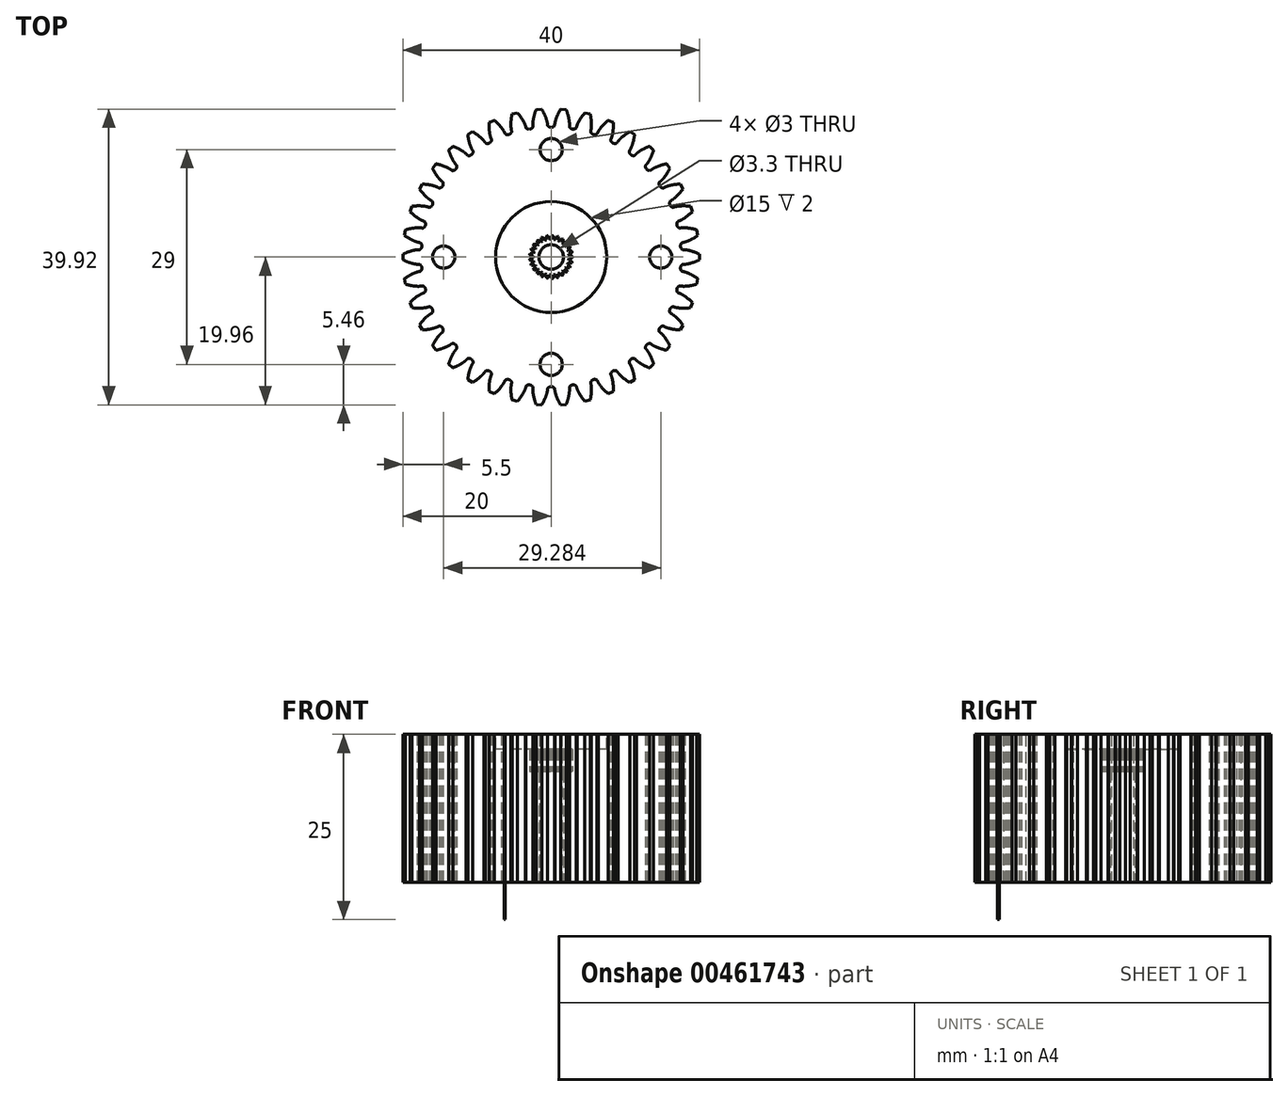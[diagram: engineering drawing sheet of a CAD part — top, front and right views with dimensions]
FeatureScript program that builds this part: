
annotation { "Feature Type Name" : "Feature", "Feature Type Description" : "" }
export const myFeature = defineFeature(function(context is Context, id is Id, definition is map)
    precondition{}
    {
        {
            var Q0;
            Q0=qCreatedBy(makeId("Top.planeOp"),FACE);
            var sketch = newSketch(context, id + "F0", { "sketchPlane" : qUnion([Q0])});
            skLineSegment(sketch, "E0", {"start": v(-6.71, 17.47) * mm, "end": v(-6.37, 16.97) * mm});
            skLineSegment(sketch, "E1", {"start": v(-6.37, 16.97) * mm, "end": v(-6.2, 16.63) * mm});
            skArc(sketch, "E2", {"start": v(-6.71, 17.47) * mm, "mid": v(-7.17, 18) * mm, "end": v(-7.69, 18.46) * mm});
            skLineSegment(sketch, "E3", {"start": v(-8.38, 18.16) * mm, "end": v(-7.69, 18.46) * mm});
            skArc(sketch, "E4", {"start": v(-6.2, 16.63) * mm, "mid": v(-6.27, 16.78) * mm, "end": v(-6.35, 16.93) * mm});
            skArc(sketch, "E5", {"start": v(-6.2, 16.63) * mm, "mid": v(-5.68, 16.55) * mm, "end": v(-5.32, 16.93) * mm});
            skArc(sketch, "E6", {"start": v(-6.35, 16.93) * mm, "mid": v(-6.52, 17.2) * mm, "end": v(-6.71, 17.47) * mm});
            skArc(sketch, "E7", {"start": v(-5.28, 19.3) * mm, "mid": v(-5.4, 18.6) * mm, "end": v(-5.43, 17.9) * mm});
            skArc(sketch, "E8", {"start": v(-5.43, 17.9) * mm, "mid": v(-5.42, 17.59) * mm, "end": v(-5.39, 17.26) * mm});
            skArc(sketch, "E9", {"start": v(-5.39, 17.26) * mm, "mid": v(-5.36, 17.1) * mm, "end": v(-5.32, 16.93) * mm});
            skLineSegment(sketch, "E10", {"start": v(-11.25, 16.53) * mm, "end": v(-10.62, 16.95) * mm});
            skArc(sketch, "E11", {"start": v(-9.5, 16.13) * mm, "mid": v(-10.04, 16.57) * mm, "end": v(-10.62, 16.95) * mm});
            skArc(sketch, "E12", {"start": v(-8.86, 15.38) * mm, "mid": v(-8.33, 15.4) * mm, "end": v(-8.03, 15.83) * mm});
            skArc(sketch, "E13", {"start": v(-9.05, 15.66) * mm, "mid": v(-9.26, 15.9) * mm, "end": v(-9.5, 16.13) * mm});
            skArc(sketch, "E14", {"start": v(-8.86, 15.38) * mm, "mid": v(-8.95, 15.52) * mm, "end": v(-9.05, 15.66) * mm});
            skArc(sketch, "E15", {"start": v(-8.16, 16.14) * mm, "mid": v(-8.1, 15.98) * mm, "end": v(-8.03, 15.83) * mm});
            skArc(sketch, "E16", {"start": v(-8.3, 16.77) * mm, "mid": v(-8.24, 16.45) * mm, "end": v(-8.16, 16.14) * mm});
            skArc(sketch, "E17", {"start": v(-8.38, 18.16) * mm, "mid": v(-8.38, 17.46) * mm, "end": v(-8.3, 16.77) * mm});
            skLineSegment(sketch, "E18", {"start": v(-13.82, 14.46) * mm, "end": v(-13.26, 14.97) * mm});
            skArc(sketch, "E19", {"start": v(-12.02, 14.34) * mm, "mid": v(-12.63, 14.69) * mm, "end": v(-13.26, 14.97) * mm});
            skArc(sketch, "E20", {"start": v(-11.27, 13.71) * mm, "mid": v(-10.75, 13.81) * mm, "end": v(-10.53, 14.3) * mm});
            skArc(sketch, "E21", {"start": v(-11.5, 13.95) * mm, "mid": v(-11.76, 14.16) * mm, "end": v(-12.02, 14.34) * mm});
            skArc(sketch, "E22", {"start": v(-11.27, 13.71) * mm, "mid": v(-11.38, 13.84) * mm, "end": v(-11.5, 13.95) * mm});
            skArc(sketch, "E23", {"start": v(-10.7, 14.58) * mm, "mid": v(-10.62, 14.43) * mm, "end": v(-10.53, 14.3) * mm});
            skArc(sketch, "E24", {"start": v(-10.95, 15.18) * mm, "mid": v(-10.84, 14.87) * mm, "end": v(-10.7, 14.58) * mm});
            skArc(sketch, "E25", {"start": v(-11.25, 16.53) * mm, "mid": v(-11.14, 15.85) * mm, "end": v(-10.95, 15.18) * mm});
            skLineSegment(sketch, "E26", {"start": v(-16.01, 11.98) * mm, "end": v(-15.55, 12.58) * mm});
            skArc(sketch, "E27", {"start": v(-14.22, 12.17) * mm, "mid": v(-14.87, 12.4) * mm, "end": v(-15.55, 12.58) * mm});
            skArc(sketch, "E28", {"start": v(-13.37, 11.67) * mm, "mid": v(-12.88, 11.85) * mm, "end": v(-12.74, 12.36) * mm});
            skArc(sketch, "E29", {"start": v(-13.65, 11.87) * mm, "mid": v(-13.93, 12.03) * mm, "end": v(-14.22, 12.17) * mm});
            skArc(sketch, "E30", {"start": v(-13.37, 11.67) * mm, "mid": v(-13.5, 11.78) * mm, "end": v(-13.65, 11.87) * mm});
            skArc(sketch, "E31", {"start": v(-12.96, 12.62) * mm, "mid": v(-12.85, 12.49) * mm, "end": v(-12.74, 12.36) * mm});
            skArc(sketch, "E32", {"start": v(-13.3, 13.17) * mm, "mid": v(-13.14, 12.88) * mm, "end": v(-12.96, 12.62) * mm});
            skArc(sketch, "E33", {"start": v(-13.82, 14.46) * mm, "mid": v(-13.6, 13.8) * mm, "end": v(-13.3, 13.17) * mm});
            skLineSegment(sketch, "E34", {"start": v(-17.77, 9.18) * mm, "end": v(-17.4, 9.85) * mm});
            skArc(sketch, "E35", {"start": v(-16.03, 9.66) * mm, "mid": v(-16.71, 9.8) * mm, "end": v(-17.4, 9.85) * mm});
            skArc(sketch, "E36", {"start": v(-15.11, 9.31) * mm, "mid": v(-14.65, 9.57) * mm, "end": v(-14.6, 10.1) * mm});
            skArc(sketch, "E37", {"start": v(-15.41, 9.46) * mm, "mid": v(-15.72, 9.58) * mm, "end": v(-16.03, 9.66) * mm});
            skArc(sketch, "E38", {"start": v(-15.11, 9.31) * mm, "mid": v(-15.26, 9.4) * mm, "end": v(-15.41, 9.46) * mm});
            skArc(sketch, "E39", {"start": v(-14.86, 10.31) * mm, "mid": v(-14.73, 10.2) * mm, "end": v(-14.6, 10.1) * mm});
            skArc(sketch, "E40", {"start": v(-15.29, 10.8) * mm, "mid": v(-15.08, 10.55) * mm, "end": v(-14.86, 10.31) * mm});
            skArc(sketch, "E41", {"start": v(-16.01, 11.98) * mm, "mid": v(-15.68, 11.37) * mm, "end": v(-15.29, 10.8) * mm});
            skLineSegment(sketch, "E42", {"start": v(-19.04, 6.13) * mm, "end": v(-18.8, 6.85) * mm});
            skArc(sketch, "E43", {"start": v(-17.4, 6.9) * mm, "mid": v(-18.1, 6.9) * mm, "end": v(-18.8, 6.85) * mm});
            skArc(sketch, "E44", {"start": v(-16.44, 6.7) * mm, "mid": v(-16.03, 7.03) * mm, "end": v(-16.06, 7.56) * mm});
            skArc(sketch, "E45", {"start": v(-16.76, 6.8) * mm, "mid": v(-17.08, 6.86) * mm, "end": v(-17.4, 6.9) * mm});
            skArc(sketch, "E46", {"start": v(-16.44, 6.7) * mm, "mid": v(-16.6, 6.75) * mm, "end": v(-16.76, 6.8) * mm});
            skArc(sketch, "E47", {"start": v(-16.35, 7.73) * mm, "mid": v(-16.2, 7.64) * mm, "end": v(-16.06, 7.56) * mm});
            skArc(sketch, "E48", {"start": v(-16.86, 8.13) * mm, "mid": v(-16.61, 7.92) * mm, "end": v(-16.35, 7.73) * mm});
            skArc(sketch, "E49", {"start": v(-17.77, 9.18) * mm, "mid": v(-17.34, 8.63) * mm, "end": v(-16.86, 8.13) * mm});
            skLineSegment(sketch, "E50", {"start": v(-19.79, 2.92) * mm, "end": v(-19.66, 3.66) * mm});
            skArc(sketch, "E51", {"start": v(-18.3, 3.93) * mm, "mid": v(-18.99, 3.84) * mm, "end": v(-19.66, 3.66) * mm});
            skArc(sketch, "E52", {"start": v(-17.32, 3.9) * mm, "mid": v(-16.97, 4.3) * mm, "end": v(-17.09, 4.81) * mm});
            skArc(sketch, "E53", {"start": v(-17.65, 3.95) * mm, "mid": v(-17.97, 3.95) * mm, "end": v(-18.3, 3.93) * mm});
            skArc(sketch, "E54", {"start": v(-17.32, 3.9) * mm, "mid": v(-17.48, 3.93) * mm, "end": v(-17.65, 3.95) * mm});
            skArc(sketch, "E55", {"start": v(-17.4, 4.93) * mm, "mid": v(-17.24, 4.87) * mm, "end": v(-17.09, 4.81) * mm});
            skArc(sketch, "E56", {"start": v(-17.96, 5.25) * mm, "mid": v(-17.69, 5.08) * mm, "end": v(-17.4, 4.93) * mm});
            skArc(sketch, "E57", {"start": v(-19.04, 6.13) * mm, "mid": v(-18.52, 5.66) * mm, "end": v(-17.96, 5.25) * mm});
            skLineSegment(sketch, "E58", {"start": v(-20, -0.38) * mm, "end": v(-20, 0.38) * mm});
            skArc(sketch, "E59", {"start": v(-18.7, 0.87) * mm, "mid": v(-19.36, 0.66) * mm, "end": v(-20, 0.38) * mm});
            skArc(sketch, "E60", {"start": v(-17.72, 1) * mm, "mid": v(-17.44, 1.45) * mm, "end": v(-17.64, 1.93) * mm});
            skArc(sketch, "E61", {"start": v(-18.06, 0.99) * mm, "mid": v(-18.38, 0.94) * mm, "end": v(-18.7, 0.87) * mm});
            skArc(sketch, "E62", {"start": v(-17.72, 1) * mm, "mid": v(-17.9, 1) * mm, "end": v(-18.06, 0.99) * mm});
            skArc(sketch, "E63", {"start": v(-17.98, 2) * mm, "mid": v(-17.81, 1.96) * mm, "end": v(-17.64, 1.93) * mm});
            skArc(sketch, "E64", {"start": v(-18.58, 2.22) * mm, "mid": v(-18.28, 2.1) * mm, "end": v(-17.98, 2) * mm});
            skArc(sketch, "E65", {"start": v(-19.79, 2.92) * mm, "mid": v(-19.2, 2.54) * mm, "end": v(-18.58, 2.22) * mm});
            skLineSegment(sketch, "E66", {"start": v(-19.66, -3.66) * mm, "end": v(-19.79, -2.92) * mm});
            skArc(sketch, "E67", {"start": v(-18.58, -2.22) * mm, "mid": v(-19.2, -2.54) * mm, "end": v(-19.79, -2.92) * mm});
            skArc(sketch, "E68", {"start": v(-17.64, -1.93) * mm, "mid": v(-17.44, -1.45) * mm, "end": v(-17.72, -1) * mm});
            skArc(sketch, "E69", {"start": v(-17.98, -2) * mm, "mid": v(-18.28, -2.1) * mm, "end": v(-18.58, -2.22) * mm});
            skArc(sketch, "E70", {"start": v(-17.64, -1.93) * mm, "mid": v(-17.81, -1.96) * mm, "end": v(-17.98, -2) * mm});
            skArc(sketch, "E71", {"start": v(-18.06, -0.99) * mm, "mid": v(-17.9, -1) * mm, "end": v(-17.72, -1) * mm});
            skArc(sketch, "E72", {"start": v(-18.7, -0.87) * mm, "mid": v(-18.38, -0.94) * mm, "end": v(-18.06, -0.99) * mm});
            skArc(sketch, "E73", {"start": v(-20, -0.38) * mm, "mid": v(-19.36, -0.66) * mm, "end": v(-18.7, -0.87) * mm});
            skLineSegment(sketch, "E74", {"start": v(-18.8, -6.85) * mm, "end": v(-19.04, -6.13) * mm});
            skArc(sketch, "E75", {"start": v(-17.96, -5.25) * mm, "mid": v(-18.52, -5.66) * mm, "end": v(-19.04, -6.13) * mm});
            skArc(sketch, "E76", {"start": v(-17.09, -4.81) * mm, "mid": v(-16.97, -4.3) * mm, "end": v(-17.32, -3.9) * mm});
            skArc(sketch, "E77", {"start": v(-17.4, -4.93) * mm, "mid": v(-17.69, -5.08) * mm, "end": v(-17.96, -5.25) * mm});
            skArc(sketch, "E78", {"start": v(-17.09, -4.81) * mm, "mid": v(-17.24, -4.87) * mm, "end": v(-17.4, -4.93) * mm});
            skArc(sketch, "E79", {"start": v(-17.65, -3.95) * mm, "mid": v(-17.48, -3.93) * mm, "end": v(-17.32, -3.9) * mm});
            skArc(sketch, "E80", {"start": v(-18.3, -3.93) * mm, "mid": v(-17.97, -3.95) * mm, "end": v(-17.65, -3.95) * mm});
            skArc(sketch, "E81", {"start": v(-19.66, -3.66) * mm, "mid": v(-18.99, -3.84) * mm, "end": v(-18.3, -3.93) * mm});
            skLineSegment(sketch, "E82", {"start": v(-17.4, -9.85) * mm, "end": v(-17.77, -9.18) * mm});
            skArc(sketch, "E83", {"start": v(-16.86, -8.13) * mm, "mid": v(-17.34, -8.63) * mm, "end": v(-17.77, -9.18) * mm});
            skArc(sketch, "E84", {"start": v(-16.06, -7.56) * mm, "mid": v(-16.03, -7.03) * mm, "end": v(-16.44, -6.7) * mm});
            skArc(sketch, "E85", {"start": v(-16.35, -7.73) * mm, "mid": v(-16.61, -7.92) * mm, "end": v(-16.86, -8.13) * mm});
            skArc(sketch, "E86", {"start": v(-16.06, -7.56) * mm, "mid": v(-16.2, -7.64) * mm, "end": v(-16.35, -7.73) * mm});
            skArc(sketch, "E87", {"start": v(-16.76, -6.8) * mm, "mid": v(-16.6, -6.75) * mm, "end": v(-16.44, -6.7) * mm});
            skArc(sketch, "E88", {"start": v(-17.4, -6.9) * mm, "mid": v(-17.08, -6.86) * mm, "end": v(-16.76, -6.8) * mm});
            skArc(sketch, "E89", {"start": v(-18.8, -6.85) * mm, "mid": v(-18.1, -6.9) * mm, "end": v(-17.4, -6.9) * mm});
            skLineSegment(sketch, "E90", {"start": v(-15.55, -12.58) * mm, "end": v(-16.01, -11.98) * mm});
            skArc(sketch, "E91", {"start": v(-15.29, -10.8) * mm, "mid": v(-15.68, -11.37) * mm, "end": v(-16.01, -11.98) * mm});
            skArc(sketch, "E92", {"start": v(-14.6, -10.1) * mm, "mid": v(-14.65, -9.57) * mm, "end": v(-15.11, -9.31) * mm});
            skArc(sketch, "E93", {"start": v(-14.86, -10.31) * mm, "mid": v(-15.08, -10.55) * mm, "end": v(-15.29, -10.8) * mm});
            skArc(sketch, "E94", {"start": v(-14.6, -10.1) * mm, "mid": v(-14.73, -10.2) * mm, "end": v(-14.86, -10.31) * mm});
            skArc(sketch, "E95", {"start": v(-15.41, -9.46) * mm, "mid": v(-15.26, -9.4) * mm, "end": v(-15.11, -9.31) * mm});
            skArc(sketch, "E96", {"start": v(-16.03, -9.66) * mm, "mid": v(-15.72, -9.58) * mm, "end": v(-15.41, -9.46) * mm});
            skArc(sketch, "E97", {"start": v(-17.4, -9.85) * mm, "mid": v(-16.71, -9.8) * mm, "end": v(-16.03, -9.66) * mm});
            skLineSegment(sketch, "E98", {"start": v(-13.26, -14.97) * mm, "end": v(-13.82, -14.46) * mm});
            skArc(sketch, "E99", {"start": v(-13.3, -13.17) * mm, "mid": v(-13.6, -13.8) * mm, "end": v(-13.82, -14.46) * mm});
            skArc(sketch, "E100", {"start": v(-12.74, -12.36) * mm, "mid": v(-12.88, -11.85) * mm, "end": v(-13.37, -11.67) * mm});
            skArc(sketch, "E101", {"start": v(-12.96, -12.62) * mm, "mid": v(-13.14, -12.88) * mm, "end": v(-13.3, -13.17) * mm});
            skArc(sketch, "E102", {"start": v(-12.74, -12.36) * mm, "mid": v(-12.85, -12.49) * mm, "end": v(-12.96, -12.62) * mm});
            skArc(sketch, "E103", {"start": v(-13.64, -11.87) * mm, "mid": v(-13.5, -11.78) * mm, "end": v(-13.37, -11.67) * mm});
            skArc(sketch, "E104", {"start": v(-14.22, -12.17) * mm, "mid": v(-13.93, -12.03) * mm, "end": v(-13.64, -11.87) * mm});
            skArc(sketch, "E105", {"start": v(-15.55, -12.58) * mm, "mid": v(-14.87, -12.4) * mm, "end": v(-14.22, -12.17) * mm});
            skLineSegment(sketch, "E106", {"start": v(-10.62, -16.95) * mm, "end": v(-11.25, -16.53) * mm});
            skArc(sketch, "E107", {"start": v(-10.95, -15.18) * mm, "mid": v(-11.14, -15.85) * mm, "end": v(-11.25, -16.53) * mm});
            skArc(sketch, "E108", {"start": v(-10.53, -14.3) * mm, "mid": v(-10.75, -13.81) * mm, "end": v(-11.27, -13.71) * mm});
            skArc(sketch, "E109", {"start": v(-10.7, -14.58) * mm, "mid": v(-10.84, -14.87) * mm, "end": v(-10.95, -15.18) * mm});
            skArc(sketch, "E110", {"start": v(-10.53, -14.3) * mm, "mid": v(-10.62, -14.43) * mm, "end": v(-10.7, -14.58) * mm});
            skArc(sketch, "E111", {"start": v(-11.5, -13.95) * mm, "mid": v(-11.38, -13.84) * mm, "end": v(-11.27, -13.71) * mm});
            skArc(sketch, "E112", {"start": v(-12.02, -14.34) * mm, "mid": v(-11.76, -14.16) * mm, "end": v(-11.5, -13.95) * mm});
            skArc(sketch, "E113", {"start": v(-13.26, -14.97) * mm, "mid": v(-12.63, -14.69) * mm, "end": v(-12.02, -14.34) * mm});
            skLineSegment(sketch, "E114", {"start": v(-7.69, -18.46) * mm, "end": v(-8.38, -18.16) * mm});
            skArc(sketch, "E115", {"start": v(-8.3, -16.77) * mm, "mid": v(-8.38, -17.46) * mm, "end": v(-8.38, -18.16) * mm});
            skArc(sketch, "E116", {"start": v(-8.03, -15.83) * mm, "mid": v(-8.33, -15.4) * mm, "end": v(-8.86, -15.38) * mm});
            skArc(sketch, "E117", {"start": v(-8.16, -16.14) * mm, "mid": v(-8.24, -16.45) * mm, "end": v(-8.3, -16.77) * mm});
            skArc(sketch, "E118", {"start": v(-8.03, -15.83) * mm, "mid": v(-8.1, -15.98) * mm, "end": v(-8.16, -16.14) * mm});
            skArc(sketch, "E119", {"start": v(-9.05, -15.66) * mm, "mid": v(-8.95, -15.52) * mm, "end": v(-8.86, -15.38) * mm});
            skArc(sketch, "E120", {"start": v(-9.5, -16.13) * mm, "mid": v(-9.26, -15.9) * mm, "end": v(-9.05, -15.66) * mm});
            skArc(sketch, "E121", {"start": v(-10.62, -16.95) * mm, "mid": v(-10.04, -16.57) * mm, "end": v(-9.5, -16.13) * mm});
            skLineSegment(sketch, "E122", {"start": v(-4.54, -19.48) * mm, "end": v(-5.28, -19.3) * mm});
            skArc(sketch, "E123", {"start": v(-5.43, -17.9) * mm, "mid": v(-5.4, -18.6) * mm, "end": v(-5.28, -19.3) * mm});
            skArc(sketch, "E124", {"start": v(-5.32, -16.93) * mm, "mid": v(-5.68, -16.55) * mm, "end": v(-6.2, -16.63) * mm});
            skArc(sketch, "E125", {"start": v(-5.39, -17.26) * mm, "mid": v(-5.42, -17.59) * mm, "end": v(-5.43, -17.9) * mm});
            skArc(sketch, "E126", {"start": v(-5.32, -16.93) * mm, "mid": v(-5.36, -17.1) * mm, "end": v(-5.39, -17.26) * mm});
            skArc(sketch, "E127", {"start": v(-6.35, -16.93) * mm, "mid": v(-6.27, -16.78) * mm, "end": v(-6.2, -16.63) * mm});
            skArc(sketch, "E128", {"start": v(-6.71, -17.47) * mm, "mid": v(-6.52, -17.2) * mm, "end": v(-6.35, -16.93) * mm});
            skArc(sketch, "E129", {"start": v(-7.69, -18.46) * mm, "mid": v(-7.17, -18) * mm, "end": v(-6.71, -17.47) * mm});
            skLineSegment(sketch, "E130", {"start": v(-1.27, -19.96) * mm, "end": v(-2.03, -19.9) * mm});
            skArc(sketch, "E131", {"start": v(-2.4, -18.56) * mm, "mid": v(-2.25, -19.24) * mm, "end": v(-2.03, -19.9) * mm});
            skArc(sketch, "E132", {"start": v(-2.46, -17.58) * mm, "mid": v(-2.88, -17.26) * mm, "end": v(-3.38, -17.42) * mm});
            skArc(sketch, "E133", {"start": v(-2.47, -17.92) * mm, "mid": v(-2.46, -18.24) * mm, "end": v(-2.4, -18.56) * mm});
            skArc(sketch, "E134", {"start": v(-2.46, -17.58) * mm, "mid": v(-2.47, -17.75) * mm, "end": v(-2.47, -17.92) * mm});
            skArc(sketch, "E135", {"start": v(-3.48, -17.75) * mm, "mid": v(-3.43, -17.59) * mm, "end": v(-3.38, -17.42) * mm});
            skArc(sketch, "E136", {"start": v(-3.75, -18.34) * mm, "mid": v(-3.6, -18.05) * mm, "end": v(-3.48, -17.75) * mm});
            skArc(sketch, "E137", {"start": v(-4.54, -19.48) * mm, "mid": v(-4.11, -18.93) * mm, "end": v(-3.75, -18.34) * mm});
            skLineSegment(sketch, "E138", {"start": v(2.03, -19.9) * mm, "end": v(1.27, -19.96) * mm});
            skArc(sketch, "E139", {"start": v(0.68, -18.7) * mm, "mid": v(0.94, -19.35) * mm, "end": v(1.27, -19.96) * mm});
            skArc(sketch, "E140", {"start": v(0.47, -17.74) * mm, "mid": v(0, -17.5) * mm, "end": v(-0.47, -17.74) * mm});
            skArc(sketch, "E141", {"start": v(0.5, -18.08) * mm, "mid": v(0.58, -18.4) * mm, "end": v(0.68, -18.7) * mm});
            skArc(sketch, "E142", {"start": v(0.47, -17.74) * mm, "mid": v(0.48, -17.91) * mm, "end": v(0.5, -18.08) * mm});
            skArc(sketch, "E143", {"start": v(-0.5, -18.08) * mm, "mid": v(-0.48, -17.91) * mm, "end": v(-0.47, -17.74) * mm});
            skArc(sketch, "E144", {"start": v(-0.68, -18.7) * mm, "mid": v(-0.58, -18.4) * mm, "end": v(-0.5, -18.08) * mm});
            skArc(sketch, "E145", {"start": v(-1.27, -19.96) * mm, "mid": v(-0.94, -19.35) * mm, "end": v(-0.68, -18.7) * mm});
            skLineSegment(sketch, "E146", {"start": v(5.28, -19.3) * mm, "end": v(4.54, -19.48) * mm});
            skArc(sketch, "E147", {"start": v(3.75, -18.34) * mm, "mid": v(4.11, -18.93) * mm, "end": v(4.54, -19.48) * mm});
            skArc(sketch, "E148", {"start": v(3.38, -17.42) * mm, "mid": v(2.88, -17.26) * mm, "end": v(2.46, -17.58) * mm});
            skArc(sketch, "E149", {"start": v(3.48, -17.75) * mm, "mid": v(3.6, -18.05) * mm, "end": v(3.75, -18.34) * mm});
            skArc(sketch, "E150", {"start": v(3.38, -17.42) * mm, "mid": v(3.43, -17.59) * mm, "end": v(3.48, -17.75) * mm});
            skArc(sketch, "E151", {"start": v(2.47, -17.92) * mm, "mid": v(2.47, -17.75) * mm, "end": v(2.46, -17.58) * mm});
            skArc(sketch, "E152", {"start": v(2.41, -18.56) * mm, "mid": v(2.46, -18.24) * mm, "end": v(2.47, -17.92) * mm});
            skArc(sketch, "E153", {"start": v(2.03, -19.9) * mm, "mid": v(2.25, -19.24) * mm, "end": v(2.41, -18.56) * mm});
            skLineSegment(sketch, "E154", {"start": v(8.38, -18.16) * mm, "end": v(7.69, -18.46) * mm});
            skArc(sketch, "E155", {"start": v(6.71, -17.47) * mm, "mid": v(7.17, -18) * mm, "end": v(7.69, -18.46) * mm});
            skArc(sketch, "E156", {"start": v(6.2, -16.63) * mm, "mid": v(5.68, -16.55) * mm, "end": v(5.32, -16.93) * mm});
            skArc(sketch, "E157", {"start": v(6.35, -16.93) * mm, "mid": v(6.52, -17.2) * mm, "end": v(6.71, -17.47) * mm});
            skArc(sketch, "E158", {"start": v(6.2, -16.63) * mm, "mid": v(6.27, -16.78) * mm, "end": v(6.35, -16.93) * mm});
            skArc(sketch, "E159", {"start": v(5.39, -17.26) * mm, "mid": v(5.36, -17.1) * mm, "end": v(5.32, -16.93) * mm});
            skArc(sketch, "E160", {"start": v(5.43, -17.9) * mm, "mid": v(5.42, -17.59) * mm, "end": v(5.39, -17.26) * mm});
            skArc(sketch, "E161", {"start": v(5.28, -19.3) * mm, "mid": v(5.4, -18.6) * mm, "end": v(5.43, -17.9) * mm});
            skLineSegment(sketch, "E162", {"start": v(11.25, -16.53) * mm, "end": v(10.62, -16.95) * mm});
            skArc(sketch, "E163", {"start": v(9.5, -16.13) * mm, "mid": v(10.04, -16.57) * mm, "end": v(10.62, -16.95) * mm});
            skArc(sketch, "E164", {"start": v(8.86, -15.38) * mm, "mid": v(8.33, -15.4) * mm, "end": v(8.03, -15.83) * mm});
            skArc(sketch, "E165", {"start": v(9.05, -15.66) * mm, "mid": v(9.26, -15.9) * mm, "end": v(9.5, -16.13) * mm});
            skArc(sketch, "E166", {"start": v(8.86, -15.38) * mm, "mid": v(8.95, -15.52) * mm, "end": v(9.05, -15.66) * mm});
            skArc(sketch, "E167", {"start": v(8.16, -16.14) * mm, "mid": v(8.1, -15.98) * mm, "end": v(8.03, -15.83) * mm});
            skArc(sketch, "E168", {"start": v(8.3, -16.77) * mm, "mid": v(8.24, -16.45) * mm, "end": v(8.16, -16.14) * mm});
            skArc(sketch, "E169", {"start": v(8.38, -18.16) * mm, "mid": v(8.38, -17.46) * mm, "end": v(8.3, -16.77) * mm});
            skLineSegment(sketch, "E170", {"start": v(13.82, -14.46) * mm, "end": v(13.26, -14.97) * mm});
            skArc(sketch, "E171", {"start": v(12.02, -14.34) * mm, "mid": v(12.63, -14.69) * mm, "end": v(13.26, -14.97) * mm});
            skArc(sketch, "E172", {"start": v(11.27, -13.71) * mm, "mid": v(10.75, -13.81) * mm, "end": v(10.53, -14.3) * mm});
            skArc(sketch, "E173", {"start": v(11.5, -13.95) * mm, "mid": v(11.76, -14.16) * mm, "end": v(12.02, -14.34) * mm});
            skArc(sketch, "E174", {"start": v(11.27, -13.71) * mm, "mid": v(11.38, -13.84) * mm, "end": v(11.5, -13.95) * mm});
            skArc(sketch, "E175", {"start": v(10.7, -14.58) * mm, "mid": v(10.62, -14.43) * mm, "end": v(10.53, -14.3) * mm});
            skArc(sketch, "E176", {"start": v(10.95, -15.18) * mm, "mid": v(10.84, -14.87) * mm, "end": v(10.7, -14.58) * mm});
            skArc(sketch, "E177", {"start": v(11.25, -16.53) * mm, "mid": v(11.14, -15.85) * mm, "end": v(10.95, -15.18) * mm});
            skLineSegment(sketch, "E178", {"start": v(16.01, -11.98) * mm, "end": v(15.55, -12.58) * mm});
            skArc(sketch, "E179", {"start": v(14.22, -12.17) * mm, "mid": v(14.87, -12.4) * mm, "end": v(15.55, -12.58) * mm});
            skArc(sketch, "E180", {"start": v(13.37, -11.67) * mm, "mid": v(12.88, -11.85) * mm, "end": v(12.74, -12.36) * mm});
            skArc(sketch, "E181", {"start": v(13.65, -11.87) * mm, "mid": v(13.93, -12.03) * mm, "end": v(14.22, -12.17) * mm});
            skArc(sketch, "E182", {"start": v(13.37, -11.67) * mm, "mid": v(13.5, -11.78) * mm, "end": v(13.65, -11.87) * mm});
            skArc(sketch, "E183", {"start": v(12.96, -12.62) * mm, "mid": v(12.85, -12.49) * mm, "end": v(12.74, -12.36) * mm});
            skArc(sketch, "E184", {"start": v(13.3, -13.17) * mm, "mid": v(13.14, -12.88) * mm, "end": v(12.96, -12.62) * mm});
            skArc(sketch, "E185", {"start": v(13.82, -14.46) * mm, "mid": v(13.6, -13.8) * mm, "end": v(13.3, -13.17) * mm});
            skLineSegment(sketch, "E186", {"start": v(17.77, -9.18) * mm, "end": v(17.4, -9.85) * mm});
            skArc(sketch, "E187", {"start": v(16.03, -9.66) * mm, "mid": v(16.71, -9.8) * mm, "end": v(17.4, -9.85) * mm});
            skArc(sketch, "E188", {"start": v(15.11, -9.31) * mm, "mid": v(14.65, -9.57) * mm, "end": v(14.6, -10.1) * mm});
            skArc(sketch, "E189", {"start": v(15.41, -9.46) * mm, "mid": v(15.72, -9.58) * mm, "end": v(16.03, -9.66) * mm});
            skArc(sketch, "E190", {"start": v(15.11, -9.31) * mm, "mid": v(15.26, -9.4) * mm, "end": v(15.41, -9.46) * mm});
            skArc(sketch, "E191", {"start": v(14.86, -10.31) * mm, "mid": v(14.73, -10.2) * mm, "end": v(14.6, -10.1) * mm});
            skArc(sketch, "E192", {"start": v(15.29, -10.8) * mm, "mid": v(15.08, -10.55) * mm, "end": v(14.86, -10.31) * mm});
            skArc(sketch, "E193", {"start": v(16.01, -11.98) * mm, "mid": v(15.68, -11.37) * mm, "end": v(15.29, -10.8) * mm});
            skLineSegment(sketch, "E194", {"start": v(19.04, -6.13) * mm, "end": v(18.8, -6.85) * mm});
            skArc(sketch, "E195", {"start": v(17.4, -6.9) * mm, "mid": v(18.1, -6.9) * mm, "end": v(18.8, -6.85) * mm});
            skArc(sketch, "E196", {"start": v(16.44, -6.7) * mm, "mid": v(16.03, -7.03) * mm, "end": v(16.06, -7.56) * mm});
            skArc(sketch, "E197", {"start": v(16.76, -6.8) * mm, "mid": v(17.08, -6.86) * mm, "end": v(17.4, -6.9) * mm});
            skArc(sketch, "E198", {"start": v(16.44, -6.7) * mm, "mid": v(16.6, -6.75) * mm, "end": v(16.76, -6.8) * mm});
            skArc(sketch, "E199", {"start": v(16.35, -7.73) * mm, "mid": v(16.2, -7.64) * mm, "end": v(16.06, -7.56) * mm});
            skArc(sketch, "E200", {"start": v(16.86, -8.13) * mm, "mid": v(16.61, -7.92) * mm, "end": v(16.35, -7.73) * mm});
            skArc(sketch, "E201", {"start": v(17.77, -9.18) * mm, "mid": v(17.34, -8.63) * mm, "end": v(16.86, -8.13) * mm});
            skLineSegment(sketch, "E202", {"start": v(19.79, -2.92) * mm, "end": v(19.66, -3.66) * mm});
            skArc(sketch, "E203", {"start": v(18.3, -3.93) * mm, "mid": v(18.99, -3.84) * mm, "end": v(19.66, -3.66) * mm});
            skArc(sketch, "E204", {"start": v(17.32, -3.9) * mm, "mid": v(16.97, -4.3) * mm, "end": v(17.09, -4.81) * mm});
            skArc(sketch, "E205", {"start": v(17.65, -3.95) * mm, "mid": v(17.97, -3.95) * mm, "end": v(18.3, -3.93) * mm});
            skArc(sketch, "E206", {"start": v(17.32, -3.9) * mm, "mid": v(17.48, -3.93) * mm, "end": v(17.65, -3.95) * mm});
            skArc(sketch, "E207", {"start": v(17.4, -4.93) * mm, "mid": v(17.24, -4.87) * mm, "end": v(17.09, -4.81) * mm});
            skArc(sketch, "E208", {"start": v(17.96, -5.25) * mm, "mid": v(17.69, -5.08) * mm, "end": v(17.4, -4.93) * mm});
            skArc(sketch, "E209", {"start": v(19.04, -6.13) * mm, "mid": v(18.52, -5.66) * mm, "end": v(17.96, -5.25) * mm});
            skLineSegment(sketch, "E210", {"start": v(20, 0.38) * mm, "end": v(20, -0.38) * mm});
            skArc(sketch, "E211", {"start": v(18.7, -0.87) * mm, "mid": v(19.36, -0.66) * mm, "end": v(20, -0.38) * mm});
            skArc(sketch, "E212", {"start": v(17.72, -1) * mm, "mid": v(17.44, -1.45) * mm, "end": v(17.64, -1.93) * mm});
            skArc(sketch, "E213", {"start": v(18.06, -0.99) * mm, "mid": v(18.38, -0.94) * mm, "end": v(18.7, -0.87) * mm});
            skArc(sketch, "E214", {"start": v(17.72, -1) * mm, "mid": v(17.9, -1) * mm, "end": v(18.06, -0.99) * mm});
            skArc(sketch, "E215", {"start": v(17.98, -2) * mm, "mid": v(17.81, -1.96) * mm, "end": v(17.64, -1.93) * mm});
            skArc(sketch, "E216", {"start": v(18.58, -2.22) * mm, "mid": v(18.28, -2.1) * mm, "end": v(17.98, -2) * mm});
            skArc(sketch, "E217", {"start": v(19.79, -2.92) * mm, "mid": v(19.2, -2.54) * mm, "end": v(18.58, -2.22) * mm});
            skLineSegment(sketch, "E218", {"start": v(19.66, 3.66) * mm, "end": v(19.79, 2.92) * mm});
            skArc(sketch, "E219", {"start": v(18.58, 2.22) * mm, "mid": v(19.2, 2.54) * mm, "end": v(19.79, 2.92) * mm});
            skArc(sketch, "E220", {"start": v(17.64, 1.93) * mm, "mid": v(17.44, 1.45) * mm, "end": v(17.72, 1) * mm});
            skArc(sketch, "E221", {"start": v(17.98, 2) * mm, "mid": v(18.28, 2.1) * mm, "end": v(18.58, 2.22) * mm});
            skArc(sketch, "E222", {"start": v(17.64, 1.93) * mm, "mid": v(17.81, 1.96) * mm, "end": v(17.98, 2) * mm});
            skArc(sketch, "E223", {"start": v(18.06, 0.99) * mm, "mid": v(17.9, 1) * mm, "end": v(17.72, 1) * mm});
            skArc(sketch, "E224", {"start": v(18.7, 0.87) * mm, "mid": v(18.38, 0.94) * mm, "end": v(18.06, 0.99) * mm});
            skArc(sketch, "E225", {"start": v(20, 0.38) * mm, "mid": v(19.36, 0.66) * mm, "end": v(18.7, 0.87) * mm});
            skLineSegment(sketch, "E226", {"start": v(18.8, 6.85) * mm, "end": v(19.04, 6.13) * mm});
            skArc(sketch, "E227", {"start": v(17.96, 5.25) * mm, "mid": v(18.52, 5.66) * mm, "end": v(19.04, 6.13) * mm});
            skArc(sketch, "E228", {"start": v(17.09, 4.81) * mm, "mid": v(16.97, 4.3) * mm, "end": v(17.32, 3.9) * mm});
            skArc(sketch, "E229", {"start": v(17.4, 4.93) * mm, "mid": v(17.69, 5.08) * mm, "end": v(17.96, 5.25) * mm});
            skArc(sketch, "E230", {"start": v(17.09, 4.81) * mm, "mid": v(17.24, 4.87) * mm, "end": v(17.4, 4.93) * mm});
            skArc(sketch, "E231", {"start": v(17.65, 3.95) * mm, "mid": v(17.48, 3.93) * mm, "end": v(17.32, 3.9) * mm});
            skArc(sketch, "E232", {"start": v(18.3, 3.93) * mm, "mid": v(17.97, 3.95) * mm, "end": v(17.65, 3.95) * mm});
            skArc(sketch, "E233", {"start": v(19.66, 3.66) * mm, "mid": v(18.99, 3.84) * mm, "end": v(18.3, 3.93) * mm});
            skLineSegment(sketch, "E234", {"start": v(17.4, 9.85) * mm, "end": v(17.77, 9.18) * mm});
            skArc(sketch, "E235", {"start": v(16.86, 8.13) * mm, "mid": v(17.34, 8.63) * mm, "end": v(17.77, 9.18) * mm});
            skArc(sketch, "E236", {"start": v(16.06, 7.56) * mm, "mid": v(16.03, 7.03) * mm, "end": v(16.44, 6.7) * mm});
            skArc(sketch, "E237", {"start": v(16.35, 7.73) * mm, "mid": v(16.61, 7.92) * mm, "end": v(16.86, 8.13) * mm});
            skArc(sketch, "E238", {"start": v(16.06, 7.56) * mm, "mid": v(16.2, 7.64) * mm, "end": v(16.35, 7.73) * mm});
            skArc(sketch, "E239", {"start": v(16.76, 6.8) * mm, "mid": v(16.6, 6.75) * mm, "end": v(16.44, 6.7) * mm});
            skArc(sketch, "E240", {"start": v(17.4, 6.9) * mm, "mid": v(17.08, 6.86) * mm, "end": v(16.76, 6.8) * mm});
            skArc(sketch, "E241", {"start": v(18.8, 6.85) * mm, "mid": v(18.1, 6.9) * mm, "end": v(17.4, 6.9) * mm});
            skLineSegment(sketch, "E242", {"start": v(15.55, 12.58) * mm, "end": v(16.01, 11.98) * mm});
            skArc(sketch, "E243", {"start": v(15.29, 10.8) * mm, "mid": v(15.68, 11.37) * mm, "end": v(16.01, 11.98) * mm});
            skArc(sketch, "E244", {"start": v(14.6, 10.1) * mm, "mid": v(14.65, 9.57) * mm, "end": v(15.11, 9.31) * mm});
            skArc(sketch, "E245", {"start": v(14.86, 10.31) * mm, "mid": v(15.08, 10.55) * mm, "end": v(15.29, 10.8) * mm});
            skArc(sketch, "E246", {"start": v(14.6, 10.1) * mm, "mid": v(14.73, 10.2) * mm, "end": v(14.86, 10.31) * mm});
            skArc(sketch, "E247", {"start": v(15.41, 9.46) * mm, "mid": v(15.26, 9.4) * mm, "end": v(15.11, 9.31) * mm});
            skArc(sketch, "E248", {"start": v(16.03, 9.66) * mm, "mid": v(15.72, 9.58) * mm, "end": v(15.41, 9.46) * mm});
            skArc(sketch, "E249", {"start": v(17.4, 9.85) * mm, "mid": v(16.71, 9.8) * mm, "end": v(16.03, 9.66) * mm});
            skLineSegment(sketch, "E250", {"start": v(13.26, 14.97) * mm, "end": v(13.82, 14.46) * mm});
            skArc(sketch, "E251", {"start": v(13.3, 13.17) * mm, "mid": v(13.6, 13.8) * mm, "end": v(13.82, 14.46) * mm});
            skArc(sketch, "E252", {"start": v(12.74, 12.36) * mm, "mid": v(12.88, 11.85) * mm, "end": v(13.37, 11.67) * mm});
            skArc(sketch, "E253", {"start": v(12.96, 12.62) * mm, "mid": v(13.14, 12.88) * mm, "end": v(13.3, 13.17) * mm});
            skArc(sketch, "E254", {"start": v(12.74, 12.36) * mm, "mid": v(12.85, 12.49) * mm, "end": v(12.96, 12.62) * mm});
            skArc(sketch, "E255", {"start": v(13.64, 11.87) * mm, "mid": v(13.5, 11.78) * mm, "end": v(13.37, 11.67) * mm});
            skArc(sketch, "E256", {"start": v(14.22, 12.17) * mm, "mid": v(13.93, 12.03) * mm, "end": v(13.64, 11.87) * mm});
            skArc(sketch, "E257", {"start": v(15.55, 12.58) * mm, "mid": v(14.87, 12.4) * mm, "end": v(14.22, 12.17) * mm});
            skLineSegment(sketch, "E258", {"start": v(10.62, 16.95) * mm, "end": v(11.25, 16.53) * mm});
            skArc(sketch, "E259", {"start": v(10.95, 15.18) * mm, "mid": v(11.14, 15.85) * mm, "end": v(11.25, 16.53) * mm});
            skArc(sketch, "E260", {"start": v(10.53, 14.3) * mm, "mid": v(10.75, 13.81) * mm, "end": v(11.27, 13.71) * mm});
            skArc(sketch, "E261", {"start": v(10.7, 14.58) * mm, "mid": v(10.84, 14.87) * mm, "end": v(10.95, 15.18) * mm});
            skArc(sketch, "E262", {"start": v(10.53, 14.3) * mm, "mid": v(10.62, 14.43) * mm, "end": v(10.7, 14.58) * mm});
            skArc(sketch, "E263", {"start": v(11.5, 13.95) * mm, "mid": v(11.38, 13.84) * mm, "end": v(11.27, 13.71) * mm});
            skArc(sketch, "E264", {"start": v(12.02, 14.34) * mm, "mid": v(11.76, 14.16) * mm, "end": v(11.5, 13.95) * mm});
            skArc(sketch, "E265", {"start": v(13.26, 14.97) * mm, "mid": v(12.63, 14.69) * mm, "end": v(12.02, 14.34) * mm});
            skLineSegment(sketch, "E266", {"start": v(7.69, 18.46) * mm, "end": v(8.38, 18.16) * mm});
            skArc(sketch, "E267", {"start": v(8.3, 16.77) * mm, "mid": v(8.38, 17.46) * mm, "end": v(8.38, 18.16) * mm});
            skArc(sketch, "E268", {"start": v(8.03, 15.83) * mm, "mid": v(8.33, 15.4) * mm, "end": v(8.86, 15.38) * mm});
            skArc(sketch, "E269", {"start": v(8.16, 16.14) * mm, "mid": v(8.24, 16.45) * mm, "end": v(8.3, 16.77) * mm});
            skArc(sketch, "E270", {"start": v(8.03, 15.83) * mm, "mid": v(8.1, 15.98) * mm, "end": v(8.16, 16.14) * mm});
            skArc(sketch, "E271", {"start": v(9.05, 15.66) * mm, "mid": v(8.95, 15.52) * mm, "end": v(8.86, 15.38) * mm});
            skArc(sketch, "E272", {"start": v(9.5, 16.13) * mm, "mid": v(9.26, 15.9) * mm, "end": v(9.05, 15.66) * mm});
            skArc(sketch, "E273", {"start": v(10.62, 16.95) * mm, "mid": v(10.04, 16.57) * mm, "end": v(9.5, 16.13) * mm});
            skLineSegment(sketch, "E274", {"start": v(4.54, 19.48) * mm, "end": v(5.28, 19.3) * mm});
            skArc(sketch, "E275", {"start": v(5.43, 17.9) * mm, "mid": v(5.4, 18.6) * mm, "end": v(5.28, 19.3) * mm});
            skArc(sketch, "E276", {"start": v(5.32, 16.93) * mm, "mid": v(5.68, 16.55) * mm, "end": v(6.2, 16.63) * mm});
            skArc(sketch, "E277", {"start": v(5.39, 17.26) * mm, "mid": v(5.42, 17.59) * mm, "end": v(5.43, 17.9) * mm});
            skArc(sketch, "E278", {"start": v(5.32, 16.93) * mm, "mid": v(5.36, 17.1) * mm, "end": v(5.39, 17.26) * mm});
            skArc(sketch, "E279", {"start": v(6.35, 16.93) * mm, "mid": v(6.27, 16.78) * mm, "end": v(6.2, 16.63) * mm});
            skArc(sketch, "E280", {"start": v(6.71, 17.47) * mm, "mid": v(6.52, 17.2) * mm, "end": v(6.35, 16.93) * mm});
            skArc(sketch, "E281", {"start": v(7.69, 18.46) * mm, "mid": v(7.17, 18) * mm, "end": v(6.71, 17.47) * mm});
            skLineSegment(sketch, "E282", {"start": v(1.27, 19.96) * mm, "end": v(2.03, 19.9) * mm});
            skArc(sketch, "E283", {"start": v(2.4, 18.56) * mm, "mid": v(2.25, 19.24) * mm, "end": v(2.03, 19.9) * mm});
            skArc(sketch, "E284", {"start": v(2.46, 17.58) * mm, "mid": v(2.88, 17.26) * mm, "end": v(3.38, 17.42) * mm});
            skArc(sketch, "E285", {"start": v(2.47, 17.92) * mm, "mid": v(2.46, 18.24) * mm, "end": v(2.4, 18.56) * mm});
            skArc(sketch, "E286", {"start": v(2.46, 17.58) * mm, "mid": v(2.47, 17.75) * mm, "end": v(2.47, 17.92) * mm});
            skArc(sketch, "E287", {"start": v(3.48, 17.75) * mm, "mid": v(3.43, 17.59) * mm, "end": v(3.38, 17.42) * mm});
            skArc(sketch, "E288", {"start": v(3.75, 18.34) * mm, "mid": v(3.6, 18.05) * mm, "end": v(3.48, 17.75) * mm});
            skArc(sketch, "E289", {"start": v(4.54, 19.48) * mm, "mid": v(4.11, 18.93) * mm, "end": v(3.75, 18.34) * mm});
            skLineSegment(sketch, "E290", {"start": v(-2.03, 19.9) * mm, "end": v(-1.27, 19.96) * mm});
            skArc(sketch, "E291", {"start": v(-0.68, 18.7) * mm, "mid": v(-0.94, 19.35) * mm, "end": v(-1.27, 19.96) * mm});
            skArc(sketch, "E292", {"start": v(-0.47, 17.74) * mm, "mid": v(0, 17.5) * mm, "end": v(0.47, 17.74) * mm});
            skArc(sketch, "E293", {"start": v(-0.5, 18.08) * mm, "mid": v(-0.58, 18.4) * mm, "end": v(-0.68, 18.7) * mm});
            skArc(sketch, "E294", {"start": v(-0.47, 17.74) * mm, "mid": v(-0.48, 17.91) * mm, "end": v(-0.5, 18.08) * mm});
            skArc(sketch, "E295", {"start": v(0.5, 18.08) * mm, "mid": v(0.48, 17.91) * mm, "end": v(0.47, 17.74) * mm});
            skArc(sketch, "E296", {"start": v(0.68, 18.7) * mm, "mid": v(0.58, 18.4) * mm, "end": v(0.5, 18.08) * mm});
            skArc(sketch, "E297", {"start": v(1.27, 19.96) * mm, "mid": v(0.94, 19.35) * mm, "end": v(0.68, 18.7) * mm});
            skLineSegment(sketch, "E298", {"start": v(-5.28, 19.3) * mm, "end": v(-4.54, 19.48) * mm});
            skArc(sketch, "E299", {"start": v(-3.75, 18.34) * mm, "mid": v(-4.11, 18.93) * mm, "end": v(-4.54, 19.48) * mm});
            skArc(sketch, "E300", {"start": v(-3.38, 17.42) * mm, "mid": v(-2.88, 17.26) * mm, "end": v(-2.46, 17.58) * mm});
            skArc(sketch, "E301", {"start": v(-3.48, 17.75) * mm, "mid": v(-3.6, 18.05) * mm, "end": v(-3.75, 18.34) * mm});
            skArc(sketch, "E302", {"start": v(-3.38, 17.42) * mm, "mid": v(-3.43, 17.59) * mm, "end": v(-3.48, 17.75) * mm});
            skArc(sketch, "E303", {"start": v(-2.47, 17.92) * mm, "mid": v(-2.47, 17.75) * mm, "end": v(-2.46, 17.58) * mm});
            skArc(sketch, "E304", {"start": v(-2.41, 18.56) * mm, "mid": v(-2.46, 18.24) * mm, "end": v(-2.47, 17.92) * mm});
            skArc(sketch, "E305", {"start": v(-2.03, 19.9) * mm, "mid": v(-2.25, 19.24) * mm, "end": v(-2.41, 18.56) * mm});
            skLineSegment(sketch, "E306", {"start": v(-0.04, 2.42) * mm, "end": v(-0.15, 2.4) * mm});
            skLineSegment(sketch, "E307", {"start": v(0.18, 2.9) * mm, "end": v(0.1, 2.9) * mm});
            skArc(sketch, "E308", {"start": v(0.1, 2.9) * mm, "mid": v(0.02, 2.73) * mm, "end": v(-0.04, 2.55) * mm});
            skLineSegment(sketch, "E309", {"start": v(-0.04, 2.42) * mm, "end": v(-0.04, 2.53) * mm});
            skArc(sketch, "E310", {"start": v(-0.04, 2.55) * mm, "mid": v(-0.04, 2.54) * mm, "end": v(-0.04, 2.53) * mm});
            skLineSegment(sketch, "E311", {"start": v(0.34, 2.4) * mm, "end": v(0.45, 2.37) * mm});
            skLineSegment(sketch, "E312", {"start": v(0.18, 2.9) * mm, "end": v(0.26, 2.89) * mm});
            skArc(sketch, "E313", {"start": v(0.35, 2.53) * mm, "mid": v(0.32, 2.71) * mm, "end": v(0.26, 2.89) * mm});
            skLineSegment(sketch, "E314", {"start": v(0.34, 2.4) * mm, "end": v(0.35, 2.5) * mm});
            skArc(sketch, "E315", {"start": v(0.35, 2.5) * mm, "mid": v(0.35, 2.51) * mm, "end": v(0.35, 2.53) * mm});
            skLineSegment(sketch, "E316", {"start": v(-0.64, 2.33) * mm, "end": v(-0.75, 2.3) * mm});
            skLineSegment(sketch, "E317", {"start": v(-0.54, 2.85) * mm, "end": v(-0.62, 2.83) * mm});
            skArc(sketch, "E318", {"start": v(-0.62, 2.83) * mm, "mid": v(-0.66, 2.65) * mm, "end": v(-0.67, 2.46) * mm});
            skArc(sketch, "E319", {"start": v(-0.28, 2.51) * mm, "mid": v(-0.28, 2.52) * mm, "end": v(-0.28, 2.54) * mm});
            skLineSegment(sketch, "E320", {"start": v(-0.64, 2.33) * mm, "end": v(-0.66, 2.44) * mm});
            skArc(sketch, "E321", {"start": v(-0.67, 2.46) * mm, "mid": v(-0.67, 2.45) * mm, "end": v(-0.66, 2.44) * mm});
            skLineSegment(sketch, "E322", {"start": v(-0.27, 2.4) * mm, "end": v(-0.28, 2.51) * mm});
            skArc(sketch, "E323", {"start": v(-0.28, 2.54) * mm, "mid": v(-0.36, 2.7) * mm, "end": v(-0.47, 2.86) * mm});
            skLineSegment(sketch, "E324", {"start": v(-0.54, 2.85) * mm, "end": v(-0.47, 2.86) * mm});
            skLineSegment(sketch, "E325", {"start": v(-0.27, 2.4) * mm, "end": v(-0.15, 2.4) * mm});
            skLineSegment(sketch, "E326", {"start": v(-1.2, 2.1) * mm, "end": v(-1.3, 2.04) * mm});
            skLineSegment(sketch, "E327", {"start": v(-1.23, 2.62) * mm, "end": v(-1.3, 2.6) * mm});
            skArc(sketch, "E328", {"start": v(-1.3, 2.6) * mm, "mid": v(-1.3, 2.4) * mm, "end": v(-1.26, 2.22) * mm});
            skArc(sketch, "E329", {"start": v(-0.9, 2.36) * mm, "mid": v(-0.9, 2.37) * mm, "end": v(-0.9, 2.39) * mm});
            skLineSegment(sketch, "E330", {"start": v(-1.2, 2.1) * mm, "end": v(-1.25, 2.2) * mm});
            skArc(sketch, "E331", {"start": v(-1.26, 2.22) * mm, "mid": v(-1.26, 2.2) * mm, "end": v(-1.25, 2.2) * mm});
            skLineSegment(sketch, "E332", {"start": v(-0.86, 2.26) * mm, "end": v(-0.9, 2.36) * mm});
            skArc(sketch, "E333", {"start": v(-0.9, 2.39) * mm, "mid": v(-1.02, 2.53) * mm, "end": v(-1.16, 2.66) * mm});
            skLineSegment(sketch, "E334", {"start": v(-1.23, 2.62) * mm, "end": v(-1.16, 2.66) * mm});
            skLineSegment(sketch, "E335", {"start": v(-0.86, 2.26) * mm, "end": v(-0.75, 2.3) * mm});
            skLineSegment(sketch, "E336", {"start": v(-1.68, 1.74) * mm, "end": v(-1.76, 1.65) * mm});
            skLineSegment(sketch, "E337", {"start": v(-1.85, 2.23) * mm, "end": v(-1.9, 2.19) * mm});
            skArc(sketch, "E338", {"start": v(-1.9, 2.19) * mm, "mid": v(-1.86, 2) * mm, "end": v(-1.77, 1.84) * mm});
            skArc(sketch, "E339", {"start": v(-1.45, 2.07) * mm, "mid": v(-1.46, 2.08) * mm, "end": v(-1.47, 2.09) * mm});
            skLineSegment(sketch, "E340", {"start": v(-1.68, 1.74) * mm, "end": v(-1.76, 1.82) * mm});
            skArc(sketch, "E341", {"start": v(-1.77, 1.84) * mm, "mid": v(-1.76, 1.83) * mm, "end": v(-1.76, 1.82) * mm});
            skLineSegment(sketch, "E342", {"start": v(-1.4, 1.98) * mm, "end": v(-1.45, 2.07) * mm});
            skArc(sketch, "E343", {"start": v(-1.47, 2.09) * mm, "mid": v(-1.62, 2.2) * mm, "end": v(-1.79, 2.28) * mm});
            skLineSegment(sketch, "E344", {"start": v(-1.85, 2.23) * mm, "end": v(-1.79, 2.28) * mm});
            skLineSegment(sketch, "E345", {"start": v(-1.4, 1.98) * mm, "end": v(-1.3, 2.04) * mm});
            skLineSegment(sketch, "E346", {"start": v(-2.06, 1.26) * mm, "end": v(-2.12, 1.16) * mm});
            skLineSegment(sketch, "E347", {"start": v(-2.35, 1.7) * mm, "end": v(-2.4, 1.64) * mm});
            skArc(sketch, "E348", {"start": v(-2.4, 1.64) * mm, "mid": v(-2.3, 1.48) * mm, "end": v(-2.17, 1.34) * mm});
            skArc(sketch, "E349", {"start": v(-1.92, 1.64) * mm, "mid": v(-1.93, 1.65) * mm, "end": v(-1.94, 1.65) * mm});
            skLineSegment(sketch, "E350", {"start": v(-2.06, 1.26) * mm, "end": v(-2.15, 1.32) * mm});
            skArc(sketch, "E351", {"start": v(-2.17, 1.34) * mm, "mid": v(-2.16, 1.33) * mm, "end": v(-2.15, 1.32) * mm});
            skLineSegment(sketch, "E352", {"start": v(-1.84, 1.57) * mm, "end": v(-1.92, 1.64) * mm});
            skArc(sketch, "E353", {"start": v(-1.94, 1.65) * mm, "mid": v(-2.12, 1.73) * mm, "end": v(-2.3, 1.77) * mm});
            skLineSegment(sketch, "E354", {"start": v(-2.35, 1.7) * mm, "end": v(-2.3, 1.77) * mm});
            skLineSegment(sketch, "E355", {"start": v(-1.84, 1.57) * mm, "end": v(-1.76, 1.65) * mm});
            skLineSegment(sketch, "E356", {"start": v(-2.31, 0.71) * mm, "end": v(-2.34, 0.6) * mm});
            skLineSegment(sketch, "E357", {"start": v(-2.7, 1.07) * mm, "end": v(-2.72, 1) * mm});
            skArc(sketch, "E358", {"start": v(-2.72, 1) * mm, "mid": v(-2.6, 0.86) * mm, "end": v(-2.44, 0.75) * mm});
            skArc(sketch, "E359", {"start": v(-2.27, 1.1) * mm, "mid": v(-2.28, 1.11) * mm, "end": v(-2.3, 1.12) * mm});
            skLineSegment(sketch, "E360", {"start": v(-2.31, 0.71) * mm, "end": v(-2.41, 0.74) * mm});
            skArc(sketch, "E361", {"start": v(-2.44, 0.75) * mm, "mid": v(-2.43, 0.75) * mm, "end": v(-2.41, 0.74) * mm});
            skLineSegment(sketch, "E362", {"start": v(-2.17, 1.06) * mm, "end": v(-2.27, 1.1) * mm});
            skArc(sketch, "E363", {"start": v(-2.3, 1.12) * mm, "mid": v(-2.48, 1.15) * mm, "end": v(-2.67, 1.14) * mm});
            skLineSegment(sketch, "E364", {"start": v(-2.7, 1.07) * mm, "end": v(-2.67, 1.14) * mm});
            skLineSegment(sketch, "E365", {"start": v(-2.17, 1.06) * mm, "end": v(-2.12, 1.16) * mm});
            skLineSegment(sketch, "E366", {"start": v(-2.41, 0.12) * mm, "end": v(-2.41, 0) * mm});
            skLineSegment(sketch, "E367", {"start": v(-2.88, 0.36) * mm, "end": v(-2.89, 0.29) * mm});
            skArc(sketch, "E368", {"start": v(-2.89, 0.29) * mm, "mid": v(-2.73, 0.2) * mm, "end": v(-2.55, 0.13) * mm});
            skArc(sketch, "E369", {"start": v(-2.47, 0.51) * mm, "mid": v(-2.49, 0.51) * mm, "end": v(-2.5, 0.51) * mm});
            skLineSegment(sketch, "E370", {"start": v(-2.41, 0.12) * mm, "end": v(-2.52, 0.12) * mm});
            skArc(sketch, "E371", {"start": v(-2.55, 0.13) * mm, "mid": v(-2.54, 0.12) * mm, "end": v(-2.52, 0.12) * mm});
            skLineSegment(sketch, "E372", {"start": v(-2.37, 0.49) * mm, "end": v(-2.47, 0.51) * mm});
            skArc(sketch, "E373", {"start": v(-2.5, 0.51) * mm, "mid": v(-2.69, 0.5) * mm, "end": v(-2.87, 0.44) * mm});
            skLineSegment(sketch, "E374", {"start": v(-2.88, 0.36) * mm, "end": v(-2.87, 0.44) * mm});
            skLineSegment(sketch, "E375", {"start": v(-2.37, 0.49) * mm, "end": v(-2.34, 0.6) * mm});
            skLineSegment(sketch, "E376", {"start": v(-2.37, -0.49) * mm, "end": v(-2.34, -0.6) * mm});
            skLineSegment(sketch, "E377", {"start": v(-2.88, -0.36) * mm, "end": v(-2.87, -0.44) * mm});
            skArc(sketch, "E378", {"start": v(-2.87, -0.44) * mm, "mid": v(-2.69, -0.5) * mm, "end": v(-2.5, -0.51) * mm});
            skArc(sketch, "E379", {"start": v(-2.52, -0.12) * mm, "mid": v(-2.54, -0.12) * mm, "end": v(-2.55, -0.13) * mm});
            skLineSegment(sketch, "E380", {"start": v(-2.37, -0.49) * mm, "end": v(-2.47, -0.51) * mm});
            skArc(sketch, "E381", {"start": v(-2.5, -0.51) * mm, "mid": v(-2.49, -0.51) * mm, "end": v(-2.47, -0.51) * mm});
            skLineSegment(sketch, "E382", {"start": v(-2.41, -0.12) * mm, "end": v(-2.52, -0.12) * mm});
            skArc(sketch, "E383", {"start": v(-2.55, -0.13) * mm, "mid": v(-2.73, -0.2) * mm, "end": v(-2.89, -0.29) * mm});
            skLineSegment(sketch, "E384", {"start": v(-2.88, -0.36) * mm, "end": v(-2.89, -0.29) * mm});
            skLineSegment(sketch, "E385", {"start": v(-2.41, -0.12) * mm, "end": v(-2.41, 0) * mm});
            skLineSegment(sketch, "E386", {"start": v(-2.17, -1.06) * mm, "end": v(-2.12, -1.16) * mm});
            skLineSegment(sketch, "E387", {"start": v(-2.7, -1.07) * mm, "end": v(-2.67, -1.14) * mm});
            skArc(sketch, "E388", {"start": v(-2.67, -1.14) * mm, "mid": v(-2.48, -1.15) * mm, "end": v(-2.3, -1.12) * mm});
            skArc(sketch, "E389", {"start": v(-2.41, -0.74) * mm, "mid": v(-2.43, -0.75) * mm, "end": v(-2.44, -0.75) * mm});
            skLineSegment(sketch, "E390", {"start": v(-2.17, -1.06) * mm, "end": v(-2.27, -1.1) * mm});
            skArc(sketch, "E391", {"start": v(-2.3, -1.12) * mm, "mid": v(-2.28, -1.11) * mm, "end": v(-2.27, -1.1) * mm});
            skLineSegment(sketch, "E392", {"start": v(-2.31, -0.71) * mm, "end": v(-2.41, -0.74) * mm});
            skArc(sketch, "E393", {"start": v(-2.44, -0.75) * mm, "mid": v(-2.6, -0.86) * mm, "end": v(-2.72, -1) * mm});
            skLineSegment(sketch, "E394", {"start": v(-2.7, -1.07) * mm, "end": v(-2.72, -1) * mm});
            skLineSegment(sketch, "E395", {"start": v(-2.31, -0.71) * mm, "end": v(-2.34, -0.6) * mm});
            skLineSegment(sketch, "E396", {"start": v(-1.84, -1.57) * mm, "end": v(-1.76, -1.65) * mm});
            skLineSegment(sketch, "E397", {"start": v(-2.35, -1.7) * mm, "end": v(-2.3, -1.77) * mm});
            skArc(sketch, "E398", {"start": v(-2.3, -1.77) * mm, "mid": v(-2.12, -1.73) * mm, "end": v(-1.94, -1.65) * mm});
            skArc(sketch, "E399", {"start": v(-2.15, -1.32) * mm, "mid": v(-2.16, -1.33) * mm, "end": v(-2.17, -1.34) * mm});
            skLineSegment(sketch, "E400", {"start": v(-1.84, -1.57) * mm, "end": v(-1.92, -1.64) * mm});
            skArc(sketch, "E401", {"start": v(-1.94, -1.65) * mm, "mid": v(-1.93, -1.65) * mm, "end": v(-1.92, -1.64) * mm});
            skLineSegment(sketch, "E402", {"start": v(-2.06, -1.26) * mm, "end": v(-2.15, -1.32) * mm});
            skArc(sketch, "E403", {"start": v(-2.17, -1.34) * mm, "mid": v(-2.3, -1.48) * mm, "end": v(-2.4, -1.64) * mm});
            skLineSegment(sketch, "E404", {"start": v(-2.35, -1.7) * mm, "end": v(-2.4, -1.64) * mm});
            skLineSegment(sketch, "E405", {"start": v(-2.06, -1.26) * mm, "end": v(-2.12, -1.16) * mm});
            skLineSegment(sketch, "E406", {"start": v(-1.4, -1.98) * mm, "end": v(-1.3, -2.04) * mm});
            skLineSegment(sketch, "E407", {"start": v(-1.85, -2.23) * mm, "end": v(-1.79, -2.28) * mm});
            skArc(sketch, "E408", {"start": v(-1.79, -2.28) * mm, "mid": v(-1.62, -2.2) * mm, "end": v(-1.47, -2.09) * mm});
            skArc(sketch, "E409", {"start": v(-1.76, -1.82) * mm, "mid": v(-1.76, -1.83) * mm, "end": v(-1.77, -1.84) * mm});
            skLineSegment(sketch, "E410", {"start": v(-1.4, -1.98) * mm, "end": v(-1.45, -2.07) * mm});
            skArc(sketch, "E411", {"start": v(-1.47, -2.09) * mm, "mid": v(-1.46, -2.08) * mm, "end": v(-1.45, -2.07) * mm});
            skLineSegment(sketch, "E412", {"start": v(-1.68, -1.74) * mm, "end": v(-1.76, -1.82) * mm});
            skArc(sketch, "E413", {"start": v(-1.77, -1.84) * mm, "mid": v(-1.86, -2) * mm, "end": v(-1.9, -2.19) * mm});
            skLineSegment(sketch, "E414", {"start": v(-1.85, -2.23) * mm, "end": v(-1.9, -2.19) * mm});
            skLineSegment(sketch, "E415", {"start": v(-1.68, -1.74) * mm, "end": v(-1.76, -1.65) * mm});
            skLineSegment(sketch, "E416", {"start": v(-0.86, -2.26) * mm, "end": v(-0.75, -2.3) * mm});
            skLineSegment(sketch, "E417", {"start": v(-1.23, -2.62) * mm, "end": v(-1.16, -2.66) * mm});
            skArc(sketch, "E418", {"start": v(-1.16, -2.66) * mm, "mid": v(-1.02, -2.53) * mm, "end": v(-0.9, -2.39) * mm});
            skArc(sketch, "E419", {"start": v(-1.25, -2.2) * mm, "mid": v(-1.26, -2.2) * mm, "end": v(-1.26, -2.22) * mm});
            skLineSegment(sketch, "E420", {"start": v(-0.86, -2.26) * mm, "end": v(-0.9, -2.36) * mm});
            skArc(sketch, "E421", {"start": v(-0.9, -2.39) * mm, "mid": v(-0.9, -2.37) * mm, "end": v(-0.9, -2.36) * mm});
            skLineSegment(sketch, "E422", {"start": v(-1.2, -2.1) * mm, "end": v(-1.25, -2.2) * mm});
            skArc(sketch, "E423", {"start": v(-1.26, -2.22) * mm, "mid": v(-1.3, -2.4) * mm, "end": v(-1.3, -2.6) * mm});
            skLineSegment(sketch, "E424", {"start": v(-1.23, -2.62) * mm, "end": v(-1.3, -2.6) * mm});
            skLineSegment(sketch, "E425", {"start": v(-1.2, -2.1) * mm, "end": v(-1.3, -2.04) * mm});
            skLineSegment(sketch, "E426", {"start": v(-0.27, -2.4) * mm, "end": v(-0.15, -2.4) * mm});
            skLineSegment(sketch, "E427", {"start": v(-0.54, -2.85) * mm, "end": v(-0.47, -2.86) * mm});
            skArc(sketch, "E428", {"start": v(-0.47, -2.86) * mm, "mid": v(-0.36, -2.7) * mm, "end": v(-0.28, -2.54) * mm});
            skArc(sketch, "E429", {"start": v(-0.66, -2.44) * mm, "mid": v(-0.67, -2.45) * mm, "end": v(-0.67, -2.46) * mm});
            skLineSegment(sketch, "E430", {"start": v(-0.27, -2.4) * mm, "end": v(-0.28, -2.51) * mm});
            skArc(sketch, "E431", {"start": v(-0.28, -2.54) * mm, "mid": v(-0.28, -2.52) * mm, "end": v(-0.28, -2.51) * mm});
            skLineSegment(sketch, "E432", {"start": v(-0.64, -2.33) * mm, "end": v(-0.66, -2.44) * mm});
            skArc(sketch, "E433", {"start": v(-0.67, -2.46) * mm, "mid": v(-0.66, -2.65) * mm, "end": v(-0.62, -2.83) * mm});
            skLineSegment(sketch, "E434", {"start": v(-0.54, -2.85) * mm, "end": v(-0.62, -2.83) * mm});
            skLineSegment(sketch, "E435", {"start": v(-0.64, -2.33) * mm, "end": v(-0.75, -2.3) * mm});
            skLineSegment(sketch, "E436", {"start": v(0.34, -2.4) * mm, "end": v(0.45, -2.37) * mm});
            skLineSegment(sketch, "E437", {"start": v(0.18, -2.9) * mm, "end": v(0.26, -2.89) * mm});
            skArc(sketch, "E438", {"start": v(0.26, -2.89) * mm, "mid": v(0.32, -2.71) * mm, "end": v(0.35, -2.53) * mm});
            skArc(sketch, "E439", {"start": v(-0.04, -2.53) * mm, "mid": v(-0.04, -2.54) * mm, "end": v(-0.04, -2.55) * mm});
            skLineSegment(sketch, "E440", {"start": v(0.34, -2.4) * mm, "end": v(0.35, -2.5) * mm});
            skArc(sketch, "E441", {"start": v(0.35, -2.53) * mm, "mid": v(0.35, -2.51) * mm, "end": v(0.35, -2.5) * mm});
            skLineSegment(sketch, "E442", {"start": v(-0.04, -2.42) * mm, "end": v(-0.04, -2.53) * mm});
            skArc(sketch, "E443", {"start": v(-0.04, -2.55) * mm, "mid": v(0.02, -2.73) * mm, "end": v(0.1, -2.9) * mm});
            skLineSegment(sketch, "E444", {"start": v(0.18, -2.9) * mm, "end": v(0.1, -2.9) * mm});
            skLineSegment(sketch, "E445", {"start": v(-0.04, -2.42) * mm, "end": v(-0.15, -2.4) * mm});
            skLineSegment(sketch, "E446", {"start": v(0.92, -2.23) * mm, "end": v(1.03, -2.18) * mm});
            skLineSegment(sketch, "E447", {"start": v(0.9, -2.76) * mm, "end": v(0.97, -2.73) * mm});
            skArc(sketch, "E448", {"start": v(0.97, -2.73) * mm, "mid": v(0.99, -2.55) * mm, "end": v(0.97, -2.36) * mm});
            skArc(sketch, "E449", {"start": v(0.6, -2.46) * mm, "mid": v(0.6, -2.47) * mm, "end": v(0.6, -2.48) * mm});
            skLineSegment(sketch, "E450", {"start": v(0.92, -2.23) * mm, "end": v(0.96, -2.33) * mm});
            skArc(sketch, "E451", {"start": v(0.97, -2.36) * mm, "mid": v(0.97, -2.35) * mm, "end": v(0.96, -2.33) * mm});
            skLineSegment(sketch, "E452", {"start": v(0.57, -2.35) * mm, "end": v(0.6, -2.46) * mm});
            skArc(sketch, "E453", {"start": v(0.6, -2.48) * mm, "mid": v(0.7, -2.64) * mm, "end": v(0.82, -2.78) * mm});
            skLineSegment(sketch, "E454", {"start": v(0.9, -2.76) * mm, "end": v(0.82, -2.78) * mm});
            skLineSegment(sketch, "E455", {"start": v(0.57, -2.35) * mm, "end": v(0.45, -2.37) * mm});
            skLineSegment(sketch, "E456", {"start": v(1.45, -1.93) * mm, "end": v(1.54, -1.86) * mm});
            skLineSegment(sketch, "E457", {"start": v(1.55, -2.45) * mm, "end": v(1.62, -2.4) * mm});
            skArc(sketch, "E458", {"start": v(1.62, -2.4) * mm, "mid": v(1.6, -2.22) * mm, "end": v(1.53, -2.04) * mm});
            skArc(sketch, "E459", {"start": v(1.18, -2.23) * mm, "mid": v(1.2, -2.24) * mm, "end": v(1.2, -2.25) * mm});
            skLineSegment(sketch, "E460", {"start": v(1.45, -1.93) * mm, "end": v(1.51, -2.02) * mm});
            skArc(sketch, "E461", {"start": v(1.53, -2.04) * mm, "mid": v(1.52, -2.03) * mm, "end": v(1.51, -2.02) * mm});
            skLineSegment(sketch, "E462", {"start": v(1.13, -2.14) * mm, "end": v(1.18, -2.23) * mm});
            skArc(sketch, "E463", {"start": v(1.2, -2.25) * mm, "mid": v(1.33, -2.38) * mm, "end": v(1.49, -2.49) * mm});
            skLineSegment(sketch, "E464", {"start": v(1.55, -2.45) * mm, "end": v(1.49, -2.49) * mm});
            skLineSegment(sketch, "E465", {"start": v(1.13, -2.14) * mm, "end": v(1.03, -2.18) * mm});
            skLineSegment(sketch, "E466", {"start": v(1.89, -1.51) * mm, "end": v(1.95, -1.42) * mm});
            skLineSegment(sketch, "E467", {"start": v(2.11, -1.99) * mm, "end": v(2.17, -1.93) * mm});
            skArc(sketch, "E468", {"start": v(2.17, -1.93) * mm, "mid": v(2.1, -1.76) * mm, "end": v(1.99, -1.6) * mm});
            skArc(sketch, "E469", {"start": v(1.7, -1.87) * mm, "mid": v(1.71, -1.88) * mm, "end": v(1.72, -1.88) * mm});
            skLineSegment(sketch, "E470", {"start": v(1.89, -1.51) * mm, "end": v(1.97, -1.58) * mm});
            skArc(sketch, "E471", {"start": v(1.99, -1.6) * mm, "mid": v(1.98, -1.59) * mm, "end": v(1.97, -1.58) * mm});
            skLineSegment(sketch, "E472", {"start": v(1.63, -1.79) * mm, "end": v(1.7, -1.87) * mm});
            skArc(sketch, "E473", {"start": v(1.72, -1.88) * mm, "mid": v(1.88, -1.98) * mm, "end": v(2.06, -2.04) * mm});
            skLineSegment(sketch, "E474", {"start": v(2.11, -1.99) * mm, "end": v(2.06, -2.04) * mm});
            skLineSegment(sketch, "E475", {"start": v(1.63, -1.79) * mm, "end": v(1.54, -1.86) * mm});
            skLineSegment(sketch, "E476", {"start": v(2.2, -1) * mm, "end": v(2.25, -0.89) * mm});
            skLineSegment(sketch, "E477", {"start": v(2.54, -1.4) * mm, "end": v(2.58, -1.33) * mm});
            skArc(sketch, "E478", {"start": v(2.58, -1.33) * mm, "mid": v(2.46, -1.18) * mm, "end": v(2.32, -1.05) * mm});
            skArc(sketch, "E479", {"start": v(2.11, -1.38) * mm, "mid": v(2.12, -1.4) * mm, "end": v(2.14, -1.4) * mm});
            skLineSegment(sketch, "E480", {"start": v(2.2, -1) * mm, "end": v(2.3, -1.04) * mm});
            skArc(sketch, "E481", {"start": v(2.32, -1.05) * mm, "mid": v(2.31, -1.05) * mm, "end": v(2.3, -1.04) * mm});
            skLineSegment(sketch, "E482", {"start": v(2.02, -1.33) * mm, "end": v(2.11, -1.38) * mm});
            skArc(sketch, "E483", {"start": v(2.14, -1.4) * mm, "mid": v(2.32, -1.45) * mm, "end": v(2.5, -1.46) * mm});
            skLineSegment(sketch, "E484", {"start": v(2.54, -1.4) * mm, "end": v(2.5, -1.46) * mm});
            skLineSegment(sketch, "E485", {"start": v(2.02, -1.33) * mm, "end": v(1.95, -1.42) * mm});
            skLineSegment(sketch, "E486", {"start": v(2.38, -0.42) * mm, "end": v(2.4, -0.3) * mm});
            skLineSegment(sketch, "E487", {"start": v(2.8, -0.72) * mm, "end": v(2.83, -0.65) * mm});
            skArc(sketch, "E488", {"start": v(2.83, -0.65) * mm, "mid": v(2.68, -0.53) * mm, "end": v(2.51, -0.44) * mm});
            skArc(sketch, "E489", {"start": v(2.4, -0.82) * mm, "mid": v(2.4, -0.82) * mm, "end": v(2.42, -0.82) * mm});
            skLineSegment(sketch, "E490", {"start": v(2.38, -0.42) * mm, "end": v(2.49, -0.44) * mm});
            skArc(sketch, "E491", {"start": v(2.51, -0.44) * mm, "mid": v(2.5, -0.44) * mm, "end": v(2.49, -0.44) * mm});
            skLineSegment(sketch, "E492", {"start": v(2.29, -0.78) * mm, "end": v(2.4, -0.82) * mm});
            skArc(sketch, "E493", {"start": v(2.42, -0.82) * mm, "mid": v(2.6, -0.83) * mm, "end": v(2.79, -0.8) * mm});
            skLineSegment(sketch, "E494", {"start": v(2.8, -0.72) * mm, "end": v(2.79, -0.8) * mm});
            skLineSegment(sketch, "E495", {"start": v(2.29, -0.78) * mm, "end": v(2.25, -0.89) * mm});
            skLineSegment(sketch, "E496", {"start": v(2.41, 0.19) * mm, "end": v(2.4, 0.3) * mm});
            skLineSegment(sketch, "E497", {"start": v(2.9, 0) * mm, "end": v(2.9, 0.08) * mm});
            skArc(sketch, "E498", {"start": v(2.9, 0.08) * mm, "mid": v(2.73, 0.15) * mm, "end": v(2.54, 0.2) * mm});
            skArc(sketch, "E499", {"start": v(2.52, -0.2) * mm, "mid": v(2.53, -0.2) * mm, "end": v(2.54, -0.2) * mm});
            skLineSegment(sketch, "E500", {"start": v(2.41, 0.19) * mm, "end": v(2.52, 0.2) * mm});
            skArc(sketch, "E501", {"start": v(2.54, 0.2) * mm, "mid": v(2.53, 0.2) * mm, "end": v(2.52, 0.2) * mm});
            skLineSegment(sketch, "E502", {"start": v(2.41, -0.19) * mm, "end": v(2.52, -0.2) * mm});
            skArc(sketch, "E503", {"start": v(2.54, -0.2) * mm, "mid": v(2.73, -0.15) * mm, "end": v(2.9, -0.08) * mm});
            skLineSegment(sketch, "E504", {"start": v(2.9, 0) * mm, "end": v(2.9, -0.08) * mm});
            skLineSegment(sketch, "E505", {"start": v(2.41, -0.19) * mm, "end": v(2.4, -0.3) * mm});
            skLineSegment(sketch, "E506", {"start": v(2.29, 0.78) * mm, "end": v(2.25, 0.89) * mm});
            skLineSegment(sketch, "E507", {"start": v(2.8, 0.72) * mm, "end": v(2.79, 0.8) * mm});
            skArc(sketch, "E508", {"start": v(2.79, 0.8) * mm, "mid": v(2.6, 0.83) * mm, "end": v(2.42, 0.82) * mm});
            skArc(sketch, "E509", {"start": v(2.49, 0.44) * mm, "mid": v(2.5, 0.44) * mm, "end": v(2.51, 0.44) * mm});
            skLineSegment(sketch, "E510", {"start": v(2.29, 0.78) * mm, "end": v(2.4, 0.82) * mm});
            skArc(sketch, "E511", {"start": v(2.42, 0.82) * mm, "mid": v(2.4, 0.82) * mm, "end": v(2.4, 0.82) * mm});
            skLineSegment(sketch, "E512", {"start": v(2.38, 0.42) * mm, "end": v(2.49, 0.44) * mm});
            skArc(sketch, "E513", {"start": v(2.51, 0.44) * mm, "mid": v(2.68, 0.53) * mm, "end": v(2.83, 0.65) * mm});
            skLineSegment(sketch, "E514", {"start": v(2.8, 0.72) * mm, "end": v(2.83, 0.65) * mm});
            skLineSegment(sketch, "E515", {"start": v(2.38, 0.42) * mm, "end": v(2.4, 0.3) * mm});
            skLineSegment(sketch, "E516", {"start": v(2.02, 1.33) * mm, "end": v(1.95, 1.42) * mm});
            skLineSegment(sketch, "E517", {"start": v(2.54, 1.4) * mm, "end": v(2.5, 1.46) * mm});
            skArc(sketch, "E518", {"start": v(2.5, 1.46) * mm, "mid": v(2.32, 1.45) * mm, "end": v(2.14, 1.4) * mm});
            skArc(sketch, "E519", {"start": v(2.3, 1.04) * mm, "mid": v(2.31, 1.05) * mm, "end": v(2.32, 1.05) * mm});
            skLineSegment(sketch, "E520", {"start": v(2.02, 1.33) * mm, "end": v(2.11, 1.38) * mm});
            skArc(sketch, "E521", {"start": v(2.14, 1.4) * mm, "mid": v(2.12, 1.4) * mm, "end": v(2.11, 1.38) * mm});
            skLineSegment(sketch, "E522", {"start": v(2.2, 1) * mm, "end": v(2.3, 1.04) * mm});
            skArc(sketch, "E523", {"start": v(2.32, 1.05) * mm, "mid": v(2.46, 1.18) * mm, "end": v(2.58, 1.33) * mm});
            skLineSegment(sketch, "E524", {"start": v(2.54, 1.4) * mm, "end": v(2.58, 1.33) * mm});
            skLineSegment(sketch, "E525", {"start": v(2.2, 1) * mm, "end": v(2.25, 0.89) * mm});
            skLineSegment(sketch, "E526", {"start": v(1.63, 1.79) * mm, "end": v(1.54, 1.86) * mm});
            skLineSegment(sketch, "E527", {"start": v(2.11, 1.99) * mm, "end": v(2.06, 2.04) * mm});
            skArc(sketch, "E528", {"start": v(2.06, 2.04) * mm, "mid": v(1.88, 1.98) * mm, "end": v(1.72, 1.88) * mm});
            skArc(sketch, "E529", {"start": v(1.97, 1.58) * mm, "mid": v(1.98, 1.59) * mm, "end": v(1.99, 1.6) * mm});
            skLineSegment(sketch, "E530", {"start": v(1.63, 1.79) * mm, "end": v(1.7, 1.87) * mm});
            skArc(sketch, "E531", {"start": v(1.72, 1.88) * mm, "mid": v(1.71, 1.88) * mm, "end": v(1.7, 1.87) * mm});
            skLineSegment(sketch, "E532", {"start": v(1.89, 1.51) * mm, "end": v(1.97, 1.58) * mm});
            skArc(sketch, "E533", {"start": v(1.99, 1.6) * mm, "mid": v(2.1, 1.76) * mm, "end": v(2.17, 1.93) * mm});
            skLineSegment(sketch, "E534", {"start": v(2.11, 1.99) * mm, "end": v(2.17, 1.93) * mm});
            skLineSegment(sketch, "E535", {"start": v(1.89, 1.51) * mm, "end": v(1.95, 1.42) * mm});
            skLineSegment(sketch, "E536", {"start": v(1.13, 2.14) * mm, "end": v(1.03, 2.18) * mm});
            skLineSegment(sketch, "E537", {"start": v(1.55, 2.45) * mm, "end": v(1.49, 2.49) * mm});
            skArc(sketch, "E538", {"start": v(1.49, 2.49) * mm, "mid": v(1.33, 2.38) * mm, "end": v(1.2, 2.25) * mm});
            skArc(sketch, "E539", {"start": v(1.51, 2.02) * mm, "mid": v(1.52, 2.03) * mm, "end": v(1.53, 2.04) * mm});
            skLineSegment(sketch, "E540", {"start": v(1.13, 2.14) * mm, "end": v(1.18, 2.23) * mm});
            skArc(sketch, "E541", {"start": v(1.2, 2.25) * mm, "mid": v(1.2, 2.24) * mm, "end": v(1.18, 2.23) * mm});
            skLineSegment(sketch, "E542", {"start": v(1.45, 1.93) * mm, "end": v(1.51, 2.02) * mm});
            skArc(sketch, "E543", {"start": v(1.53, 2.04) * mm, "mid": v(1.6, 2.22) * mm, "end": v(1.62, 2.4) * mm});
            skLineSegment(sketch, "E544", {"start": v(1.55, 2.45) * mm, "end": v(1.62, 2.4) * mm});
            skLineSegment(sketch, "E545", {"start": v(1.45, 1.93) * mm, "end": v(1.54, 1.86) * mm});
            skLineSegment(sketch, "E546", {"start": v(0.57, 2.35) * mm, "end": v(0.45, 2.37) * mm});
            skLineSegment(sketch, "E547", {"start": v(0.9, 2.76) * mm, "end": v(0.82, 2.78) * mm});
            skArc(sketch, "E548", {"start": v(0.82, 2.78) * mm, "mid": v(0.7, 2.64) * mm, "end": v(0.6, 2.48) * mm});
            skArc(sketch, "E549", {"start": v(0.96, 2.33) * mm, "mid": v(0.97, 2.35) * mm, "end": v(0.97, 2.36) * mm});
            skLineSegment(sketch, "E550", {"start": v(0.57, 2.35) * mm, "end": v(0.6, 2.46) * mm});
            skArc(sketch, "E551", {"start": v(0.6, 2.48) * mm, "mid": v(0.6, 2.47) * mm, "end": v(0.6, 2.46) * mm});
            skLineSegment(sketch, "E552", {"start": v(0.92, 2.23) * mm, "end": v(0.96, 2.33) * mm});
            skArc(sketch, "E553", {"start": v(0.97, 2.36) * mm, "mid": v(0.99, 2.55) * mm, "end": v(0.97, 2.73) * mm});
            skLineSegment(sketch, "E554", {"start": v(0.9, 2.76) * mm, "end": v(0.97, 2.73) * mm});
            skLineSegment(sketch, "E555", {"start": v(0.92, 2.23) * mm, "end": v(1.03, 2.18) * mm});
            skCircle(sketch, "E556", {"center": v(0, 0) * mm, "radius": 1 * mm});
            skSolve(sketch);
        }
        {
            var Q0;
            {var subQ0=sQuery(id+"F0.wireOp",EDGE,"E2");Q0=makeQuery(id+"F0.imprint","IMPRINT",FACE,{"disambiguationData":[TD([[makeQuery(id+"F0.imprint","IMPRINT",EDGE,{"derivedFrom":subQ0}),1.0]])]});}
            extrude(context, id + "F1", {"entities" : qUnion([Q0]), "depth" : 25 * mm});
        }
        {
            var Q0;
            Q0=makeQuery(id+"F1.opExtrude","CAP_FACE",FACE,{"disambiguationData":[OSD([sQuery(id+"F0.wireOp",EDGE,"E0"),sQuery(id+"F0.wireOp",EDGE,"E1"),sQuery(id+"F0.wireOp",EDGE,"E2"),sQuery(id+"F0.wireOp",EDGE,"E3"),sQuery(id+"F0.wireOp",EDGE,"E4"),sQuery(id+"F0.wireOp",EDGE,"E5"),sQuery(id+"F0.wireOp",EDGE,"E6"),sQuery(id+"F0.wireOp",EDGE,"E7"),sQuery(id+"F0.wireOp",EDGE,"E8"),sQuery(id+"F0.wireOp",EDGE,"E9"),sQuery(id+"F0.wireOp",EDGE,"E10"),sQuery(id+"F0.wireOp",EDGE,"E11"),sQuery(id+"F0.wireOp",EDGE,"E12"),sQuery(id+"F0.wireOp",EDGE,"E13"),sQuery(id+"F0.wireOp",EDGE,"E14"),sQuery(id+"F0.wireOp",EDGE,"E15"),sQuery(id+"F0.wireOp",EDGE,"E16"),sQuery(id+"F0.wireOp",EDGE,"E17"),sQuery(id+"F0.wireOp",EDGE,"E18"),sQuery(id+"F0.wireOp",EDGE,"E19"),sQuery(id+"F0.wireOp",EDGE,"E20"),sQuery(id+"F0.wireOp",EDGE,"E21"),sQuery(id+"F0.wireOp",EDGE,"E22"),sQuery(id+"F0.wireOp",EDGE,"E23"),sQuery(id+"F0.wireOp",EDGE,"E24"),sQuery(id+"F0.wireOp",EDGE,"E25"),sQuery(id+"F0.wireOp",EDGE,"E26"),sQuery(id+"F0.wireOp",EDGE,"E27"),sQuery(id+"F0.wireOp",EDGE,"E28"),sQuery(id+"F0.wireOp",EDGE,"E29"),sQuery(id+"F0.wireOp",EDGE,"E30"),sQuery(id+"F0.wireOp",EDGE,"E31"),sQuery(id+"F0.wireOp",EDGE,"E32"),sQuery(id+"F0.wireOp",EDGE,"E33"),sQuery(id+"F0.wireOp",EDGE,"E34"),sQuery(id+"F0.wireOp",EDGE,"E35"),sQuery(id+"F0.wireOp",EDGE,"E36"),sQuery(id+"F0.wireOp",EDGE,"E37"),sQuery(id+"F0.wireOp",EDGE,"E38"),sQuery(id+"F0.wireOp",EDGE,"E39"),sQuery(id+"F0.wireOp",EDGE,"E40"),sQuery(id+"F0.wireOp",EDGE,"E41"),sQuery(id+"F0.wireOp",EDGE,"E42"),sQuery(id+"F0.wireOp",EDGE,"E43"),sQuery(id+"F0.wireOp",EDGE,"E44"),sQuery(id+"F0.wireOp",EDGE,"E45"),sQuery(id+"F0.wireOp",EDGE,"E46"),sQuery(id+"F0.wireOp",EDGE,"E47"),sQuery(id+"F0.wireOp",EDGE,"E48"),sQuery(id+"F0.wireOp",EDGE,"E49"),sQuery(id+"F0.wireOp",EDGE,"E50"),sQuery(id+"F0.wireOp",EDGE,"E51"),sQuery(id+"F0.wireOp",EDGE,"E52"),sQuery(id+"F0.wireOp",EDGE,"E53"),sQuery(id+"F0.wireOp",EDGE,"E54"),sQuery(id+"F0.wireOp",EDGE,"E55"),sQuery(id+"F0.wireOp",EDGE,"E56"),sQuery(id+"F0.wireOp",EDGE,"E57"),sQuery(id+"F0.wireOp",EDGE,"E58"),sQuery(id+"F0.wireOp",EDGE,"E59"),sQuery(id+"F0.wireOp",EDGE,"E60"),sQuery(id+"F0.wireOp",EDGE,"E61"),sQuery(id+"F0.wireOp",EDGE,"E62"),sQuery(id+"F0.wireOp",EDGE,"E63"),sQuery(id+"F0.wireOp",EDGE,"E64"),sQuery(id+"F0.wireOp",EDGE,"E65"),sQuery(id+"F0.wireOp",EDGE,"E66"),sQuery(id+"F0.wireOp",EDGE,"E67"),sQuery(id+"F0.wireOp",EDGE,"E68"),sQuery(id+"F0.wireOp",EDGE,"E69"),sQuery(id+"F0.wireOp",EDGE,"E70"),sQuery(id+"F0.wireOp",EDGE,"E71"),sQuery(id+"F0.wireOp",EDGE,"E72"),sQuery(id+"F0.wireOp",EDGE,"E73"),sQuery(id+"F0.wireOp",EDGE,"E74"),sQuery(id+"F0.wireOp",EDGE,"E75"),sQuery(id+"F0.wireOp",EDGE,"E76"),sQuery(id+"F0.wireOp",EDGE,"E77"),sQuery(id+"F0.wireOp",EDGE,"E78"),sQuery(id+"F0.wireOp",EDGE,"E79"),sQuery(id+"F0.wireOp",EDGE,"E80"),sQuery(id+"F0.wireOp",EDGE,"E81"),sQuery(id+"F0.wireOp",EDGE,"E82"),sQuery(id+"F0.wireOp",EDGE,"E83"),sQuery(id+"F0.wireOp",EDGE,"E84"),sQuery(id+"F0.wireOp",EDGE,"E85"),sQuery(id+"F0.wireOp",EDGE,"E86"),sQuery(id+"F0.wireOp",EDGE,"E87"),sQuery(id+"F0.wireOp",EDGE,"E88"),sQuery(id+"F0.wireOp",EDGE,"E89"),sQuery(id+"F0.wireOp",EDGE,"E90"),sQuery(id+"F0.wireOp",EDGE,"E91"),sQuery(id+"F0.wireOp",EDGE,"E92"),sQuery(id+"F0.wireOp",EDGE,"E93"),sQuery(id+"F0.wireOp",EDGE,"E94"),sQuery(id+"F0.wireOp",EDGE,"E95"),sQuery(id+"F0.wireOp",EDGE,"E96"),sQuery(id+"F0.wireOp",EDGE,"E97"),sQuery(id+"F0.wireOp",EDGE,"E98"),sQuery(id+"F0.wireOp",EDGE,"E99"),sQuery(id+"F0.wireOp",EDGE,"E100"),sQuery(id+"F0.wireOp",EDGE,"E101"),sQuery(id+"F0.wireOp",EDGE,"E102"),sQuery(id+"F0.wireOp",EDGE,"E103"),sQuery(id+"F0.wireOp",EDGE,"E104"),sQuery(id+"F0.wireOp",EDGE,"E105"),sQuery(id+"F0.wireOp",EDGE,"E106"),sQuery(id+"F0.wireOp",EDGE,"E107"),sQuery(id+"F0.wireOp",EDGE,"E108"),sQuery(id+"F0.wireOp",EDGE,"E109"),sQuery(id+"F0.wireOp",EDGE,"E110"),sQuery(id+"F0.wireOp",EDGE,"E111"),sQuery(id+"F0.wireOp",EDGE,"E112"),sQuery(id+"F0.wireOp",EDGE,"E113"),sQuery(id+"F0.wireOp",EDGE,"E114"),sQuery(id+"F0.wireOp",EDGE,"E115"),sQuery(id+"F0.wireOp",EDGE,"E116"),sQuery(id+"F0.wireOp",EDGE,"E117"),sQuery(id+"F0.wireOp",EDGE,"E118"),sQuery(id+"F0.wireOp",EDGE,"E119"),sQuery(id+"F0.wireOp",EDGE,"E120"),sQuery(id+"F0.wireOp",EDGE,"E121"),sQuery(id+"F0.wireOp",EDGE,"E122"),sQuery(id+"F0.wireOp",EDGE,"E123"),sQuery(id+"F0.wireOp",EDGE,"E124"),sQuery(id+"F0.wireOp",EDGE,"E125"),sQuery(id+"F0.wireOp",EDGE,"E126"),sQuery(id+"F0.wireOp",EDGE,"E127"),sQuery(id+"F0.wireOp",EDGE,"E128"),sQuery(id+"F0.wireOp",EDGE,"E129"),sQuery(id+"F0.wireOp",EDGE,"E130"),sQuery(id+"F0.wireOp",EDGE,"E131"),sQuery(id+"F0.wireOp",EDGE,"E132"),sQuery(id+"F0.wireOp",EDGE,"E133"),sQuery(id+"F0.wireOp",EDGE,"E134"),sQuery(id+"F0.wireOp",EDGE,"E135"),sQuery(id+"F0.wireOp",EDGE,"E136"),sQuery(id+"F0.wireOp",EDGE,"E137"),sQuery(id+"F0.wireOp",EDGE,"E138"),sQuery(id+"F0.wireOp",EDGE,"E139"),sQuery(id+"F0.wireOp",EDGE,"E140"),sQuery(id+"F0.wireOp",EDGE,"E141"),sQuery(id+"F0.wireOp",EDGE,"E142"),sQuery(id+"F0.wireOp",EDGE,"E143"),sQuery(id+"F0.wireOp",EDGE,"E144"),sQuery(id+"F0.wireOp",EDGE,"E145"),sQuery(id+"F0.wireOp",EDGE,"E146"),sQuery(id+"F0.wireOp",EDGE,"E147"),sQuery(id+"F0.wireOp",EDGE,"E148"),sQuery(id+"F0.wireOp",EDGE,"E149"),sQuery(id+"F0.wireOp",EDGE,"E150"),sQuery(id+"F0.wireOp",EDGE,"E151"),sQuery(id+"F0.wireOp",EDGE,"E152"),sQuery(id+"F0.wireOp",EDGE,"E153"),sQuery(id+"F0.wireOp",EDGE,"E154"),sQuery(id+"F0.wireOp",EDGE,"E155"),sQuery(id+"F0.wireOp",EDGE,"E156"),sQuery(id+"F0.wireOp",EDGE,"E157"),sQuery(id+"F0.wireOp",EDGE,"E158"),sQuery(id+"F0.wireOp",EDGE,"E159"),sQuery(id+"F0.wireOp",EDGE,"E160"),sQuery(id+"F0.wireOp",EDGE,"E161"),sQuery(id+"F0.wireOp",EDGE,"E162"),sQuery(id+"F0.wireOp",EDGE,"E163"),sQuery(id+"F0.wireOp",EDGE,"E164"),sQuery(id+"F0.wireOp",EDGE,"E165"),sQuery(id+"F0.wireOp",EDGE,"E166"),sQuery(id+"F0.wireOp",EDGE,"E167"),sQuery(id+"F0.wireOp",EDGE,"E168"),sQuery(id+"F0.wireOp",EDGE,"E169"),sQuery(id+"F0.wireOp",EDGE,"E170"),sQuery(id+"F0.wireOp",EDGE,"E171"),sQuery(id+"F0.wireOp",EDGE,"E172"),sQuery(id+"F0.wireOp",EDGE,"E173"),sQuery(id+"F0.wireOp",EDGE,"E174"),sQuery(id+"F0.wireOp",EDGE,"E175"),sQuery(id+"F0.wireOp",EDGE,"E176"),sQuery(id+"F0.wireOp",EDGE,"E177"),sQuery(id+"F0.wireOp",EDGE,"E178"),sQuery(id+"F0.wireOp",EDGE,"E179"),sQuery(id+"F0.wireOp",EDGE,"E180"),sQuery(id+"F0.wireOp",EDGE,"E181"),sQuery(id+"F0.wireOp",EDGE,"E182"),sQuery(id+"F0.wireOp",EDGE,"E183"),sQuery(id+"F0.wireOp",EDGE,"E184"),sQuery(id+"F0.wireOp",EDGE,"E185"),sQuery(id+"F0.wireOp",EDGE,"E186"),sQuery(id+"F0.wireOp",EDGE,"E187"),sQuery(id+"F0.wireOp",EDGE,"E188"),sQuery(id+"F0.wireOp",EDGE,"E189"),sQuery(id+"F0.wireOp",EDGE,"E190"),sQuery(id+"F0.wireOp",EDGE,"E191"),sQuery(id+"F0.wireOp",EDGE,"E192"),sQuery(id+"F0.wireOp",EDGE,"E193"),sQuery(id+"F0.wireOp",EDGE,"E194"),sQuery(id+"F0.wireOp",EDGE,"E195"),sQuery(id+"F0.wireOp",EDGE,"E196"),sQuery(id+"F0.wireOp",EDGE,"E197"),sQuery(id+"F0.wireOp",EDGE,"E198"),sQuery(id+"F0.wireOp",EDGE,"E199"),sQuery(id+"F0.wireOp",EDGE,"E200"),sQuery(id+"F0.wireOp",EDGE,"E201"),sQuery(id+"F0.wireOp",EDGE,"E202"),sQuery(id+"F0.wireOp",EDGE,"E203"),sQuery(id+"F0.wireOp",EDGE,"E204"),sQuery(id+"F0.wireOp",EDGE,"E205"),sQuery(id+"F0.wireOp",EDGE,"E206"),sQuery(id+"F0.wireOp",EDGE,"E207"),sQuery(id+"F0.wireOp",EDGE,"E208"),sQuery(id+"F0.wireOp",EDGE,"E209"),sQuery(id+"F0.wireOp",EDGE,"E210"),sQuery(id+"F0.wireOp",EDGE,"E211"),sQuery(id+"F0.wireOp",EDGE,"E212"),sQuery(id+"F0.wireOp",EDGE,"E213"),sQuery(id+"F0.wireOp",EDGE,"E214"),sQuery(id+"F0.wireOp",EDGE,"E215"),sQuery(id+"F0.wireOp",EDGE,"E216"),sQuery(id+"F0.wireOp",EDGE,"E217"),sQuery(id+"F0.wireOp",EDGE,"E218"),sQuery(id+"F0.wireOp",EDGE,"E219"),sQuery(id+"F0.wireOp",EDGE,"E220"),sQuery(id+"F0.wireOp",EDGE,"E221"),sQuery(id+"F0.wireOp",EDGE,"E222"),sQuery(id+"F0.wireOp",EDGE,"E223"),sQuery(id+"F0.wireOp",EDGE,"E224"),sQuery(id+"F0.wireOp",EDGE,"E225"),sQuery(id+"F0.wireOp",EDGE,"E226"),sQuery(id+"F0.wireOp",EDGE,"E227"),sQuery(id+"F0.wireOp",EDGE,"E228"),sQuery(id+"F0.wireOp",EDGE,"E229"),sQuery(id+"F0.wireOp",EDGE,"E230"),sQuery(id+"F0.wireOp",EDGE,"E231"),sQuery(id+"F0.wireOp",EDGE,"E232"),sQuery(id+"F0.wireOp",EDGE,"E233"),sQuery(id+"F0.wireOp",EDGE,"E234"),sQuery(id+"F0.wireOp",EDGE,"E235"),sQuery(id+"F0.wireOp",EDGE,"E236"),sQuery(id+"F0.wireOp",EDGE,"E237"),sQuery(id+"F0.wireOp",EDGE,"E238"),sQuery(id+"F0.wireOp",EDGE,"E239"),sQuery(id+"F0.wireOp",EDGE,"E240"),sQuery(id+"F0.wireOp",EDGE,"E241"),sQuery(id+"F0.wireOp",EDGE,"E242"),sQuery(id+"F0.wireOp",EDGE,"E243"),sQuery(id+"F0.wireOp",EDGE,"E244"),sQuery(id+"F0.wireOp",EDGE,"E245"),sQuery(id+"F0.wireOp",EDGE,"E246"),sQuery(id+"F0.wireOp",EDGE,"E247"),sQuery(id+"F0.wireOp",EDGE,"E248"),sQuery(id+"F0.wireOp",EDGE,"E249"),sQuery(id+"F0.wireOp",EDGE,"E250"),sQuery(id+"F0.wireOp",EDGE,"E251"),sQuery(id+"F0.wireOp",EDGE,"E252"),sQuery(id+"F0.wireOp",EDGE,"E253"),sQuery(id+"F0.wireOp",EDGE,"E254"),sQuery(id+"F0.wireOp",EDGE,"E255"),sQuery(id+"F0.wireOp",EDGE,"E256"),sQuery(id+"F0.wireOp",EDGE,"E257"),sQuery(id+"F0.wireOp",EDGE,"E258"),sQuery(id+"F0.wireOp",EDGE,"E259"),sQuery(id+"F0.wireOp",EDGE,"E260"),sQuery(id+"F0.wireOp",EDGE,"E261"),sQuery(id+"F0.wireOp",EDGE,"E262"),sQuery(id+"F0.wireOp",EDGE,"E263"),sQuery(id+"F0.wireOp",EDGE,"E264"),sQuery(id+"F0.wireOp",EDGE,"E265"),sQuery(id+"F0.wireOp",EDGE,"E266"),sQuery(id+"F0.wireOp",EDGE,"E267"),sQuery(id+"F0.wireOp",EDGE,"E268"),sQuery(id+"F0.wireOp",EDGE,"E269"),sQuery(id+"F0.wireOp",EDGE,"E270"),sQuery(id+"F0.wireOp",EDGE,"E271"),sQuery(id+"F0.wireOp",EDGE,"E272"),sQuery(id+"F0.wireOp",EDGE,"E273"),sQuery(id+"F0.wireOp",EDGE,"E274"),sQuery(id+"F0.wireOp",EDGE,"E275"),sQuery(id+"F0.wireOp",EDGE,"E276"),sQuery(id+"F0.wireOp",EDGE,"E277"),sQuery(id+"F0.wireOp",EDGE,"E278"),sQuery(id+"F0.wireOp",EDGE,"E279"),sQuery(id+"F0.wireOp",EDGE,"E280"),sQuery(id+"F0.wireOp",EDGE,"E281"),sQuery(id+"F0.wireOp",EDGE,"E282"),sQuery(id+"F0.wireOp",EDGE,"E283"),sQuery(id+"F0.wireOp",EDGE,"E284"),sQuery(id+"F0.wireOp",EDGE,"E285"),sQuery(id+"F0.wireOp",EDGE,"E286"),sQuery(id+"F0.wireOp",EDGE,"E287"),sQuery(id+"F0.wireOp",EDGE,"E288"),sQuery(id+"F0.wireOp",EDGE,"E289"),sQuery(id+"F0.wireOp",EDGE,"E290"),sQuery(id+"F0.wireOp",EDGE,"E291"),sQuery(id+"F0.wireOp",EDGE,"E292"),sQuery(id+"F0.wireOp",EDGE,"E293"),sQuery(id+"F0.wireOp",EDGE,"E294"),sQuery(id+"F0.wireOp",EDGE,"E295"),sQuery(id+"F0.wireOp",EDGE,"E296"),sQuery(id+"F0.wireOp",EDGE,"E297"),sQuery(id+"F0.wireOp",EDGE,"E298"),sQuery(id+"F0.wireOp",EDGE,"E299"),sQuery(id+"F0.wireOp",EDGE,"E300"),sQuery(id+"F0.wireOp",EDGE,"E301"),sQuery(id+"F0.wireOp",EDGE,"E302"),sQuery(id+"F0.wireOp",EDGE,"E303"),sQuery(id+"F0.wireOp",EDGE,"E304"),sQuery(id+"F0.wireOp",EDGE,"E305"),sQuery(id+"F0.wireOp",EDGE,"E306"),sQuery(id+"F0.wireOp",EDGE,"E307"),sQuery(id+"F0.wireOp",EDGE,"E308"),sQuery(id+"F0.wireOp",EDGE,"E309"),sQuery(id+"F0.wireOp",EDGE,"E310"),sQuery(id+"F0.wireOp",EDGE,"E311"),sQuery(id+"F0.wireOp",EDGE,"E312"),sQuery(id+"F0.wireOp",EDGE,"E313"),sQuery(id+"F0.wireOp",EDGE,"E314"),sQuery(id+"F0.wireOp",EDGE,"E315"),sQuery(id+"F0.wireOp",EDGE,"E316"),sQuery(id+"F0.wireOp",EDGE,"E317"),sQuery(id+"F0.wireOp",EDGE,"E318"),sQuery(id+"F0.wireOp",EDGE,"E319"),sQuery(id+"F0.wireOp",EDGE,"E320"),sQuery(id+"F0.wireOp",EDGE,"E321"),sQuery(id+"F0.wireOp",EDGE,"E322"),sQuery(id+"F0.wireOp",EDGE,"E323"),sQuery(id+"F0.wireOp",EDGE,"E324"),sQuery(id+"F0.wireOp",EDGE,"E325"),sQuery(id+"F0.wireOp",EDGE,"E326"),sQuery(id+"F0.wireOp",EDGE,"E327"),sQuery(id+"F0.wireOp",EDGE,"E328"),sQuery(id+"F0.wireOp",EDGE,"E329"),sQuery(id+"F0.wireOp",EDGE,"E330"),sQuery(id+"F0.wireOp",EDGE,"E331"),sQuery(id+"F0.wireOp",EDGE,"E332"),sQuery(id+"F0.wireOp",EDGE,"E333"),sQuery(id+"F0.wireOp",EDGE,"E334"),sQuery(id+"F0.wireOp",EDGE,"E335"),sQuery(id+"F0.wireOp",EDGE,"E336"),sQuery(id+"F0.wireOp",EDGE,"E337"),sQuery(id+"F0.wireOp",EDGE,"E338"),sQuery(id+"F0.wireOp",EDGE,"E339"),sQuery(id+"F0.wireOp",EDGE,"E340"),sQuery(id+"F0.wireOp",EDGE,"E341"),sQuery(id+"F0.wireOp",EDGE,"E342"),sQuery(id+"F0.wireOp",EDGE,"E343"),sQuery(id+"F0.wireOp",EDGE,"E344"),sQuery(id+"F0.wireOp",EDGE,"E345"),sQuery(id+"F0.wireOp",EDGE,"E346"),sQuery(id+"F0.wireOp",EDGE,"E347"),sQuery(id+"F0.wireOp",EDGE,"E348"),sQuery(id+"F0.wireOp",EDGE,"E349"),sQuery(id+"F0.wireOp",EDGE,"E350"),sQuery(id+"F0.wireOp",EDGE,"E351"),sQuery(id+"F0.wireOp",EDGE,"E352"),sQuery(id+"F0.wireOp",EDGE,"E353"),sQuery(id+"F0.wireOp",EDGE,"E354"),sQuery(id+"F0.wireOp",EDGE,"E355"),sQuery(id+"F0.wireOp",EDGE,"E356"),sQuery(id+"F0.wireOp",EDGE,"E357"),sQuery(id+"F0.wireOp",EDGE,"E358"),sQuery(id+"F0.wireOp",EDGE,"E359"),sQuery(id+"F0.wireOp",EDGE,"E360"),sQuery(id+"F0.wireOp",EDGE,"E361"),sQuery(id+"F0.wireOp",EDGE,"E362"),sQuery(id+"F0.wireOp",EDGE,"E363"),sQuery(id+"F0.wireOp",EDGE,"E364"),sQuery(id+"F0.wireOp",EDGE,"E365"),sQuery(id+"F0.wireOp",EDGE,"E366"),sQuery(id+"F0.wireOp",EDGE,"E367"),sQuery(id+"F0.wireOp",EDGE,"E368"),sQuery(id+"F0.wireOp",EDGE,"E369"),sQuery(id+"F0.wireOp",EDGE,"E370"),sQuery(id+"F0.wireOp",EDGE,"E371"),sQuery(id+"F0.wireOp",EDGE,"E372"),sQuery(id+"F0.wireOp",EDGE,"E373"),sQuery(id+"F0.wireOp",EDGE,"E374"),sQuery(id+"F0.wireOp",EDGE,"E375"),sQuery(id+"F0.wireOp",EDGE,"E376"),sQuery(id+"F0.wireOp",EDGE,"E377"),sQuery(id+"F0.wireOp",EDGE,"E378"),sQuery(id+"F0.wireOp",EDGE,"E379"),sQuery(id+"F0.wireOp",EDGE,"E380"),sQuery(id+"F0.wireOp",EDGE,"E381"),sQuery(id+"F0.wireOp",EDGE,"E382"),sQuery(id+"F0.wireOp",EDGE,"E383"),sQuery(id+"F0.wireOp",EDGE,"E384"),sQuery(id+"F0.wireOp",EDGE,"E385"),sQuery(id+"F0.wireOp",EDGE,"E386"),sQuery(id+"F0.wireOp",EDGE,"E387"),sQuery(id+"F0.wireOp",EDGE,"E388"),sQuery(id+"F0.wireOp",EDGE,"E389"),sQuery(id+"F0.wireOp",EDGE,"E390"),sQuery(id+"F0.wireOp",EDGE,"E391"),sQuery(id+"F0.wireOp",EDGE,"E392"),sQuery(id+"F0.wireOp",EDGE,"E393"),sQuery(id+"F0.wireOp",EDGE,"E394"),sQuery(id+"F0.wireOp",EDGE,"E395"),sQuery(id+"F0.wireOp",EDGE,"E396"),sQuery(id+"F0.wireOp",EDGE,"E397"),sQuery(id+"F0.wireOp",EDGE,"E398"),sQuery(id+"F0.wireOp",EDGE,"E399"),sQuery(id+"F0.wireOp",EDGE,"E400"),sQuery(id+"F0.wireOp",EDGE,"E401"),sQuery(id+"F0.wireOp",EDGE,"E402"),sQuery(id+"F0.wireOp",EDGE,"E403"),sQuery(id+"F0.wireOp",EDGE,"E404"),sQuery(id+"F0.wireOp",EDGE,"E405"),sQuery(id+"F0.wireOp",EDGE,"E406"),sQuery(id+"F0.wireOp",EDGE,"E407"),sQuery(id+"F0.wireOp",EDGE,"E408"),sQuery(id+"F0.wireOp",EDGE,"E409"),sQuery(id+"F0.wireOp",EDGE,"E410"),sQuery(id+"F0.wireOp",EDGE,"E411"),sQuery(id+"F0.wireOp",EDGE,"E412"),sQuery(id+"F0.wireOp",EDGE,"E413"),sQuery(id+"F0.wireOp",EDGE,"E414"),sQuery(id+"F0.wireOp",EDGE,"E415"),sQuery(id+"F0.wireOp",EDGE,"E416"),sQuery(id+"F0.wireOp",EDGE,"E417"),sQuery(id+"F0.wireOp",EDGE,"E418"),sQuery(id+"F0.wireOp",EDGE,"E419"),sQuery(id+"F0.wireOp",EDGE,"E420"),sQuery(id+"F0.wireOp",EDGE,"E421"),sQuery(id+"F0.wireOp",EDGE,"E422"),sQuery(id+"F0.wireOp",EDGE,"E423"),sQuery(id+"F0.wireOp",EDGE,"E424"),sQuery(id+"F0.wireOp",EDGE,"E425"),sQuery(id+"F0.wireOp",EDGE,"E426"),sQuery(id+"F0.wireOp",EDGE,"E427"),sQuery(id+"F0.wireOp",EDGE,"E428"),sQuery(id+"F0.wireOp",EDGE,"E429"),sQuery(id+"F0.wireOp",EDGE,"E430"),sQuery(id+"F0.wireOp",EDGE,"E431"),sQuery(id+"F0.wireOp",EDGE,"E432"),sQuery(id+"F0.wireOp",EDGE,"E433"),sQuery(id+"F0.wireOp",EDGE,"E434"),sQuery(id+"F0.wireOp",EDGE,"E435"),sQuery(id+"F0.wireOp",EDGE,"E436"),sQuery(id+"F0.wireOp",EDGE,"E437"),sQuery(id+"F0.wireOp",EDGE,"E438"),sQuery(id+"F0.wireOp",EDGE,"E439"),sQuery(id+"F0.wireOp",EDGE,"E440"),sQuery(id+"F0.wireOp",EDGE,"E441"),sQuery(id+"F0.wireOp",EDGE,"E442"),sQuery(id+"F0.wireOp",EDGE,"E443"),sQuery(id+"F0.wireOp",EDGE,"E444"),sQuery(id+"F0.wireOp",EDGE,"E445"),sQuery(id+"F0.wireOp",EDGE,"E446"),sQuery(id+"F0.wireOp",EDGE,"E447"),sQuery(id+"F0.wireOp",EDGE,"E448"),sQuery(id+"F0.wireOp",EDGE,"E449"),sQuery(id+"F0.wireOp",EDGE,"E450"),sQuery(id+"F0.wireOp",EDGE,"E451"),sQuery(id+"F0.wireOp",EDGE,"E452"),sQuery(id+"F0.wireOp",EDGE,"E453"),sQuery(id+"F0.wireOp",EDGE,"E454"),sQuery(id+"F0.wireOp",EDGE,"E455"),sQuery(id+"F0.wireOp",EDGE,"E456"),sQuery(id+"F0.wireOp",EDGE,"E457"),sQuery(id+"F0.wireOp",EDGE,"E458"),sQuery(id+"F0.wireOp",EDGE,"E459"),sQuery(id+"F0.wireOp",EDGE,"E460"),sQuery(id+"F0.wireOp",EDGE,"E461"),sQuery(id+"F0.wireOp",EDGE,"E462"),sQuery(id+"F0.wireOp",EDGE,"E463"),sQuery(id+"F0.wireOp",EDGE,"E464"),sQuery(id+"F0.wireOp",EDGE,"E465"),sQuery(id+"F0.wireOp",EDGE,"E466"),sQuery(id+"F0.wireOp",EDGE,"E467"),sQuery(id+"F0.wireOp",EDGE,"E468"),sQuery(id+"F0.wireOp",EDGE,"E469"),sQuery(id+"F0.wireOp",EDGE,"E470"),sQuery(id+"F0.wireOp",EDGE,"E471"),sQuery(id+"F0.wireOp",EDGE,"E472"),sQuery(id+"F0.wireOp",EDGE,"E473"),sQuery(id+"F0.wireOp",EDGE,"E474"),sQuery(id+"F0.wireOp",EDGE,"E475"),sQuery(id+"F0.wireOp",EDGE,"E476"),sQuery(id+"F0.wireOp",EDGE,"E477"),sQuery(id+"F0.wireOp",EDGE,"E478"),sQuery(id+"F0.wireOp",EDGE,"E479"),sQuery(id+"F0.wireOp",EDGE,"E480"),sQuery(id+"F0.wireOp",EDGE,"E481"),sQuery(id+"F0.wireOp",EDGE,"E482"),sQuery(id+"F0.wireOp",EDGE,"E483"),sQuery(id+"F0.wireOp",EDGE,"E484"),sQuery(id+"F0.wireOp",EDGE,"E485"),sQuery(id+"F0.wireOp",EDGE,"E486"),sQuery(id+"F0.wireOp",EDGE,"E487"),sQuery(id+"F0.wireOp",EDGE,"E488"),sQuery(id+"F0.wireOp",EDGE,"E489"),sQuery(id+"F0.wireOp",EDGE,"E490"),sQuery(id+"F0.wireOp",EDGE,"E491"),sQuery(id+"F0.wireOp",EDGE,"E492"),sQuery(id+"F0.wireOp",EDGE,"E493"),sQuery(id+"F0.wireOp",EDGE,"E494"),sQuery(id+"F0.wireOp",EDGE,"E495"),sQuery(id+"F0.wireOp",EDGE,"E496"),sQuery(id+"F0.wireOp",EDGE,"E497"),sQuery(id+"F0.wireOp",EDGE,"E498"),sQuery(id+"F0.wireOp",EDGE,"E499"),sQuery(id+"F0.wireOp",EDGE,"E500"),sQuery(id+"F0.wireOp",EDGE,"E501"),sQuery(id+"F0.wireOp",EDGE,"E502"),sQuery(id+"F0.wireOp",EDGE,"E503"),sQuery(id+"F0.wireOp",EDGE,"E504"),sQuery(id+"F0.wireOp",EDGE,"E505"),sQuery(id+"F0.wireOp",EDGE,"E506"),sQuery(id+"F0.wireOp",EDGE,"E507"),sQuery(id+"F0.wireOp",EDGE,"E508"),sQuery(id+"F0.wireOp",EDGE,"E509"),sQuery(id+"F0.wireOp",EDGE,"E510"),sQuery(id+"F0.wireOp",EDGE,"E511"),sQuery(id+"F0.wireOp",EDGE,"E512"),sQuery(id+"F0.wireOp",EDGE,"E513"),sQuery(id+"F0.wireOp",EDGE,"E514"),sQuery(id+"F0.wireOp",EDGE,"E515"),sQuery(id+"F0.wireOp",EDGE,"E516"),sQuery(id+"F0.wireOp",EDGE,"E517"),sQuery(id+"F0.wireOp",EDGE,"E518"),sQuery(id+"F0.wireOp",EDGE,"E519"),sQuery(id+"F0.wireOp",EDGE,"E520"),sQuery(id+"F0.wireOp",EDGE,"E521"),sQuery(id+"F0.wireOp",EDGE,"E522"),sQuery(id+"F0.wireOp",EDGE,"E523"),sQuery(id+"F0.wireOp",EDGE,"E524"),sQuery(id+"F0.wireOp",EDGE,"E525"),sQuery(id+"F0.wireOp",EDGE,"E526"),sQuery(id+"F0.wireOp",EDGE,"E527"),sQuery(id+"F0.wireOp",EDGE,"E528"),sQuery(id+"F0.wireOp",EDGE,"E529"),sQuery(id+"F0.wireOp",EDGE,"E530"),sQuery(id+"F0.wireOp",EDGE,"E531"),sQuery(id+"F0.wireOp",EDGE,"E532"),sQuery(id+"F0.wireOp",EDGE,"E533"),sQuery(id+"F0.wireOp",EDGE,"E534"),sQuery(id+"F0.wireOp",EDGE,"E535"),sQuery(id+"F0.wireOp",EDGE,"E536"),sQuery(id+"F0.wireOp",EDGE,"E537"),sQuery(id+"F0.wireOp",EDGE,"E538"),sQuery(id+"F0.wireOp",EDGE,"E539"),sQuery(id+"F0.wireOp",EDGE,"E540"),sQuery(id+"F0.wireOp",EDGE,"E541"),sQuery(id+"F0.wireOp",EDGE,"E542"),sQuery(id+"F0.wireOp",EDGE,"E543"),sQuery(id+"F0.wireOp",EDGE,"E544"),sQuery(id+"F0.wireOp",EDGE,"E545"),sQuery(id+"F0.wireOp",EDGE,"E546"),sQuery(id+"F0.wireOp",EDGE,"E547"),sQuery(id+"F0.wireOp",EDGE,"E548"),sQuery(id+"F0.wireOp",EDGE,"E549"),sQuery(id+"F0.wireOp",EDGE,"E550"),sQuery(id+"F0.wireOp",EDGE,"E551"),sQuery(id+"F0.wireOp",EDGE,"E552"),sQuery(id+"F0.wireOp",EDGE,"E553"),sQuery(id+"F0.wireOp",EDGE,"E554"),sQuery(id+"F0.wireOp",EDGE,"E555")])],"isStart":true});
            var sketch = newSketch(context, id + "F2", { "sketchPlane" : qUnion([Q0])});
            skLineSegment(sketch, "E557", {"start": v(-6.71, 17.47) * mm, "end": v(-6.37, 16.97) * mm});
            skLineSegment(sketch, "E558", {"start": v(-6.37, 16.97) * mm, "end": v(-6.2, 16.63) * mm});
            skArc(sketch, "E559", {"start": v(-6.71, 17.47) * mm, "mid": v(-7.17, 18) * mm, "end": v(-7.69, 18.46) * mm});
            skLineSegment(sketch, "E560", {"start": v(-8.38, 18.16) * mm, "end": v(-7.69, 18.46) * mm});
            skArc(sketch, "E561", {"start": v(-6.2, 16.63) * mm, "mid": v(-6.27, 16.78) * mm, "end": v(-6.35, 16.93) * mm});
            skArc(sketch, "E562", {"start": v(-6.2, 16.63) * mm, "mid": v(-5.68, 16.55) * mm, "end": v(-5.32, 16.93) * mm});
            skArc(sketch, "E563", {"start": v(-6.35, 16.93) * mm, "mid": v(-6.52, 17.2) * mm, "end": v(-6.71, 17.47) * mm});
            skArc(sketch, "E564", {"start": v(-5.28, 19.3) * mm, "mid": v(-5.4, 18.6) * mm, "end": v(-5.43, 17.9) * mm});
            skArc(sketch, "E565", {"start": v(-5.43, 17.9) * mm, "mid": v(-5.42, 17.59) * mm, "end": v(-5.39, 17.26) * mm});
            skArc(sketch, "E566", {"start": v(-5.39, 17.26) * mm, "mid": v(-5.36, 17.1) * mm, "end": v(-5.32, 16.93) * mm});
            skLineSegment(sketch, "E567", {"start": v(-11.25, 16.53) * mm, "end": v(-10.62, 16.95) * mm});
            skArc(sketch, "E568", {"start": v(-9.5, 16.13) * mm, "mid": v(-10.04, 16.57) * mm, "end": v(-10.62, 16.95) * mm});
            skArc(sketch, "E569", {"start": v(-8.86, 15.38) * mm, "mid": v(-8.33, 15.4) * mm, "end": v(-8.03, 15.83) * mm});
            skArc(sketch, "E570", {"start": v(-9.05, 15.66) * mm, "mid": v(-9.26, 15.9) * mm, "end": v(-9.5, 16.13) * mm});
            skArc(sketch, "E571", {"start": v(-8.86, 15.38) * mm, "mid": v(-8.95, 15.52) * mm, "end": v(-9.05, 15.66) * mm});
            skArc(sketch, "E572", {"start": v(-8.16, 16.14) * mm, "mid": v(-8.1, 15.98) * mm, "end": v(-8.03, 15.83) * mm});
            skArc(sketch, "E573", {"start": v(-8.3, 16.77) * mm, "mid": v(-8.24, 16.45) * mm, "end": v(-8.16, 16.14) * mm});
            skArc(sketch, "E574", {"start": v(-8.38, 18.16) * mm, "mid": v(-8.38, 17.46) * mm, "end": v(-8.3, 16.77) * mm});
            skLineSegment(sketch, "E575", {"start": v(-13.82, 14.46) * mm, "end": v(-13.26, 14.97) * mm});
            skArc(sketch, "E576", {"start": v(-12.02, 14.34) * mm, "mid": v(-12.63, 14.69) * mm, "end": v(-13.26, 14.97) * mm});
            skArc(sketch, "E577", {"start": v(-11.27, 13.71) * mm, "mid": v(-10.75, 13.81) * mm, "end": v(-10.53, 14.3) * mm});
            skArc(sketch, "E578", {"start": v(-11.5, 13.95) * mm, "mid": v(-11.76, 14.16) * mm, "end": v(-12.02, 14.34) * mm});
            skArc(sketch, "E579", {"start": v(-11.27, 13.71) * mm, "mid": v(-11.38, 13.84) * mm, "end": v(-11.5, 13.95) * mm});
            skArc(sketch, "E580", {"start": v(-10.7, 14.58) * mm, "mid": v(-10.62, 14.43) * mm, "end": v(-10.53, 14.3) * mm});
            skArc(sketch, "E581", {"start": v(-10.95, 15.18) * mm, "mid": v(-10.84, 14.87) * mm, "end": v(-10.7, 14.58) * mm});
            skArc(sketch, "E582", {"start": v(-11.25, 16.53) * mm, "mid": v(-11.14, 15.85) * mm, "end": v(-10.95, 15.18) * mm});
            skLineSegment(sketch, "E583", {"start": v(-16.01, 11.98) * mm, "end": v(-15.55, 12.58) * mm});
            skArc(sketch, "E584", {"start": v(-14.22, 12.17) * mm, "mid": v(-14.87, 12.4) * mm, "end": v(-15.55, 12.58) * mm});
            skArc(sketch, "E585", {"start": v(-13.37, 11.67) * mm, "mid": v(-12.88, 11.85) * mm, "end": v(-12.74, 12.36) * mm});
            skArc(sketch, "E586", {"start": v(-13.65, 11.87) * mm, "mid": v(-13.93, 12.03) * mm, "end": v(-14.22, 12.17) * mm});
            skArc(sketch, "E587", {"start": v(-13.37, 11.67) * mm, "mid": v(-13.5, 11.78) * mm, "end": v(-13.65, 11.87) * mm});
            skArc(sketch, "E588", {"start": v(-12.96, 12.62) * mm, "mid": v(-12.85, 12.49) * mm, "end": v(-12.74, 12.36) * mm});
            skArc(sketch, "E589", {"start": v(-13.3, 13.17) * mm, "mid": v(-13.14, 12.88) * mm, "end": v(-12.96, 12.62) * mm});
            skArc(sketch, "E590", {"start": v(-13.82, 14.46) * mm, "mid": v(-13.6, 13.8) * mm, "end": v(-13.3, 13.17) * mm});
            skLineSegment(sketch, "E591", {"start": v(-17.77, 9.18) * mm, "end": v(-17.4, 9.85) * mm});
            skArc(sketch, "E592", {"start": v(-16.03, 9.66) * mm, "mid": v(-16.71, 9.8) * mm, "end": v(-17.4, 9.85) * mm});
            skArc(sketch, "E593", {"start": v(-15.11, 9.31) * mm, "mid": v(-14.65, 9.57) * mm, "end": v(-14.6, 10.1) * mm});
            skArc(sketch, "E594", {"start": v(-15.41, 9.46) * mm, "mid": v(-15.72, 9.58) * mm, "end": v(-16.03, 9.66) * mm});
            skArc(sketch, "E595", {"start": v(-15.11, 9.31) * mm, "mid": v(-15.26, 9.4) * mm, "end": v(-15.41, 9.46) * mm});
            skArc(sketch, "E596", {"start": v(-14.86, 10.31) * mm, "mid": v(-14.73, 10.2) * mm, "end": v(-14.6, 10.1) * mm});
            skArc(sketch, "E597", {"start": v(-15.29, 10.8) * mm, "mid": v(-15.08, 10.55) * mm, "end": v(-14.86, 10.31) * mm});
            skArc(sketch, "E598", {"start": v(-16.01, 11.98) * mm, "mid": v(-15.68, 11.37) * mm, "end": v(-15.29, 10.8) * mm});
            skLineSegment(sketch, "E599", {"start": v(-19.04, 6.13) * mm, "end": v(-18.8, 6.85) * mm});
            skArc(sketch, "E600", {"start": v(-17.4, 6.9) * mm, "mid": v(-18.1, 6.9) * mm, "end": v(-18.8, 6.85) * mm});
            skArc(sketch, "E601", {"start": v(-16.44, 6.7) * mm, "mid": v(-16.03, 7.03) * mm, "end": v(-16.06, 7.56) * mm});
            skArc(sketch, "E602", {"start": v(-16.76, 6.8) * mm, "mid": v(-17.08, 6.86) * mm, "end": v(-17.4, 6.9) * mm});
            skArc(sketch, "E603", {"start": v(-16.44, 6.7) * mm, "mid": v(-16.6, 6.75) * mm, "end": v(-16.76, 6.8) * mm});
            skArc(sketch, "E604", {"start": v(-16.35, 7.73) * mm, "mid": v(-16.2, 7.64) * mm, "end": v(-16.06, 7.56) * mm});
            skArc(sketch, "E605", {"start": v(-16.86, 8.13) * mm, "mid": v(-16.61, 7.92) * mm, "end": v(-16.35, 7.73) * mm});
            skArc(sketch, "E606", {"start": v(-17.77, 9.18) * mm, "mid": v(-17.34, 8.63) * mm, "end": v(-16.86, 8.13) * mm});
            skLineSegment(sketch, "E607", {"start": v(-19.79, 2.92) * mm, "end": v(-19.66, 3.66) * mm});
            skArc(sketch, "E608", {"start": v(-18.3, 3.93) * mm, "mid": v(-18.99, 3.84) * mm, "end": v(-19.66, 3.66) * mm});
            skArc(sketch, "E609", {"start": v(-17.32, 3.9) * mm, "mid": v(-16.97, 4.3) * mm, "end": v(-17.09, 4.81) * mm});
            skArc(sketch, "E610", {"start": v(-17.65, 3.95) * mm, "mid": v(-17.97, 3.95) * mm, "end": v(-18.3, 3.93) * mm});
            skArc(sketch, "E611", {"start": v(-17.32, 3.9) * mm, "mid": v(-17.48, 3.93) * mm, "end": v(-17.65, 3.95) * mm});
            skArc(sketch, "E612", {"start": v(-17.4, 4.93) * mm, "mid": v(-17.24, 4.87) * mm, "end": v(-17.09, 4.81) * mm});
            skArc(sketch, "E613", {"start": v(-17.96, 5.25) * mm, "mid": v(-17.69, 5.08) * mm, "end": v(-17.4, 4.93) * mm});
            skArc(sketch, "E614", {"start": v(-19.04, 6.13) * mm, "mid": v(-18.52, 5.66) * mm, "end": v(-17.96, 5.25) * mm});
            skLineSegment(sketch, "E615", {"start": v(-20, -0.38) * mm, "end": v(-20, 0.38) * mm});
            skArc(sketch, "E616", {"start": v(-18.7, 0.87) * mm, "mid": v(-19.36, 0.66) * mm, "end": v(-20, 0.38) * mm});
            skArc(sketch, "E617", {"start": v(-17.72, 1) * mm, "mid": v(-17.44, 1.45) * mm, "end": v(-17.64, 1.93) * mm});
            skArc(sketch, "E618", {"start": v(-18.06, 0.99) * mm, "mid": v(-18.38, 0.94) * mm, "end": v(-18.7, 0.87) * mm});
            skArc(sketch, "E619", {"start": v(-17.72, 1) * mm, "mid": v(-17.9, 1) * mm, "end": v(-18.06, 0.99) * mm});
            skArc(sketch, "E620", {"start": v(-17.98, 2) * mm, "mid": v(-17.81, 1.96) * mm, "end": v(-17.64, 1.93) * mm});
            skArc(sketch, "E621", {"start": v(-18.58, 2.22) * mm, "mid": v(-18.28, 2.1) * mm, "end": v(-17.98, 2) * mm});
            skArc(sketch, "E622", {"start": v(-19.79, 2.92) * mm, "mid": v(-19.2, 2.54) * mm, "end": v(-18.58, 2.22) * mm});
            skLineSegment(sketch, "E623", {"start": v(-19.66, -3.66) * mm, "end": v(-19.79, -2.92) * mm});
            skArc(sketch, "E624", {"start": v(-18.58, -2.22) * mm, "mid": v(-19.2, -2.54) * mm, "end": v(-19.79, -2.92) * mm});
            skArc(sketch, "E625", {"start": v(-17.64, -1.93) * mm, "mid": v(-17.44, -1.45) * mm, "end": v(-17.72, -1) * mm});
            skArc(sketch, "E626", {"start": v(-17.98, -2) * mm, "mid": v(-18.28, -2.1) * mm, "end": v(-18.58, -2.22) * mm});
            skArc(sketch, "E627", {"start": v(-17.64, -1.93) * mm, "mid": v(-17.81, -1.96) * mm, "end": v(-17.98, -2) * mm});
            skArc(sketch, "E628", {"start": v(-18.06, -0.99) * mm, "mid": v(-17.9, -1) * mm, "end": v(-17.72, -1) * mm});
            skArc(sketch, "E629", {"start": v(-18.7, -0.87) * mm, "mid": v(-18.38, -0.94) * mm, "end": v(-18.06, -0.99) * mm});
            skArc(sketch, "E630", {"start": v(-20, -0.38) * mm, "mid": v(-19.36, -0.66) * mm, "end": v(-18.7, -0.87) * mm});
            skLineSegment(sketch, "E631", {"start": v(-18.8, -6.85) * mm, "end": v(-19.04, -6.13) * mm});
            skArc(sketch, "E632", {"start": v(-17.96, -5.25) * mm, "mid": v(-18.52, -5.66) * mm, "end": v(-19.04, -6.13) * mm});
            skArc(sketch, "E633", {"start": v(-17.09, -4.81) * mm, "mid": v(-16.97, -4.3) * mm, "end": v(-17.32, -3.9) * mm});
            skArc(sketch, "E634", {"start": v(-17.4, -4.93) * mm, "mid": v(-17.69, -5.08) * mm, "end": v(-17.96, -5.25) * mm});
            skArc(sketch, "E635", {"start": v(-17.09, -4.81) * mm, "mid": v(-17.24, -4.87) * mm, "end": v(-17.4, -4.93) * mm});
            skArc(sketch, "E636", {"start": v(-17.65, -3.95) * mm, "mid": v(-17.48, -3.93) * mm, "end": v(-17.32, -3.9) * mm});
            skArc(sketch, "E637", {"start": v(-18.3, -3.93) * mm, "mid": v(-17.97, -3.95) * mm, "end": v(-17.65, -3.95) * mm});
            skArc(sketch, "E638", {"start": v(-19.66, -3.66) * mm, "mid": v(-18.99, -3.84) * mm, "end": v(-18.3, -3.93) * mm});
            skLineSegment(sketch, "E639", {"start": v(-17.4, -9.85) * mm, "end": v(-17.77, -9.18) * mm});
            skArc(sketch, "E640", {"start": v(-16.86, -8.13) * mm, "mid": v(-17.34, -8.63) * mm, "end": v(-17.77, -9.18) * mm});
            skArc(sketch, "E641", {"start": v(-16.06, -7.56) * mm, "mid": v(-16.03, -7.03) * mm, "end": v(-16.44, -6.7) * mm});
            skArc(sketch, "E642", {"start": v(-16.35, -7.73) * mm, "mid": v(-16.61, -7.92) * mm, "end": v(-16.86, -8.13) * mm});
            skArc(sketch, "E643", {"start": v(-16.06, -7.56) * mm, "mid": v(-16.2, -7.64) * mm, "end": v(-16.35, -7.73) * mm});
            skArc(sketch, "E644", {"start": v(-16.76, -6.8) * mm, "mid": v(-16.6, -6.75) * mm, "end": v(-16.44, -6.7) * mm});
            skArc(sketch, "E645", {"start": v(-17.4, -6.9) * mm, "mid": v(-17.08, -6.86) * mm, "end": v(-16.76, -6.8) * mm});
            skArc(sketch, "E646", {"start": v(-18.8, -6.85) * mm, "mid": v(-18.1, -6.9) * mm, "end": v(-17.4, -6.9) * mm});
            skLineSegment(sketch, "E647", {"start": v(-15.55, -12.58) * mm, "end": v(-16.01, -11.98) * mm});
            skArc(sketch, "E648", {"start": v(-15.29, -10.8) * mm, "mid": v(-15.68, -11.37) * mm, "end": v(-16.01, -11.98) * mm});
            skArc(sketch, "E649", {"start": v(-14.6, -10.1) * mm, "mid": v(-14.65, -9.57) * mm, "end": v(-15.11, -9.31) * mm});
            skArc(sketch, "E650", {"start": v(-14.86, -10.31) * mm, "mid": v(-15.08, -10.55) * mm, "end": v(-15.29, -10.8) * mm});
            skArc(sketch, "E651", {"start": v(-14.6, -10.1) * mm, "mid": v(-14.73, -10.2) * mm, "end": v(-14.86, -10.31) * mm});
            skArc(sketch, "E652", {"start": v(-15.41, -9.46) * mm, "mid": v(-15.26, -9.4) * mm, "end": v(-15.11, -9.31) * mm});
            skArc(sketch, "E653", {"start": v(-16.03, -9.66) * mm, "mid": v(-15.72, -9.58) * mm, "end": v(-15.41, -9.46) * mm});
            skArc(sketch, "E654", {"start": v(-17.4, -9.85) * mm, "mid": v(-16.71, -9.8) * mm, "end": v(-16.03, -9.66) * mm});
            skLineSegment(sketch, "E655", {"start": v(-13.26, -14.97) * mm, "end": v(-13.82, -14.46) * mm});
            skArc(sketch, "E656", {"start": v(-13.3, -13.17) * mm, "mid": v(-13.6, -13.8) * mm, "end": v(-13.82, -14.46) * mm});
            skArc(sketch, "E657", {"start": v(-12.74, -12.36) * mm, "mid": v(-12.88, -11.85) * mm, "end": v(-13.37, -11.67) * mm});
            skArc(sketch, "E658", {"start": v(-12.96, -12.62) * mm, "mid": v(-13.14, -12.88) * mm, "end": v(-13.3, -13.17) * mm});
            skArc(sketch, "E659", {"start": v(-12.74, -12.36) * mm, "mid": v(-12.85, -12.49) * mm, "end": v(-12.96, -12.62) * mm});
            skArc(sketch, "E660", {"start": v(-13.64, -11.87) * mm, "mid": v(-13.5, -11.78) * mm, "end": v(-13.37, -11.67) * mm});
            skArc(sketch, "E661", {"start": v(-14.22, -12.17) * mm, "mid": v(-13.93, -12.03) * mm, "end": v(-13.64, -11.87) * mm});
            skArc(sketch, "E662", {"start": v(-15.55, -12.58) * mm, "mid": v(-14.87, -12.4) * mm, "end": v(-14.22, -12.17) * mm});
            skLineSegment(sketch, "E663", {"start": v(-10.62, -16.95) * mm, "end": v(-11.25, -16.53) * mm});
            skArc(sketch, "E664", {"start": v(-10.95, -15.18) * mm, "mid": v(-11.14, -15.85) * mm, "end": v(-11.25, -16.53) * mm});
            skArc(sketch, "E665", {"start": v(-10.53, -14.3) * mm, "mid": v(-10.75, -13.81) * mm, "end": v(-11.27, -13.71) * mm});
            skArc(sketch, "E666", {"start": v(-10.7, -14.58) * mm, "mid": v(-10.84, -14.87) * mm, "end": v(-10.95, -15.18) * mm});
            skArc(sketch, "E667", {"start": v(-10.53, -14.3) * mm, "mid": v(-10.62, -14.43) * mm, "end": v(-10.7, -14.58) * mm});
            skArc(sketch, "E668", {"start": v(-11.5, -13.95) * mm, "mid": v(-11.38, -13.84) * mm, "end": v(-11.27, -13.71) * mm});
            skArc(sketch, "E669", {"start": v(-12.02, -14.34) * mm, "mid": v(-11.76, -14.16) * mm, "end": v(-11.5, -13.95) * mm});
            skArc(sketch, "E670", {"start": v(-13.26, -14.97) * mm, "mid": v(-12.63, -14.69) * mm, "end": v(-12.02, -14.34) * mm});
            skLineSegment(sketch, "E671", {"start": v(-7.69, -18.46) * mm, "end": v(-8.38, -18.16) * mm});
            skArc(sketch, "E672", {"start": v(-8.3, -16.77) * mm, "mid": v(-8.38, -17.46) * mm, "end": v(-8.38, -18.16) * mm});
            skArc(sketch, "E673", {"start": v(-8.03, -15.83) * mm, "mid": v(-8.33, -15.4) * mm, "end": v(-8.86, -15.38) * mm});
            skArc(sketch, "E674", {"start": v(-8.16, -16.14) * mm, "mid": v(-8.24, -16.45) * mm, "end": v(-8.3, -16.77) * mm});
            skArc(sketch, "E675", {"start": v(-8.03, -15.83) * mm, "mid": v(-8.1, -15.98) * mm, "end": v(-8.16, -16.14) * mm});
            skArc(sketch, "E676", {"start": v(-9.05, -15.66) * mm, "mid": v(-8.95, -15.52) * mm, "end": v(-8.86, -15.38) * mm});
            skArc(sketch, "E677", {"start": v(-9.5, -16.13) * mm, "mid": v(-9.26, -15.9) * mm, "end": v(-9.05, -15.66) * mm});
            skArc(sketch, "E678", {"start": v(-10.62, -16.95) * mm, "mid": v(-10.04, -16.57) * mm, "end": v(-9.5, -16.13) * mm});
            skLineSegment(sketch, "E679", {"start": v(-4.54, -19.48) * mm, "end": v(-5.28, -19.3) * mm});
            skArc(sketch, "E680", {"start": v(-5.43, -17.9) * mm, "mid": v(-5.4, -18.6) * mm, "end": v(-5.28, -19.3) * mm});
            skArc(sketch, "E681", {"start": v(-5.32, -16.93) * mm, "mid": v(-5.68, -16.55) * mm, "end": v(-6.2, -16.63) * mm});
            skArc(sketch, "E682", {"start": v(-5.39, -17.26) * mm, "mid": v(-5.42, -17.59) * mm, "end": v(-5.43, -17.9) * mm});
            skArc(sketch, "E683", {"start": v(-5.32, -16.93) * mm, "mid": v(-5.36, -17.1) * mm, "end": v(-5.39, -17.26) * mm});
            skArc(sketch, "E684", {"start": v(-6.35, -16.93) * mm, "mid": v(-6.27, -16.78) * mm, "end": v(-6.2, -16.63) * mm});
            skArc(sketch, "E685", {"start": v(-6.71, -17.47) * mm, "mid": v(-6.52, -17.2) * mm, "end": v(-6.35, -16.93) * mm});
            skArc(sketch, "E686", {"start": v(-7.69, -18.46) * mm, "mid": v(-7.17, -18) * mm, "end": v(-6.71, -17.47) * mm});
            skLineSegment(sketch, "E687", {"start": v(-1.27, -19.96) * mm, "end": v(-2.03, -19.9) * mm});
            skArc(sketch, "E688", {"start": v(-2.4, -18.56) * mm, "mid": v(-2.25, -19.24) * mm, "end": v(-2.03, -19.9) * mm});
            skArc(sketch, "E689", {"start": v(-2.46, -17.58) * mm, "mid": v(-2.88, -17.26) * mm, "end": v(-3.38, -17.42) * mm});
            skArc(sketch, "E690", {"start": v(-2.47, -17.92) * mm, "mid": v(-2.46, -18.24) * mm, "end": v(-2.4, -18.56) * mm});
            skArc(sketch, "E691", {"start": v(-2.46, -17.58) * mm, "mid": v(-2.47, -17.75) * mm, "end": v(-2.47, -17.92) * mm});
            skArc(sketch, "E692", {"start": v(-3.48, -17.75) * mm, "mid": v(-3.43, -17.59) * mm, "end": v(-3.38, -17.42) * mm});
            skArc(sketch, "E693", {"start": v(-3.75, -18.34) * mm, "mid": v(-3.6, -18.05) * mm, "end": v(-3.48, -17.75) * mm});
            skArc(sketch, "E694", {"start": v(-4.54, -19.48) * mm, "mid": v(-4.11, -18.93) * mm, "end": v(-3.75, -18.34) * mm});
            skLineSegment(sketch, "E695", {"start": v(2.03, -19.9) * mm, "end": v(1.27, -19.96) * mm});
            skArc(sketch, "E696", {"start": v(0.68, -18.7) * mm, "mid": v(0.94, -19.35) * mm, "end": v(1.27, -19.96) * mm});
            skArc(sketch, "E697", {"start": v(0.47, -17.74) * mm, "mid": v(0, -17.5) * mm, "end": v(-0.47, -17.74) * mm});
            skArc(sketch, "E698", {"start": v(0.5, -18.08) * mm, "mid": v(0.58, -18.4) * mm, "end": v(0.68, -18.7) * mm});
            skArc(sketch, "E699", {"start": v(0.47, -17.74) * mm, "mid": v(0.48, -17.91) * mm, "end": v(0.5, -18.08) * mm});
            skArc(sketch, "E700", {"start": v(-0.5, -18.08) * mm, "mid": v(-0.48, -17.91) * mm, "end": v(-0.47, -17.74) * mm});
            skArc(sketch, "E701", {"start": v(-0.68, -18.7) * mm, "mid": v(-0.58, -18.4) * mm, "end": v(-0.5, -18.08) * mm});
            skArc(sketch, "E702", {"start": v(-1.27, -19.96) * mm, "mid": v(-0.94, -19.35) * mm, "end": v(-0.68, -18.7) * mm});
            skLineSegment(sketch, "E703", {"start": v(5.28, -19.3) * mm, "end": v(4.54, -19.48) * mm});
            skArc(sketch, "E704", {"start": v(3.75, -18.34) * mm, "mid": v(4.11, -18.93) * mm, "end": v(4.54, -19.48) * mm});
            skArc(sketch, "E705", {"start": v(3.38, -17.42) * mm, "mid": v(2.88, -17.26) * mm, "end": v(2.46, -17.58) * mm});
            skArc(sketch, "E706", {"start": v(3.48, -17.75) * mm, "mid": v(3.6, -18.05) * mm, "end": v(3.75, -18.34) * mm});
            skArc(sketch, "E707", {"start": v(3.38, -17.42) * mm, "mid": v(3.43, -17.59) * mm, "end": v(3.48, -17.75) * mm});
            skArc(sketch, "E708", {"start": v(2.47, -17.92) * mm, "mid": v(2.47, -17.75) * mm, "end": v(2.46, -17.58) * mm});
            skArc(sketch, "E709", {"start": v(2.41, -18.56) * mm, "mid": v(2.46, -18.24) * mm, "end": v(2.47, -17.92) * mm});
            skArc(sketch, "E710", {"start": v(2.03, -19.9) * mm, "mid": v(2.25, -19.24) * mm, "end": v(2.41, -18.56) * mm});
            skLineSegment(sketch, "E711", {"start": v(8.38, -18.16) * mm, "end": v(7.69, -18.46) * mm});
            skArc(sketch, "E712", {"start": v(6.71, -17.47) * mm, "mid": v(7.17, -18) * mm, "end": v(7.69, -18.46) * mm});
            skArc(sketch, "E713", {"start": v(6.2, -16.63) * mm, "mid": v(5.68, -16.55) * mm, "end": v(5.32, -16.93) * mm});
            skArc(sketch, "E714", {"start": v(6.35, -16.93) * mm, "mid": v(6.52, -17.2) * mm, "end": v(6.71, -17.47) * mm});
            skArc(sketch, "E715", {"start": v(6.2, -16.63) * mm, "mid": v(6.27, -16.78) * mm, "end": v(6.35, -16.93) * mm});
            skArc(sketch, "E716", {"start": v(5.39, -17.26) * mm, "mid": v(5.36, -17.1) * mm, "end": v(5.32, -16.93) * mm});
            skArc(sketch, "E717", {"start": v(5.43, -17.9) * mm, "mid": v(5.42, -17.59) * mm, "end": v(5.39, -17.26) * mm});
            skArc(sketch, "E718", {"start": v(5.28, -19.3) * mm, "mid": v(5.4, -18.6) * mm, "end": v(5.43, -17.9) * mm});
            skLineSegment(sketch, "E719", {"start": v(11.25, -16.53) * mm, "end": v(10.62, -16.95) * mm});
            skArc(sketch, "E720", {"start": v(9.5, -16.13) * mm, "mid": v(10.04, -16.57) * mm, "end": v(10.62, -16.95) * mm});
            skArc(sketch, "E721", {"start": v(8.86, -15.38) * mm, "mid": v(8.33, -15.4) * mm, "end": v(8.03, -15.83) * mm});
            skArc(sketch, "E722", {"start": v(9.05, -15.66) * mm, "mid": v(9.26, -15.9) * mm, "end": v(9.5, -16.13) * mm});
            skArc(sketch, "E723", {"start": v(8.86, -15.38) * mm, "mid": v(8.95, -15.52) * mm, "end": v(9.05, -15.66) * mm});
            skArc(sketch, "E724", {"start": v(8.16, -16.14) * mm, "mid": v(8.1, -15.98) * mm, "end": v(8.03, -15.83) * mm});
            skArc(sketch, "E725", {"start": v(8.3, -16.77) * mm, "mid": v(8.24, -16.45) * mm, "end": v(8.16, -16.14) * mm});
            skArc(sketch, "E726", {"start": v(8.38, -18.16) * mm, "mid": v(8.38, -17.46) * mm, "end": v(8.3, -16.77) * mm});
            skLineSegment(sketch, "E727", {"start": v(13.82, -14.46) * mm, "end": v(13.26, -14.97) * mm});
            skArc(sketch, "E728", {"start": v(12.02, -14.34) * mm, "mid": v(12.63, -14.69) * mm, "end": v(13.26, -14.97) * mm});
            skArc(sketch, "E729", {"start": v(11.27, -13.71) * mm, "mid": v(10.75, -13.81) * mm, "end": v(10.53, -14.3) * mm});
            skArc(sketch, "E730", {"start": v(11.5, -13.95) * mm, "mid": v(11.76, -14.16) * mm, "end": v(12.02, -14.34) * mm});
            skArc(sketch, "E731", {"start": v(11.27, -13.71) * mm, "mid": v(11.38, -13.84) * mm, "end": v(11.5, -13.95) * mm});
            skArc(sketch, "E732", {"start": v(10.7, -14.58) * mm, "mid": v(10.62, -14.43) * mm, "end": v(10.53, -14.3) * mm});
            skArc(sketch, "E733", {"start": v(10.95, -15.18) * mm, "mid": v(10.84, -14.87) * mm, "end": v(10.7, -14.58) * mm});
            skArc(sketch, "E734", {"start": v(11.25, -16.53) * mm, "mid": v(11.14, -15.85) * mm, "end": v(10.95, -15.18) * mm});
            skLineSegment(sketch, "E735", {"start": v(16.01, -11.98) * mm, "end": v(15.55, -12.58) * mm});
            skArc(sketch, "E736", {"start": v(14.22, -12.17) * mm, "mid": v(14.87, -12.4) * mm, "end": v(15.55, -12.58) * mm});
            skArc(sketch, "E737", {"start": v(13.37, -11.67) * mm, "mid": v(12.88, -11.85) * mm, "end": v(12.74, -12.36) * mm});
            skArc(sketch, "E738", {"start": v(13.65, -11.87) * mm, "mid": v(13.93, -12.03) * mm, "end": v(14.22, -12.17) * mm});
            skArc(sketch, "E739", {"start": v(13.37, -11.67) * mm, "mid": v(13.5, -11.78) * mm, "end": v(13.65, -11.87) * mm});
            skArc(sketch, "E740", {"start": v(12.96, -12.62) * mm, "mid": v(12.85, -12.49) * mm, "end": v(12.74, -12.36) * mm});
            skArc(sketch, "E741", {"start": v(13.3, -13.17) * mm, "mid": v(13.14, -12.88) * mm, "end": v(12.96, -12.62) * mm});
            skArc(sketch, "E742", {"start": v(13.82, -14.46) * mm, "mid": v(13.6, -13.8) * mm, "end": v(13.3, -13.17) * mm});
            skLineSegment(sketch, "E743", {"start": v(17.77, -9.18) * mm, "end": v(17.4, -9.85) * mm});
            skArc(sketch, "E744", {"start": v(16.03, -9.66) * mm, "mid": v(16.71, -9.8) * mm, "end": v(17.4, -9.85) * mm});
            skArc(sketch, "E745", {"start": v(15.11, -9.31) * mm, "mid": v(14.65, -9.57) * mm, "end": v(14.6, -10.1) * mm});
            skArc(sketch, "E746", {"start": v(15.41, -9.46) * mm, "mid": v(15.72, -9.58) * mm, "end": v(16.03, -9.66) * mm});
            skArc(sketch, "E747", {"start": v(15.11, -9.31) * mm, "mid": v(15.26, -9.4) * mm, "end": v(15.41, -9.46) * mm});
            skArc(sketch, "E748", {"start": v(14.86, -10.31) * mm, "mid": v(14.73, -10.2) * mm, "end": v(14.6, -10.1) * mm});
            skArc(sketch, "E749", {"start": v(15.29, -10.8) * mm, "mid": v(15.08, -10.55) * mm, "end": v(14.86, -10.31) * mm});
            skArc(sketch, "E750", {"start": v(16.01, -11.98) * mm, "mid": v(15.68, -11.37) * mm, "end": v(15.29, -10.8) * mm});
            skLineSegment(sketch, "E751", {"start": v(19.04, -6.13) * mm, "end": v(18.8, -6.85) * mm});
            skArc(sketch, "E752", {"start": v(17.4, -6.9) * mm, "mid": v(18.1, -6.9) * mm, "end": v(18.8, -6.85) * mm});
            skArc(sketch, "E753", {"start": v(16.44, -6.7) * mm, "mid": v(16.03, -7.03) * mm, "end": v(16.06, -7.56) * mm});
            skArc(sketch, "E754", {"start": v(16.76, -6.8) * mm, "mid": v(17.08, -6.86) * mm, "end": v(17.4, -6.9) * mm});
            skArc(sketch, "E755", {"start": v(16.44, -6.7) * mm, "mid": v(16.6, -6.75) * mm, "end": v(16.76, -6.8) * mm});
            skArc(sketch, "E756", {"start": v(16.35, -7.73) * mm, "mid": v(16.2, -7.64) * mm, "end": v(16.06, -7.56) * mm});
            skArc(sketch, "E757", {"start": v(16.86, -8.13) * mm, "mid": v(16.61, -7.92) * mm, "end": v(16.35, -7.73) * mm});
            skArc(sketch, "E758", {"start": v(17.77, -9.18) * mm, "mid": v(17.34, -8.63) * mm, "end": v(16.86, -8.13) * mm});
            skLineSegment(sketch, "E759", {"start": v(19.79, -2.92) * mm, "end": v(19.66, -3.66) * mm});
            skArc(sketch, "E760", {"start": v(18.3, -3.93) * mm, "mid": v(18.99, -3.84) * mm, "end": v(19.66, -3.66) * mm});
            skArc(sketch, "E761", {"start": v(17.32, -3.9) * mm, "mid": v(16.97, -4.3) * mm, "end": v(17.09, -4.81) * mm});
            skArc(sketch, "E762", {"start": v(17.65, -3.95) * mm, "mid": v(17.97, -3.95) * mm, "end": v(18.3, -3.93) * mm});
            skArc(sketch, "E763", {"start": v(17.32, -3.9) * mm, "mid": v(17.48, -3.93) * mm, "end": v(17.65, -3.95) * mm});
            skArc(sketch, "E764", {"start": v(17.4, -4.93) * mm, "mid": v(17.24, -4.87) * mm, "end": v(17.09, -4.81) * mm});
            skArc(sketch, "E765", {"start": v(17.96, -5.25) * mm, "mid": v(17.69, -5.08) * mm, "end": v(17.4, -4.93) * mm});
            skArc(sketch, "E766", {"start": v(19.04, -6.13) * mm, "mid": v(18.52, -5.66) * mm, "end": v(17.96, -5.25) * mm});
            skLineSegment(sketch, "E767", {"start": v(20, 0.38) * mm, "end": v(20, -0.38) * mm});
            skArc(sketch, "E768", {"start": v(18.7, -0.87) * mm, "mid": v(19.36, -0.66) * mm, "end": v(20, -0.38) * mm});
            skArc(sketch, "E769", {"start": v(17.72, -1) * mm, "mid": v(17.44, -1.45) * mm, "end": v(17.64, -1.93) * mm});
            skArc(sketch, "E770", {"start": v(18.06, -0.99) * mm, "mid": v(18.38, -0.94) * mm, "end": v(18.7, -0.87) * mm});
            skArc(sketch, "E771", {"start": v(17.72, -1) * mm, "mid": v(17.9, -1) * mm, "end": v(18.06, -0.99) * mm});
            skArc(sketch, "E772", {"start": v(17.98, -2) * mm, "mid": v(17.81, -1.96) * mm, "end": v(17.64, -1.93) * mm});
            skArc(sketch, "E773", {"start": v(18.58, -2.22) * mm, "mid": v(18.28, -2.1) * mm, "end": v(17.98, -2) * mm});
            skArc(sketch, "E774", {"start": v(19.79, -2.92) * mm, "mid": v(19.2, -2.54) * mm, "end": v(18.58, -2.22) * mm});
            skLineSegment(sketch, "E775", {"start": v(19.66, 3.66) * mm, "end": v(19.79, 2.92) * mm});
            skArc(sketch, "E776", {"start": v(18.58, 2.22) * mm, "mid": v(19.2, 2.54) * mm, "end": v(19.79, 2.92) * mm});
            skArc(sketch, "E777", {"start": v(17.64, 1.93) * mm, "mid": v(17.44, 1.45) * mm, "end": v(17.72, 1) * mm});
            skArc(sketch, "E778", {"start": v(17.98, 2) * mm, "mid": v(18.28, 2.1) * mm, "end": v(18.58, 2.22) * mm});
            skArc(sketch, "E779", {"start": v(17.64, 1.93) * mm, "mid": v(17.81, 1.96) * mm, "end": v(17.98, 2) * mm});
            skArc(sketch, "E780", {"start": v(18.06, 0.99) * mm, "mid": v(17.9, 1) * mm, "end": v(17.72, 1) * mm});
            skArc(sketch, "E781", {"start": v(18.7, 0.87) * mm, "mid": v(18.38, 0.94) * mm, "end": v(18.06, 0.99) * mm});
            skArc(sketch, "E782", {"start": v(20, 0.38) * mm, "mid": v(19.36, 0.66) * mm, "end": v(18.7, 0.87) * mm});
            skLineSegment(sketch, "E783", {"start": v(18.8, 6.85) * mm, "end": v(19.04, 6.13) * mm});
            skArc(sketch, "E784", {"start": v(17.96, 5.25) * mm, "mid": v(18.52, 5.66) * mm, "end": v(19.04, 6.13) * mm});
            skArc(sketch, "E785", {"start": v(17.09, 4.81) * mm, "mid": v(16.97, 4.3) * mm, "end": v(17.32, 3.9) * mm});
            skArc(sketch, "E786", {"start": v(17.4, 4.93) * mm, "mid": v(17.69, 5.08) * mm, "end": v(17.96, 5.25) * mm});
            skArc(sketch, "E787", {"start": v(17.09, 4.81) * mm, "mid": v(17.24, 4.87) * mm, "end": v(17.4, 4.93) * mm});
            skArc(sketch, "E788", {"start": v(17.65, 3.95) * mm, "mid": v(17.48, 3.93) * mm, "end": v(17.32, 3.9) * mm});
            skArc(sketch, "E789", {"start": v(18.3, 3.93) * mm, "mid": v(17.97, 3.95) * mm, "end": v(17.65, 3.95) * mm});
            skArc(sketch, "E790", {"start": v(19.66, 3.66) * mm, "mid": v(18.99, 3.84) * mm, "end": v(18.3, 3.93) * mm});
            skLineSegment(sketch, "E791", {"start": v(17.4, 9.85) * mm, "end": v(17.77, 9.18) * mm});
            skArc(sketch, "E792", {"start": v(16.86, 8.13) * mm, "mid": v(17.34, 8.63) * mm, "end": v(17.77, 9.18) * mm});
            skArc(sketch, "E793", {"start": v(16.06, 7.56) * mm, "mid": v(16.03, 7.03) * mm, "end": v(16.44, 6.7) * mm});
            skArc(sketch, "E794", {"start": v(16.35, 7.73) * mm, "mid": v(16.61, 7.92) * mm, "end": v(16.86, 8.13) * mm});
            skArc(sketch, "E795", {"start": v(16.06, 7.56) * mm, "mid": v(16.2, 7.64) * mm, "end": v(16.35, 7.73) * mm});
            skArc(sketch, "E796", {"start": v(16.76, 6.8) * mm, "mid": v(16.6, 6.75) * mm, "end": v(16.44, 6.7) * mm});
            skArc(sketch, "E797", {"start": v(17.4, 6.9) * mm, "mid": v(17.08, 6.86) * mm, "end": v(16.76, 6.8) * mm});
            skArc(sketch, "E798", {"start": v(18.8, 6.85) * mm, "mid": v(18.1, 6.9) * mm, "end": v(17.4, 6.9) * mm});
            skLineSegment(sketch, "E799", {"start": v(15.55, 12.58) * mm, "end": v(16.01, 11.98) * mm});
            skArc(sketch, "E800", {"start": v(15.29, 10.8) * mm, "mid": v(15.68, 11.37) * mm, "end": v(16.01, 11.98) * mm});
            skArc(sketch, "E801", {"start": v(14.6, 10.1) * mm, "mid": v(14.65, 9.57) * mm, "end": v(15.11, 9.31) * mm});
            skArc(sketch, "E802", {"start": v(14.86, 10.31) * mm, "mid": v(15.08, 10.55) * mm, "end": v(15.29, 10.8) * mm});
            skArc(sketch, "E803", {"start": v(14.6, 10.1) * mm, "mid": v(14.73, 10.2) * mm, "end": v(14.86, 10.31) * mm});
            skArc(sketch, "E804", {"start": v(15.41, 9.46) * mm, "mid": v(15.26, 9.4) * mm, "end": v(15.11, 9.31) * mm});
            skArc(sketch, "E805", {"start": v(16.03, 9.66) * mm, "mid": v(15.72, 9.58) * mm, "end": v(15.41, 9.46) * mm});
            skArc(sketch, "E806", {"start": v(17.4, 9.85) * mm, "mid": v(16.71, 9.8) * mm, "end": v(16.03, 9.66) * mm});
            skLineSegment(sketch, "E807", {"start": v(13.26, 14.97) * mm, "end": v(13.82, 14.46) * mm});
            skArc(sketch, "E808", {"start": v(13.3, 13.17) * mm, "mid": v(13.6, 13.8) * mm, "end": v(13.82, 14.46) * mm});
            skArc(sketch, "E809", {"start": v(12.74, 12.36) * mm, "mid": v(12.88, 11.85) * mm, "end": v(13.37, 11.67) * mm});
            skArc(sketch, "E810", {"start": v(12.96, 12.62) * mm, "mid": v(13.14, 12.88) * mm, "end": v(13.3, 13.17) * mm});
            skArc(sketch, "E811", {"start": v(12.74, 12.36) * mm, "mid": v(12.85, 12.49) * mm, "end": v(12.96, 12.62) * mm});
            skArc(sketch, "E812", {"start": v(13.64, 11.87) * mm, "mid": v(13.5, 11.78) * mm, "end": v(13.37, 11.67) * mm});
            skArc(sketch, "E813", {"start": v(14.22, 12.17) * mm, "mid": v(13.93, 12.03) * mm, "end": v(13.64, 11.87) * mm});
            skArc(sketch, "E814", {"start": v(15.55, 12.58) * mm, "mid": v(14.87, 12.4) * mm, "end": v(14.22, 12.17) * mm});
            skLineSegment(sketch, "E815", {"start": v(10.62, 16.95) * mm, "end": v(11.25, 16.53) * mm});
            skArc(sketch, "E816", {"start": v(10.95, 15.18) * mm, "mid": v(11.14, 15.85) * mm, "end": v(11.25, 16.53) * mm});
            skArc(sketch, "E817", {"start": v(10.53, 14.3) * mm, "mid": v(10.75, 13.81) * mm, "end": v(11.27, 13.71) * mm});
            skArc(sketch, "E818", {"start": v(10.7, 14.58) * mm, "mid": v(10.84, 14.87) * mm, "end": v(10.95, 15.18) * mm});
            skArc(sketch, "E819", {"start": v(10.53, 14.3) * mm, "mid": v(10.62, 14.43) * mm, "end": v(10.7, 14.58) * mm});
            skArc(sketch, "E820", {"start": v(11.5, 13.95) * mm, "mid": v(11.38, 13.84) * mm, "end": v(11.27, 13.71) * mm});
            skArc(sketch, "E821", {"start": v(12.02, 14.34) * mm, "mid": v(11.76, 14.16) * mm, "end": v(11.5, 13.95) * mm});
            skArc(sketch, "E822", {"start": v(13.26, 14.97) * mm, "mid": v(12.63, 14.69) * mm, "end": v(12.02, 14.34) * mm});
            skLineSegment(sketch, "E823", {"start": v(7.69, 18.46) * mm, "end": v(8.38, 18.16) * mm});
            skArc(sketch, "E824", {"start": v(8.3, 16.77) * mm, "mid": v(8.38, 17.46) * mm, "end": v(8.38, 18.16) * mm});
            skArc(sketch, "E825", {"start": v(8.03, 15.83) * mm, "mid": v(8.33, 15.4) * mm, "end": v(8.86, 15.38) * mm});
            skArc(sketch, "E826", {"start": v(8.16, 16.14) * mm, "mid": v(8.24, 16.45) * mm, "end": v(8.3, 16.77) * mm});
            skArc(sketch, "E827", {"start": v(8.03, 15.83) * mm, "mid": v(8.1, 15.98) * mm, "end": v(8.16, 16.14) * mm});
            skArc(sketch, "E828", {"start": v(9.05, 15.66) * mm, "mid": v(8.95, 15.52) * mm, "end": v(8.86, 15.38) * mm});
            skArc(sketch, "E829", {"start": v(9.5, 16.13) * mm, "mid": v(9.26, 15.9) * mm, "end": v(9.05, 15.66) * mm});
            skArc(sketch, "E830", {"start": v(10.62, 16.95) * mm, "mid": v(10.04, 16.57) * mm, "end": v(9.5, 16.13) * mm});
            skLineSegment(sketch, "E831", {"start": v(4.54, 19.48) * mm, "end": v(5.28, 19.3) * mm});
            skArc(sketch, "E832", {"start": v(5.43, 17.9) * mm, "mid": v(5.4, 18.6) * mm, "end": v(5.28, 19.3) * mm});
            skArc(sketch, "E833", {"start": v(5.32, 16.93) * mm, "mid": v(5.68, 16.55) * mm, "end": v(6.2, 16.63) * mm});
            skArc(sketch, "E834", {"start": v(5.39, 17.26) * mm, "mid": v(5.42, 17.59) * mm, "end": v(5.43, 17.9) * mm});
            skArc(sketch, "E835", {"start": v(5.32, 16.93) * mm, "mid": v(5.36, 17.1) * mm, "end": v(5.39, 17.26) * mm});
            skArc(sketch, "E836", {"start": v(6.35, 16.93) * mm, "mid": v(6.27, 16.78) * mm, "end": v(6.2, 16.63) * mm});
            skArc(sketch, "E837", {"start": v(6.71, 17.47) * mm, "mid": v(6.52, 17.2) * mm, "end": v(6.35, 16.93) * mm});
            skArc(sketch, "E838", {"start": v(7.69, 18.46) * mm, "mid": v(7.17, 18) * mm, "end": v(6.71, 17.47) * mm});
            skLineSegment(sketch, "E839", {"start": v(1.27, 19.96) * mm, "end": v(2.03, 19.9) * mm});
            skArc(sketch, "E840", {"start": v(2.4, 18.56) * mm, "mid": v(2.25, 19.24) * mm, "end": v(2.03, 19.9) * mm});
            skArc(sketch, "E841", {"start": v(2.46, 17.58) * mm, "mid": v(2.88, 17.26) * mm, "end": v(3.38, 17.42) * mm});
            skArc(sketch, "E842", {"start": v(2.47, 17.92) * mm, "mid": v(2.46, 18.24) * mm, "end": v(2.4, 18.56) * mm});
            skArc(sketch, "E843", {"start": v(2.46, 17.58) * mm, "mid": v(2.47, 17.75) * mm, "end": v(2.47, 17.92) * mm});
            skArc(sketch, "E844", {"start": v(3.48, 17.75) * mm, "mid": v(3.43, 17.59) * mm, "end": v(3.38, 17.42) * mm});
            skArc(sketch, "E845", {"start": v(3.75, 18.34) * mm, "mid": v(3.6, 18.05) * mm, "end": v(3.48, 17.75) * mm});
            skArc(sketch, "E846", {"start": v(4.54, 19.48) * mm, "mid": v(4.11, 18.93) * mm, "end": v(3.75, 18.34) * mm});
            skLineSegment(sketch, "E847", {"start": v(-2.03, 19.9) * mm, "end": v(-1.27, 19.96) * mm});
            skArc(sketch, "E848", {"start": v(-0.68, 18.7) * mm, "mid": v(-0.94, 19.35) * mm, "end": v(-1.27, 19.96) * mm});
            skArc(sketch, "E849", {"start": v(-0.47, 17.74) * mm, "mid": v(0, 17.5) * mm, "end": v(0.47, 17.74) * mm});
            skArc(sketch, "E850", {"start": v(-0.5, 18.08) * mm, "mid": v(-0.58, 18.4) * mm, "end": v(-0.68, 18.7) * mm});
            skArc(sketch, "E851", {"start": v(-0.47, 17.74) * mm, "mid": v(-0.48, 17.91) * mm, "end": v(-0.5, 18.08) * mm});
            skArc(sketch, "E852", {"start": v(0.5, 18.08) * mm, "mid": v(0.48, 17.91) * mm, "end": v(0.47, 17.74) * mm});
            skArc(sketch, "E853", {"start": v(0.68, 18.7) * mm, "mid": v(0.58, 18.4) * mm, "end": v(0.5, 18.08) * mm});
            skArc(sketch, "E854", {"start": v(1.27, 19.96) * mm, "mid": v(0.94, 19.35) * mm, "end": v(0.68, 18.7) * mm});
            skLineSegment(sketch, "E855", {"start": v(-5.28, 19.3) * mm, "end": v(-4.54, 19.48) * mm});
            skArc(sketch, "E856", {"start": v(-3.75, 18.34) * mm, "mid": v(-4.11, 18.93) * mm, "end": v(-4.54, 19.48) * mm});
            skArc(sketch, "E857", {"start": v(-3.38, 17.42) * mm, "mid": v(-2.88, 17.26) * mm, "end": v(-2.46, 17.58) * mm});
            skArc(sketch, "E858", {"start": v(-3.48, 17.75) * mm, "mid": v(-3.6, 18.05) * mm, "end": v(-3.75, 18.34) * mm});
            skArc(sketch, "E859", {"start": v(-3.38, 17.42) * mm, "mid": v(-3.43, 17.59) * mm, "end": v(-3.48, 17.75) * mm});
            skArc(sketch, "E860", {"start": v(-2.47, 17.92) * mm, "mid": v(-2.47, 17.75) * mm, "end": v(-2.46, 17.58) * mm});
            skArc(sketch, "E861", {"start": v(-2.41, 18.56) * mm, "mid": v(-2.46, 18.24) * mm, "end": v(-2.47, 17.92) * mm});
            skArc(sketch, "E862", {"start": v(-2.03, 19.9) * mm, "mid": v(-2.25, 19.24) * mm, "end": v(-2.41, 18.56) * mm});
            skLineSegment(sketch, "E863", {"start": v(-0.04, 2.42) * mm, "end": v(-0.15, 2.4) * mm});
            skLineSegment(sketch, "E864", {"start": v(0.18, 2.9) * mm, "end": v(0.1, 2.9) * mm});
            skArc(sketch, "E865", {"start": v(0.1, 2.9) * mm, "mid": v(0.02, 2.73) * mm, "end": v(-0.04, 2.55) * mm});
            skLineSegment(sketch, "E866", {"start": v(-0.04, 2.42) * mm, "end": v(-0.04, 2.53) * mm});
            skArc(sketch, "E867", {"start": v(-0.04, 2.55) * mm, "mid": v(-0.04, 2.54) * mm, "end": v(-0.04, 2.53) * mm});
            skLineSegment(sketch, "E868", {"start": v(0.34, 2.4) * mm, "end": v(0.45, 2.37) * mm});
            skLineSegment(sketch, "E869", {"start": v(0.18, 2.9) * mm, "end": v(0.26, 2.89) * mm});
            skArc(sketch, "E870", {"start": v(0.35, 2.53) * mm, "mid": v(0.32, 2.71) * mm, "end": v(0.26, 2.89) * mm});
            skLineSegment(sketch, "E871", {"start": v(0.34, 2.4) * mm, "end": v(0.35, 2.5) * mm});
            skArc(sketch, "E872", {"start": v(0.35, 2.5) * mm, "mid": v(0.35, 2.51) * mm, "end": v(0.35, 2.53) * mm});
            skLineSegment(sketch, "E873", {"start": v(-0.64, 2.33) * mm, "end": v(-0.75, 2.3) * mm});
            skLineSegment(sketch, "E874", {"start": v(-0.54, 2.85) * mm, "end": v(-0.62, 2.83) * mm});
            skArc(sketch, "E875", {"start": v(-0.62, 2.83) * mm, "mid": v(-0.66, 2.65) * mm, "end": v(-0.67, 2.46) * mm});
            skArc(sketch, "E876", {"start": v(-0.28, 2.51) * mm, "mid": v(-0.28, 2.52) * mm, "end": v(-0.28, 2.54) * mm});
            skLineSegment(sketch, "E877", {"start": v(-0.64, 2.33) * mm, "end": v(-0.66, 2.44) * mm});
            skArc(sketch, "E878", {"start": v(-0.67, 2.46) * mm, "mid": v(-0.67, 2.45) * mm, "end": v(-0.66, 2.44) * mm});
            skLineSegment(sketch, "E879", {"start": v(-0.27, 2.4) * mm, "end": v(-0.28, 2.51) * mm});
            skArc(sketch, "E880", {"start": v(-0.28, 2.54) * mm, "mid": v(-0.36, 2.7) * mm, "end": v(-0.47, 2.86) * mm});
            skLineSegment(sketch, "E881", {"start": v(-0.54, 2.85) * mm, "end": v(-0.47, 2.86) * mm});
            skLineSegment(sketch, "E882", {"start": v(-0.27, 2.4) * mm, "end": v(-0.15, 2.4) * mm});
            skLineSegment(sketch, "E883", {"start": v(-1.2, 2.1) * mm, "end": v(-1.3, 2.04) * mm});
            skLineSegment(sketch, "E884", {"start": v(-1.23, 2.62) * mm, "end": v(-1.3, 2.6) * mm});
            skArc(sketch, "E885", {"start": v(-1.3, 2.6) * mm, "mid": v(-1.3, 2.4) * mm, "end": v(-1.26, 2.22) * mm});
            skArc(sketch, "E886", {"start": v(-0.9, 2.36) * mm, "mid": v(-0.9, 2.37) * mm, "end": v(-0.9, 2.39) * mm});
            skLineSegment(sketch, "E887", {"start": v(-1.2, 2.1) * mm, "end": v(-1.25, 2.2) * mm});
            skArc(sketch, "E888", {"start": v(-1.26, 2.22) * mm, "mid": v(-1.26, 2.2) * mm, "end": v(-1.25, 2.2) * mm});
            skLineSegment(sketch, "E889", {"start": v(-0.86, 2.26) * mm, "end": v(-0.9, 2.36) * mm});
            skArc(sketch, "E890", {"start": v(-0.9, 2.39) * mm, "mid": v(-1.02, 2.53) * mm, "end": v(-1.16, 2.66) * mm});
            skLineSegment(sketch, "E891", {"start": v(-1.23, 2.62) * mm, "end": v(-1.16, 2.66) * mm});
            skLineSegment(sketch, "E892", {"start": v(-0.86, 2.26) * mm, "end": v(-0.75, 2.3) * mm});
            skLineSegment(sketch, "E893", {"start": v(-1.68, 1.74) * mm, "end": v(-1.76, 1.65) * mm});
            skLineSegment(sketch, "E894", {"start": v(-1.85, 2.23) * mm, "end": v(-1.9, 2.19) * mm});
            skArc(sketch, "E895", {"start": v(-1.9, 2.19) * mm, "mid": v(-1.86, 2) * mm, "end": v(-1.77, 1.84) * mm});
            skArc(sketch, "E896", {"start": v(-1.45, 2.07) * mm, "mid": v(-1.46, 2.08) * mm, "end": v(-1.47, 2.09) * mm});
            skLineSegment(sketch, "E897", {"start": v(-1.68, 1.74) * mm, "end": v(-1.76, 1.82) * mm});
            skArc(sketch, "E898", {"start": v(-1.77, 1.84) * mm, "mid": v(-1.76, 1.83) * mm, "end": v(-1.76, 1.82) * mm});
            skLineSegment(sketch, "E899", {"start": v(-1.4, 1.98) * mm, "end": v(-1.45, 2.07) * mm});
            skArc(sketch, "E900", {"start": v(-1.47, 2.09) * mm, "mid": v(-1.62, 2.2) * mm, "end": v(-1.79, 2.28) * mm});
            skLineSegment(sketch, "E901", {"start": v(-1.85, 2.23) * mm, "end": v(-1.79, 2.28) * mm});
            skLineSegment(sketch, "E902", {"start": v(-1.4, 1.98) * mm, "end": v(-1.3, 2.04) * mm});
            skLineSegment(sketch, "E903", {"start": v(-2.06, 1.26) * mm, "end": v(-2.12, 1.16) * mm});
            skLineSegment(sketch, "E904", {"start": v(-2.35, 1.7) * mm, "end": v(-2.4, 1.64) * mm});
            skArc(sketch, "E905", {"start": v(-2.4, 1.64) * mm, "mid": v(-2.3, 1.48) * mm, "end": v(-2.17, 1.34) * mm});
            skArc(sketch, "E906", {"start": v(-1.92, 1.64) * mm, "mid": v(-1.93, 1.65) * mm, "end": v(-1.94, 1.65) * mm});
            skLineSegment(sketch, "E907", {"start": v(-2.06, 1.26) * mm, "end": v(-2.15, 1.32) * mm});
            skArc(sketch, "E908", {"start": v(-2.17, 1.34) * mm, "mid": v(-2.16, 1.33) * mm, "end": v(-2.15, 1.32) * mm});
            skLineSegment(sketch, "E909", {"start": v(-1.84, 1.57) * mm, "end": v(-1.92, 1.64) * mm});
            skArc(sketch, "E910", {"start": v(-1.94, 1.65) * mm, "mid": v(-2.12, 1.73) * mm, "end": v(-2.3, 1.77) * mm});
            skLineSegment(sketch, "E911", {"start": v(-2.35, 1.7) * mm, "end": v(-2.3, 1.77) * mm});
            skLineSegment(sketch, "E912", {"start": v(-1.84, 1.57) * mm, "end": v(-1.76, 1.65) * mm});
            skLineSegment(sketch, "E913", {"start": v(-2.31, 0.71) * mm, "end": v(-2.34, 0.6) * mm});
            skLineSegment(sketch, "E914", {"start": v(-2.7, 1.07) * mm, "end": v(-2.72, 1) * mm});
            skArc(sketch, "E915", {"start": v(-2.72, 1) * mm, "mid": v(-2.6, 0.86) * mm, "end": v(-2.44, 0.75) * mm});
            skArc(sketch, "E916", {"start": v(-2.27, 1.1) * mm, "mid": v(-2.28, 1.11) * mm, "end": v(-2.3, 1.12) * mm});
            skLineSegment(sketch, "E917", {"start": v(-2.31, 0.71) * mm, "end": v(-2.41, 0.74) * mm});
            skArc(sketch, "E918", {"start": v(-2.44, 0.75) * mm, "mid": v(-2.43, 0.75) * mm, "end": v(-2.41, 0.74) * mm});
            skLineSegment(sketch, "E919", {"start": v(-2.17, 1.06) * mm, "end": v(-2.27, 1.1) * mm});
            skArc(sketch, "E920", {"start": v(-2.3, 1.12) * mm, "mid": v(-2.48, 1.15) * mm, "end": v(-2.67, 1.14) * mm});
            skLineSegment(sketch, "E921", {"start": v(-2.7, 1.07) * mm, "end": v(-2.67, 1.14) * mm});
            skLineSegment(sketch, "E922", {"start": v(-2.17, 1.06) * mm, "end": v(-2.12, 1.16) * mm});
            skLineSegment(sketch, "E923", {"start": v(-2.41, 0.12) * mm, "end": v(-2.41, 0) * mm});
            skLineSegment(sketch, "E924", {"start": v(-2.88, 0.36) * mm, "end": v(-2.89, 0.29) * mm});
            skArc(sketch, "E925", {"start": v(-2.89, 0.29) * mm, "mid": v(-2.73, 0.2) * mm, "end": v(-2.55, 0.13) * mm});
            skArc(sketch, "E926", {"start": v(-2.47, 0.51) * mm, "mid": v(-2.49, 0.51) * mm, "end": v(-2.5, 0.51) * mm});
            skLineSegment(sketch, "E927", {"start": v(-2.41, 0.12) * mm, "end": v(-2.52, 0.12) * mm});
            skArc(sketch, "E928", {"start": v(-2.55, 0.13) * mm, "mid": v(-2.54, 0.12) * mm, "end": v(-2.52, 0.12) * mm});
            skLineSegment(sketch, "E929", {"start": v(-2.37, 0.49) * mm, "end": v(-2.47, 0.51) * mm});
            skArc(sketch, "E930", {"start": v(-2.5, 0.51) * mm, "mid": v(-2.69, 0.5) * mm, "end": v(-2.87, 0.44) * mm});
            skLineSegment(sketch, "E931", {"start": v(-2.88, 0.36) * mm, "end": v(-2.87, 0.44) * mm});
            skLineSegment(sketch, "E932", {"start": v(-2.37, 0.49) * mm, "end": v(-2.34, 0.6) * mm});
            skLineSegment(sketch, "E933", {"start": v(-2.37, -0.49) * mm, "end": v(-2.34, -0.6) * mm});
            skLineSegment(sketch, "E934", {"start": v(-2.88, -0.36) * mm, "end": v(-2.87, -0.44) * mm});
            skArc(sketch, "E935", {"start": v(-2.87, -0.44) * mm, "mid": v(-2.69, -0.5) * mm, "end": v(-2.5, -0.51) * mm});
            skArc(sketch, "E936", {"start": v(-2.52, -0.12) * mm, "mid": v(-2.54, -0.12) * mm, "end": v(-2.55, -0.13) * mm});
            skLineSegment(sketch, "E937", {"start": v(-2.37, -0.49) * mm, "end": v(-2.47, -0.51) * mm});
            skArc(sketch, "E938", {"start": v(-2.5, -0.51) * mm, "mid": v(-2.49, -0.51) * mm, "end": v(-2.47, -0.51) * mm});
            skLineSegment(sketch, "E939", {"start": v(-2.41, -0.12) * mm, "end": v(-2.52, -0.12) * mm});
            skArc(sketch, "E940", {"start": v(-2.55, -0.13) * mm, "mid": v(-2.73, -0.2) * mm, "end": v(-2.89, -0.29) * mm});
            skLineSegment(sketch, "E941", {"start": v(-2.88, -0.36) * mm, "end": v(-2.89, -0.29) * mm});
            skLineSegment(sketch, "E942", {"start": v(-2.41, -0.12) * mm, "end": v(-2.41, 0) * mm});
            skLineSegment(sketch, "E943", {"start": v(-2.17, -1.06) * mm, "end": v(-2.12, -1.16) * mm});
            skLineSegment(sketch, "E944", {"start": v(-2.7, -1.07) * mm, "end": v(-2.67, -1.14) * mm});
            skArc(sketch, "E945", {"start": v(-2.67, -1.14) * mm, "mid": v(-2.48, -1.15) * mm, "end": v(-2.3, -1.12) * mm});
            skArc(sketch, "E946", {"start": v(-2.41, -0.74) * mm, "mid": v(-2.43, -0.75) * mm, "end": v(-2.44, -0.75) * mm});
            skLineSegment(sketch, "E947", {"start": v(-2.17, -1.06) * mm, "end": v(-2.27, -1.1) * mm});
            skArc(sketch, "E948", {"start": v(-2.3, -1.12) * mm, "mid": v(-2.28, -1.11) * mm, "end": v(-2.27, -1.1) * mm});
            skLineSegment(sketch, "E949", {"start": v(-2.31, -0.71) * mm, "end": v(-2.41, -0.74) * mm});
            skArc(sketch, "E950", {"start": v(-2.44, -0.75) * mm, "mid": v(-2.6, -0.86) * mm, "end": v(-2.72, -1) * mm});
            skLineSegment(sketch, "E951", {"start": v(-2.7, -1.07) * mm, "end": v(-2.72, -1) * mm});
            skLineSegment(sketch, "E952", {"start": v(-2.31, -0.71) * mm, "end": v(-2.34, -0.6) * mm});
            skLineSegment(sketch, "E953", {"start": v(-1.84, -1.57) * mm, "end": v(-1.76, -1.65) * mm});
            skLineSegment(sketch, "E954", {"start": v(-2.35, -1.7) * mm, "end": v(-2.3, -1.77) * mm});
            skArc(sketch, "E955", {"start": v(-2.3, -1.77) * mm, "mid": v(-2.12, -1.73) * mm, "end": v(-1.94, -1.65) * mm});
            skArc(sketch, "E956", {"start": v(-2.15, -1.32) * mm, "mid": v(-2.16, -1.33) * mm, "end": v(-2.17, -1.34) * mm});
            skLineSegment(sketch, "E957", {"start": v(-1.84, -1.57) * mm, "end": v(-1.92, -1.64) * mm});
            skArc(sketch, "E958", {"start": v(-1.94, -1.65) * mm, "mid": v(-1.93, -1.65) * mm, "end": v(-1.92, -1.64) * mm});
            skLineSegment(sketch, "E959", {"start": v(-2.06, -1.26) * mm, "end": v(-2.15, -1.32) * mm});
            skArc(sketch, "E960", {"start": v(-2.17, -1.34) * mm, "mid": v(-2.3, -1.48) * mm, "end": v(-2.4, -1.64) * mm});
            skLineSegment(sketch, "E961", {"start": v(-2.35, -1.7) * mm, "end": v(-2.4, -1.64) * mm});
            skLineSegment(sketch, "E962", {"start": v(-2.06, -1.26) * mm, "end": v(-2.12, -1.16) * mm});
            skLineSegment(sketch, "E963", {"start": v(-1.4, -1.98) * mm, "end": v(-1.3, -2.04) * mm});
            skLineSegment(sketch, "E964", {"start": v(-1.85, -2.23) * mm, "end": v(-1.79, -2.28) * mm});
            skArc(sketch, "E965", {"start": v(-1.79, -2.28) * mm, "mid": v(-1.62, -2.2) * mm, "end": v(-1.47, -2.09) * mm});
            skArc(sketch, "E966", {"start": v(-1.76, -1.82) * mm, "mid": v(-1.76, -1.83) * mm, "end": v(-1.77, -1.84) * mm});
            skLineSegment(sketch, "E967", {"start": v(-1.4, -1.98) * mm, "end": v(-1.45, -2.07) * mm});
            skArc(sketch, "E968", {"start": v(-1.47, -2.09) * mm, "mid": v(-1.46, -2.08) * mm, "end": v(-1.45, -2.07) * mm});
            skLineSegment(sketch, "E969", {"start": v(-1.68, -1.74) * mm, "end": v(-1.76, -1.82) * mm});
            skArc(sketch, "E970", {"start": v(-1.77, -1.84) * mm, "mid": v(-1.86, -2) * mm, "end": v(-1.9, -2.19) * mm});
            skLineSegment(sketch, "E971", {"start": v(-1.85, -2.23) * mm, "end": v(-1.9, -2.19) * mm});
            skLineSegment(sketch, "E972", {"start": v(-1.68, -1.74) * mm, "end": v(-1.76, -1.65) * mm});
            skLineSegment(sketch, "E973", {"start": v(-0.86, -2.26) * mm, "end": v(-0.75, -2.3) * mm});
            skLineSegment(sketch, "E974", {"start": v(-1.23, -2.62) * mm, "end": v(-1.16, -2.66) * mm});
            skArc(sketch, "E975", {"start": v(-1.16, -2.66) * mm, "mid": v(-1.02, -2.53) * mm, "end": v(-0.9, -2.39) * mm});
            skArc(sketch, "E976", {"start": v(-1.25, -2.2) * mm, "mid": v(-1.26, -2.2) * mm, "end": v(-1.26, -2.22) * mm});
            skLineSegment(sketch, "E977", {"start": v(-0.86, -2.26) * mm, "end": v(-0.9, -2.36) * mm});
            skArc(sketch, "E978", {"start": v(-0.9, -2.39) * mm, "mid": v(-0.9, -2.37) * mm, "end": v(-0.9, -2.36) * mm});
            skLineSegment(sketch, "E979", {"start": v(-1.2, -2.1) * mm, "end": v(-1.25, -2.2) * mm});
            skArc(sketch, "E980", {"start": v(-1.26, -2.22) * mm, "mid": v(-1.3, -2.4) * mm, "end": v(-1.3, -2.6) * mm});
            skLineSegment(sketch, "E981", {"start": v(-1.23, -2.62) * mm, "end": v(-1.3, -2.6) * mm});
            skLineSegment(sketch, "E982", {"start": v(-1.2, -2.1) * mm, "end": v(-1.3, -2.04) * mm});
            skLineSegment(sketch, "E983", {"start": v(-0.27, -2.4) * mm, "end": v(-0.15, -2.4) * mm});
            skLineSegment(sketch, "E984", {"start": v(-0.54, -2.85) * mm, "end": v(-0.47, -2.86) * mm});
            skArc(sketch, "E985", {"start": v(-0.47, -2.86) * mm, "mid": v(-0.36, -2.7) * mm, "end": v(-0.28, -2.54) * mm});
            skArc(sketch, "E986", {"start": v(-0.66, -2.44) * mm, "mid": v(-0.67, -2.45) * mm, "end": v(-0.67, -2.46) * mm});
            skLineSegment(sketch, "E987", {"start": v(-0.27, -2.4) * mm, "end": v(-0.28, -2.51) * mm});
            skArc(sketch, "E988", {"start": v(-0.28, -2.54) * mm, "mid": v(-0.28, -2.52) * mm, "end": v(-0.28, -2.51) * mm});
            skLineSegment(sketch, "E989", {"start": v(-0.64, -2.33) * mm, "end": v(-0.66, -2.44) * mm});
            skArc(sketch, "E990", {"start": v(-0.67, -2.46) * mm, "mid": v(-0.66, -2.65) * mm, "end": v(-0.62, -2.83) * mm});
            skLineSegment(sketch, "E991", {"start": v(-0.54, -2.85) * mm, "end": v(-0.62, -2.83) * mm});
            skLineSegment(sketch, "E992", {"start": v(-0.64, -2.33) * mm, "end": v(-0.75, -2.3) * mm});
            skLineSegment(sketch, "E993", {"start": v(0.34, -2.4) * mm, "end": v(0.45, -2.37) * mm});
            skLineSegment(sketch, "E994", {"start": v(0.18, -2.9) * mm, "end": v(0.26, -2.89) * mm});
            skArc(sketch, "E995", {"start": v(0.26, -2.89) * mm, "mid": v(0.32, -2.71) * mm, "end": v(0.35, -2.53) * mm});
            skArc(sketch, "E996", {"start": v(-0.04, -2.53) * mm, "mid": v(-0.04, -2.54) * mm, "end": v(-0.04, -2.55) * mm});
            skLineSegment(sketch, "E997", {"start": v(0.34, -2.4) * mm, "end": v(0.35, -2.5) * mm});
            skArc(sketch, "E998", {"start": v(0.35, -2.53) * mm, "mid": v(0.35, -2.51) * mm, "end": v(0.35, -2.5) * mm});
            skLineSegment(sketch, "E999", {"start": v(-0.04, -2.42) * mm, "end": v(-0.04, -2.53) * mm});
            skArc(sketch, "E1000", {"start": v(-0.04, -2.55) * mm, "mid": v(0.02, -2.73) * mm, "end": v(0.1, -2.9) * mm});
            skLineSegment(sketch, "E1001", {"start": v(0.18, -2.9) * mm, "end": v(0.1, -2.9) * mm});
            skLineSegment(sketch, "E1002", {"start": v(-0.04, -2.42) * mm, "end": v(-0.15, -2.4) * mm});
            skLineSegment(sketch, "E1003", {"start": v(0.92, -2.23) * mm, "end": v(1.03, -2.18) * mm});
            skLineSegment(sketch, "E1004", {"start": v(0.9, -2.76) * mm, "end": v(0.97, -2.73) * mm});
            skArc(sketch, "E1005", {"start": v(0.97, -2.73) * mm, "mid": v(0.99, -2.55) * mm, "end": v(0.97, -2.36) * mm});
            skArc(sketch, "E1006", {"start": v(0.6, -2.46) * mm, "mid": v(0.6, -2.47) * mm, "end": v(0.6, -2.48) * mm});
            skLineSegment(sketch, "E1007", {"start": v(0.92, -2.23) * mm, "end": v(0.96, -2.33) * mm});
            skArc(sketch, "E1008", {"start": v(0.97, -2.36) * mm, "mid": v(0.97, -2.35) * mm, "end": v(0.96, -2.33) * mm});
            skLineSegment(sketch, "E1009", {"start": v(0.57, -2.35) * mm, "end": v(0.6, -2.46) * mm});
            skArc(sketch, "E1010", {"start": v(0.6, -2.48) * mm, "mid": v(0.7, -2.64) * mm, "end": v(0.82, -2.78) * mm});
            skLineSegment(sketch, "E1011", {"start": v(0.9, -2.76) * mm, "end": v(0.82, -2.78) * mm});
            skLineSegment(sketch, "E1012", {"start": v(0.57, -2.35) * mm, "end": v(0.45, -2.37) * mm});
            skLineSegment(sketch, "E1013", {"start": v(1.45, -1.93) * mm, "end": v(1.54, -1.86) * mm});
            skLineSegment(sketch, "E1014", {"start": v(1.55, -2.45) * mm, "end": v(1.62, -2.4) * mm});
            skArc(sketch, "E1015", {"start": v(1.62, -2.4) * mm, "mid": v(1.6, -2.22) * mm, "end": v(1.53, -2.04) * mm});
            skArc(sketch, "E1016", {"start": v(1.18, -2.23) * mm, "mid": v(1.2, -2.24) * mm, "end": v(1.2, -2.25) * mm});
            skLineSegment(sketch, "E1017", {"start": v(1.45, -1.93) * mm, "end": v(1.51, -2.02) * mm});
            skArc(sketch, "E1018", {"start": v(1.53, -2.04) * mm, "mid": v(1.52, -2.03) * mm, "end": v(1.51, -2.02) * mm});
            skLineSegment(sketch, "E1019", {"start": v(1.13, -2.14) * mm, "end": v(1.18, -2.23) * mm});
            skArc(sketch, "E1020", {"start": v(1.2, -2.25) * mm, "mid": v(1.33, -2.38) * mm, "end": v(1.49, -2.49) * mm});
            skLineSegment(sketch, "E1021", {"start": v(1.55, -2.45) * mm, "end": v(1.49, -2.49) * mm});
            skLineSegment(sketch, "E1022", {"start": v(1.13, -2.14) * mm, "end": v(1.03, -2.18) * mm});
            skLineSegment(sketch, "E1023", {"start": v(1.89, -1.51) * mm, "end": v(1.95, -1.42) * mm});
            skLineSegment(sketch, "E1024", {"start": v(2.11, -1.99) * mm, "end": v(2.17, -1.93) * mm});
            skArc(sketch, "E1025", {"start": v(2.17, -1.93) * mm, "mid": v(2.1, -1.76) * mm, "end": v(1.99, -1.6) * mm});
            skArc(sketch, "E1026", {"start": v(1.7, -1.87) * mm, "mid": v(1.71, -1.88) * mm, "end": v(1.72, -1.88) * mm});
            skLineSegment(sketch, "E1027", {"start": v(1.89, -1.51) * mm, "end": v(1.97, -1.58) * mm});
            skArc(sketch, "E1028", {"start": v(1.99, -1.6) * mm, "mid": v(1.98, -1.59) * mm, "end": v(1.97, -1.58) * mm});
            skLineSegment(sketch, "E1029", {"start": v(1.63, -1.79) * mm, "end": v(1.7, -1.87) * mm});
            skArc(sketch, "E1030", {"start": v(1.72, -1.88) * mm, "mid": v(1.88, -1.98) * mm, "end": v(2.06, -2.04) * mm});
            skLineSegment(sketch, "E1031", {"start": v(2.11, -1.99) * mm, "end": v(2.06, -2.04) * mm});
            skLineSegment(sketch, "E1032", {"start": v(1.63, -1.79) * mm, "end": v(1.54, -1.86) * mm});
            skLineSegment(sketch, "E1033", {"start": v(2.2, -1) * mm, "end": v(2.25, -0.89) * mm});
            skLineSegment(sketch, "E1034", {"start": v(2.54, -1.4) * mm, "end": v(2.58, -1.33) * mm});
            skArc(sketch, "E1035", {"start": v(2.58, -1.33) * mm, "mid": v(2.46, -1.18) * mm, "end": v(2.32, -1.05) * mm});
            skArc(sketch, "E1036", {"start": v(2.11, -1.38) * mm, "mid": v(2.12, -1.4) * mm, "end": v(2.14, -1.4) * mm});
            skLineSegment(sketch, "E1037", {"start": v(2.2, -1) * mm, "end": v(2.3, -1.04) * mm});
            skArc(sketch, "E1038", {"start": v(2.32, -1.05) * mm, "mid": v(2.31, -1.05) * mm, "end": v(2.3, -1.04) * mm});
            skLineSegment(sketch, "E1039", {"start": v(2.02, -1.33) * mm, "end": v(2.11, -1.38) * mm});
            skArc(sketch, "E1040", {"start": v(2.14, -1.4) * mm, "mid": v(2.32, -1.45) * mm, "end": v(2.5, -1.46) * mm});
            skLineSegment(sketch, "E1041", {"start": v(2.54, -1.4) * mm, "end": v(2.5, -1.46) * mm});
            skLineSegment(sketch, "E1042", {"start": v(2.02, -1.33) * mm, "end": v(1.95, -1.42) * mm});
            skLineSegment(sketch, "E1043", {"start": v(2.38, -0.42) * mm, "end": v(2.4, -0.3) * mm});
            skLineSegment(sketch, "E1044", {"start": v(2.8, -0.72) * mm, "end": v(2.83, -0.65) * mm});
            skArc(sketch, "E1045", {"start": v(2.83, -0.65) * mm, "mid": v(2.68, -0.53) * mm, "end": v(2.51, -0.44) * mm});
            skArc(sketch, "E1046", {"start": v(2.4, -0.82) * mm, "mid": v(2.4, -0.82) * mm, "end": v(2.42, -0.82) * mm});
            skLineSegment(sketch, "E1047", {"start": v(2.38, -0.42) * mm, "end": v(2.49, -0.44) * mm});
            skArc(sketch, "E1048", {"start": v(2.51, -0.44) * mm, "mid": v(2.5, -0.44) * mm, "end": v(2.49, -0.44) * mm});
            skLineSegment(sketch, "E1049", {"start": v(2.29, -0.78) * mm, "end": v(2.4, -0.82) * mm});
            skArc(sketch, "E1050", {"start": v(2.42, -0.82) * mm, "mid": v(2.6, -0.83) * mm, "end": v(2.79, -0.8) * mm});
            skLineSegment(sketch, "E1051", {"start": v(2.8, -0.72) * mm, "end": v(2.79, -0.8) * mm});
            skLineSegment(sketch, "E1052", {"start": v(2.29, -0.78) * mm, "end": v(2.25, -0.89) * mm});
            skLineSegment(sketch, "E1053", {"start": v(2.41, 0.19) * mm, "end": v(2.4, 0.3) * mm});
            skLineSegment(sketch, "E1054", {"start": v(2.9, 0) * mm, "end": v(2.9, 0.08) * mm});
            skArc(sketch, "E1055", {"start": v(2.9, 0.08) * mm, "mid": v(2.73, 0.15) * mm, "end": v(2.54, 0.2) * mm});
            skArc(sketch, "E1056", {"start": v(2.52, -0.2) * mm, "mid": v(2.53, -0.2) * mm, "end": v(2.54, -0.2) * mm});
            skLineSegment(sketch, "E1057", {"start": v(2.41, 0.19) * mm, "end": v(2.52, 0.2) * mm});
            skArc(sketch, "E1058", {"start": v(2.54, 0.2) * mm, "mid": v(2.53, 0.2) * mm, "end": v(2.52, 0.2) * mm});
            skLineSegment(sketch, "E1059", {"start": v(2.41, -0.19) * mm, "end": v(2.52, -0.2) * mm});
            skArc(sketch, "E1060", {"start": v(2.54, -0.2) * mm, "mid": v(2.73, -0.15) * mm, "end": v(2.9, -0.08) * mm});
            skLineSegment(sketch, "E1061", {"start": v(2.9, 0) * mm, "end": v(2.9, -0.08) * mm});
            skLineSegment(sketch, "E1062", {"start": v(2.41, -0.19) * mm, "end": v(2.4, -0.3) * mm});
            skLineSegment(sketch, "E1063", {"start": v(2.29, 0.78) * mm, "end": v(2.25, 0.89) * mm});
            skLineSegment(sketch, "E1064", {"start": v(2.8, 0.72) * mm, "end": v(2.79, 0.8) * mm});
            skArc(sketch, "E1065", {"start": v(2.79, 0.8) * mm, "mid": v(2.6, 0.83) * mm, "end": v(2.42, 0.82) * mm});
            skArc(sketch, "E1066", {"start": v(2.49, 0.44) * mm, "mid": v(2.5, 0.44) * mm, "end": v(2.51, 0.44) * mm});
            skLineSegment(sketch, "E1067", {"start": v(2.29, 0.78) * mm, "end": v(2.4, 0.82) * mm});
            skArc(sketch, "E1068", {"start": v(2.42, 0.82) * mm, "mid": v(2.4, 0.82) * mm, "end": v(2.4, 0.82) * mm});
            skLineSegment(sketch, "E1069", {"start": v(2.38, 0.42) * mm, "end": v(2.49, 0.44) * mm});
            skArc(sketch, "E1070", {"start": v(2.51, 0.44) * mm, "mid": v(2.68, 0.53) * mm, "end": v(2.83, 0.65) * mm});
            skLineSegment(sketch, "E1071", {"start": v(2.8, 0.72) * mm, "end": v(2.83, 0.65) * mm});
            skLineSegment(sketch, "E1072", {"start": v(2.38, 0.42) * mm, "end": v(2.4, 0.3) * mm});
            skLineSegment(sketch, "E1073", {"start": v(2.02, 1.33) * mm, "end": v(1.95, 1.42) * mm});
            skLineSegment(sketch, "E1074", {"start": v(2.54, 1.4) * mm, "end": v(2.5, 1.46) * mm});
            skArc(sketch, "E1075", {"start": v(2.5, 1.46) * mm, "mid": v(2.32, 1.45) * mm, "end": v(2.14, 1.4) * mm});
            skArc(sketch, "E1076", {"start": v(2.3, 1.04) * mm, "mid": v(2.31, 1.05) * mm, "end": v(2.32, 1.05) * mm});
            skLineSegment(sketch, "E1077", {"start": v(2.02, 1.33) * mm, "end": v(2.11, 1.38) * mm});
            skArc(sketch, "E1078", {"start": v(2.14, 1.4) * mm, "mid": v(2.12, 1.4) * mm, "end": v(2.11, 1.38) * mm});
            skLineSegment(sketch, "E1079", {"start": v(2.2, 1) * mm, "end": v(2.3, 1.04) * mm});
            skArc(sketch, "E1080", {"start": v(2.32, 1.05) * mm, "mid": v(2.46, 1.18) * mm, "end": v(2.58, 1.33) * mm});
            skLineSegment(sketch, "E1081", {"start": v(2.54, 1.4) * mm, "end": v(2.58, 1.33) * mm});
            skLineSegment(sketch, "E1082", {"start": v(2.2, 1) * mm, "end": v(2.25, 0.89) * mm});
            skLineSegment(sketch, "E1083", {"start": v(1.63, 1.79) * mm, "end": v(1.54, 1.86) * mm});
            skLineSegment(sketch, "E1084", {"start": v(2.11, 1.99) * mm, "end": v(2.06, 2.04) * mm});
            skArc(sketch, "E1085", {"start": v(2.06, 2.04) * mm, "mid": v(1.88, 1.98) * mm, "end": v(1.72, 1.88) * mm});
            skArc(sketch, "E1086", {"start": v(1.97, 1.58) * mm, "mid": v(1.98, 1.59) * mm, "end": v(1.99, 1.6) * mm});
            skLineSegment(sketch, "E1087", {"start": v(1.63, 1.79) * mm, "end": v(1.7, 1.87) * mm});
            skArc(sketch, "E1088", {"start": v(1.72, 1.88) * mm, "mid": v(1.71, 1.88) * mm, "end": v(1.7, 1.87) * mm});
            skLineSegment(sketch, "E1089", {"start": v(1.89, 1.51) * mm, "end": v(1.97, 1.58) * mm});
            skArc(sketch, "E1090", {"start": v(1.99, 1.6) * mm, "mid": v(2.1, 1.76) * mm, "end": v(2.17, 1.93) * mm});
            skLineSegment(sketch, "E1091", {"start": v(2.11, 1.99) * mm, "end": v(2.17, 1.93) * mm});
            skLineSegment(sketch, "E1092", {"start": v(1.89, 1.51) * mm, "end": v(1.95, 1.42) * mm});
            skLineSegment(sketch, "E1093", {"start": v(1.13, 2.14) * mm, "end": v(1.03, 2.18) * mm});
            skLineSegment(sketch, "E1094", {"start": v(1.55, 2.45) * mm, "end": v(1.49, 2.49) * mm});
            skArc(sketch, "E1095", {"start": v(1.49, 2.49) * mm, "mid": v(1.33, 2.38) * mm, "end": v(1.2, 2.25) * mm});
            skArc(sketch, "E1096", {"start": v(1.51, 2.02) * mm, "mid": v(1.52, 2.03) * mm, "end": v(1.53, 2.04) * mm});
            skLineSegment(sketch, "E1097", {"start": v(1.13, 2.14) * mm, "end": v(1.18, 2.23) * mm});
            skArc(sketch, "E1098", {"start": v(1.2, 2.25) * mm, "mid": v(1.2, 2.24) * mm, "end": v(1.18, 2.23) * mm});
            skLineSegment(sketch, "E1099", {"start": v(1.45, 1.93) * mm, "end": v(1.51, 2.02) * mm});
            skArc(sketch, "E1100", {"start": v(1.53, 2.04) * mm, "mid": v(1.6, 2.22) * mm, "end": v(1.62, 2.4) * mm});
            skLineSegment(sketch, "E1101", {"start": v(1.55, 2.45) * mm, "end": v(1.62, 2.4) * mm});
            skLineSegment(sketch, "E1102", {"start": v(1.45, 1.93) * mm, "end": v(1.54, 1.86) * mm});
            skLineSegment(sketch, "E1103", {"start": v(0.57, 2.35) * mm, "end": v(0.45, 2.37) * mm});
            skLineSegment(sketch, "E1104", {"start": v(0.9, 2.76) * mm, "end": v(0.82, 2.78) * mm});
            skArc(sketch, "E1105", {"start": v(0.82, 2.78) * mm, "mid": v(0.7, 2.64) * mm, "end": v(0.6, 2.48) * mm});
            skArc(sketch, "E1106", {"start": v(0.96, 2.33) * mm, "mid": v(0.97, 2.35) * mm, "end": v(0.97, 2.36) * mm});
            skLineSegment(sketch, "E1107", {"start": v(0.57, 2.35) * mm, "end": v(0.6, 2.46) * mm});
            skArc(sketch, "E1108", {"start": v(0.6, 2.48) * mm, "mid": v(0.6, 2.47) * mm, "end": v(0.6, 2.46) * mm});
            skLineSegment(sketch, "E1109", {"start": v(0.92, 2.23) * mm, "end": v(0.96, 2.33) * mm});
            skArc(sketch, "E1110", {"start": v(0.97, 2.36) * mm, "mid": v(0.99, 2.55) * mm, "end": v(0.97, 2.73) * mm});
            skLineSegment(sketch, "E1111", {"start": v(0.9, 2.76) * mm, "end": v(0.97, 2.73) * mm});
            skLineSegment(sketch, "E1112", {"start": v(0.92, 2.23) * mm, "end": v(1.03, 2.18) * mm});
            skCircle(sketch, "E1113", {"center": v(0, 0) * mm, "radius": 1 * mm});
            skSolve(sketch);
        }
        {
            var Q0;
            {var subQ0=sQuery(id+"F2.wireOp",EDGE,"E559");Q0=makeQuery(id+"F2.imprint","IMPRINT",FACE,{"disambiguationData":[TD([[makeQuery(id+"F2.imprint","IMPRINT",EDGE,{"derivedFrom":subQ0}),-1.0]])]});}
            var sketch = newSketch(context, id + "F3", { "sketchPlane" : qUnion([Q0])});
            skSolve(sketch);
        }
        {
            var Q0;
            Q0 = qSketchRegion(id + "F3", true);
            var Q1;
            Q1=makeQuery(id+"F2.imprint","IMPRINT",FACE,{"disambiguationData":[TD([[makeQuery(id+"F2.imprint","IMPRINT",EDGE,{"derivedFrom":sQuery(id+"F2.wireOp",EDGE,"E863")}),1.0]])]});
            extrude(context, id + "F4", {"entities" : qUnion([Q0, Q1]), "operationType" : NewBodyOperationType.ADD, "oppositeDirection" : true, "depth" : 20 * mm});
        }
        {
            var Q0;
            {var subQ0=sQuery(id+"F2.wireOp",EDGE,"E559");Q0=makeQuery(id+"F3.imprint","IMPRINT",FACE,{"disambiguationData":[TD([[makeQuery(id+"F3.imprint","IMPRINT",EDGE,{"derivedFrom":makeQuery(id+"F2.imprint","IMPRINT",EDGE,{"derivedFrom":subQ0})}),-1.0]])]});}
            var sketch = newSketch(context, id + "F5", { "sketchPlane" : qUnion([Q0])});
            skCircle(sketch, "E1114", {"center": v(0, 0) * mm, "radius": 1.65 * mm});
            skSolve(sketch);
        }
        {
            var Q0;
            Q0=makeQuery(id+"F5.imprint","IMPRINT",FACE,{"disambiguationData":[TD([[makeQuery(id+"F5.imprint","IMPRINT",EDGE,{"derivedFrom":sQuery(id+"F5.wireOp",EDGE,"E1114")}),1.0]])]});
            extrude(context, id + "F6", {"entities" : qUnion([Q0]), "operationType" : NewBodyOperationType.REMOVE, "oppositeDirection" : true, "depth" : 25 * mm});
        }
        {
            var Q0;
            {var subQ0=sQuery(id+"F2.wireOp",EDGE,"E559");Q0=makeQuery(id+"F3.imprint","IMPRINT",FACE,{"disambiguationData":[TD([[makeQuery(id+"F3.imprint","IMPRINT",EDGE,{"derivedFrom":makeQuery(id+"F2.imprint","IMPRINT",EDGE,{"derivedFrom":subQ0})}),-1.0]])]});}
            extrude(context, id + "F7", {"entities" : qUnion([Q0]), "operationType" : NewBodyOperationType.REMOVE, "depth" : 10 * mm});
        }
        {
            var Q0;
            Q0=makeQuery(id+"F4.boolean.opBoolean","MERGE",FACE,{"derivedFrom":[makeQuery(id+"F1.opExtrude","CAP_FACE",FACE,{"disambiguationData":[OSD([sQuery(id+"F0.wireOp",EDGE,"E0"),sQuery(id+"F0.wireOp",EDGE,"E1"),sQuery(id+"F0.wireOp",EDGE,"E2"),sQuery(id+"F0.wireOp",EDGE,"E3"),sQuery(id+"F0.wireOp",EDGE,"E4"),sQuery(id+"F0.wireOp",EDGE,"E5"),sQuery(id+"F0.wireOp",EDGE,"E6"),sQuery(id+"F0.wireOp",EDGE,"E7"),sQuery(id+"F0.wireOp",EDGE,"E8"),sQuery(id+"F0.wireOp",EDGE,"E9"),sQuery(id+"F0.wireOp",EDGE,"E10"),sQuery(id+"F0.wireOp",EDGE,"E11"),sQuery(id+"F0.wireOp",EDGE,"E12"),sQuery(id+"F0.wireOp",EDGE,"E13"),sQuery(id+"F0.wireOp",EDGE,"E14"),sQuery(id+"F0.wireOp",EDGE,"E15"),sQuery(id+"F0.wireOp",EDGE,"E16"),sQuery(id+"F0.wireOp",EDGE,"E17"),sQuery(id+"F0.wireOp",EDGE,"E18"),sQuery(id+"F0.wireOp",EDGE,"E19"),sQuery(id+"F0.wireOp",EDGE,"E20"),sQuery(id+"F0.wireOp",EDGE,"E21"),sQuery(id+"F0.wireOp",EDGE,"E22"),sQuery(id+"F0.wireOp",EDGE,"E23"),sQuery(id+"F0.wireOp",EDGE,"E24"),sQuery(id+"F0.wireOp",EDGE,"E25"),sQuery(id+"F0.wireOp",EDGE,"E26"),sQuery(id+"F0.wireOp",EDGE,"E27"),sQuery(id+"F0.wireOp",EDGE,"E28"),sQuery(id+"F0.wireOp",EDGE,"E29"),sQuery(id+"F0.wireOp",EDGE,"E30"),sQuery(id+"F0.wireOp",EDGE,"E31"),sQuery(id+"F0.wireOp",EDGE,"E32"),sQuery(id+"F0.wireOp",EDGE,"E33"),sQuery(id+"F0.wireOp",EDGE,"E34"),sQuery(id+"F0.wireOp",EDGE,"E35"),sQuery(id+"F0.wireOp",EDGE,"E36"),sQuery(id+"F0.wireOp",EDGE,"E37"),sQuery(id+"F0.wireOp",EDGE,"E38"),sQuery(id+"F0.wireOp",EDGE,"E39"),sQuery(id+"F0.wireOp",EDGE,"E40"),sQuery(id+"F0.wireOp",EDGE,"E41"),sQuery(id+"F0.wireOp",EDGE,"E42"),sQuery(id+"F0.wireOp",EDGE,"E43"),sQuery(id+"F0.wireOp",EDGE,"E44"),sQuery(id+"F0.wireOp",EDGE,"E45"),sQuery(id+"F0.wireOp",EDGE,"E46"),sQuery(id+"F0.wireOp",EDGE,"E47"),sQuery(id+"F0.wireOp",EDGE,"E48"),sQuery(id+"F0.wireOp",EDGE,"E49"),sQuery(id+"F0.wireOp",EDGE,"E50"),sQuery(id+"F0.wireOp",EDGE,"E51"),sQuery(id+"F0.wireOp",EDGE,"E52"),sQuery(id+"F0.wireOp",EDGE,"E53"),sQuery(id+"F0.wireOp",EDGE,"E54"),sQuery(id+"F0.wireOp",EDGE,"E55"),sQuery(id+"F0.wireOp",EDGE,"E56"),sQuery(id+"F0.wireOp",EDGE,"E57"),sQuery(id+"F0.wireOp",EDGE,"E58"),sQuery(id+"F0.wireOp",EDGE,"E59"),sQuery(id+"F0.wireOp",EDGE,"E60"),sQuery(id+"F0.wireOp",EDGE,"E61"),sQuery(id+"F0.wireOp",EDGE,"E62"),sQuery(id+"F0.wireOp",EDGE,"E63"),sQuery(id+"F0.wireOp",EDGE,"E64"),sQuery(id+"F0.wireOp",EDGE,"E65"),sQuery(id+"F0.wireOp",EDGE,"E66"),sQuery(id+"F0.wireOp",EDGE,"E67"),sQuery(id+"F0.wireOp",EDGE,"E68"),sQuery(id+"F0.wireOp",EDGE,"E69"),sQuery(id+"F0.wireOp",EDGE,"E70"),sQuery(id+"F0.wireOp",EDGE,"E71"),sQuery(id+"F0.wireOp",EDGE,"E72"),sQuery(id+"F0.wireOp",EDGE,"E73"),sQuery(id+"F0.wireOp",EDGE,"E74"),sQuery(id+"F0.wireOp",EDGE,"E75"),sQuery(id+"F0.wireOp",EDGE,"E76"),sQuery(id+"F0.wireOp",EDGE,"E77"),sQuery(id+"F0.wireOp",EDGE,"E78"),sQuery(id+"F0.wireOp",EDGE,"E79"),sQuery(id+"F0.wireOp",EDGE,"E80"),sQuery(id+"F0.wireOp",EDGE,"E81"),sQuery(id+"F0.wireOp",EDGE,"E82"),sQuery(id+"F0.wireOp",EDGE,"E83"),sQuery(id+"F0.wireOp",EDGE,"E84"),sQuery(id+"F0.wireOp",EDGE,"E85"),sQuery(id+"F0.wireOp",EDGE,"E86"),sQuery(id+"F0.wireOp",EDGE,"E87"),sQuery(id+"F0.wireOp",EDGE,"E88"),sQuery(id+"F0.wireOp",EDGE,"E89"),sQuery(id+"F0.wireOp",EDGE,"E90"),sQuery(id+"F0.wireOp",EDGE,"E91"),sQuery(id+"F0.wireOp",EDGE,"E92"),sQuery(id+"F0.wireOp",EDGE,"E93"),sQuery(id+"F0.wireOp",EDGE,"E94"),sQuery(id+"F0.wireOp",EDGE,"E95"),sQuery(id+"F0.wireOp",EDGE,"E96"),sQuery(id+"F0.wireOp",EDGE,"E97"),sQuery(id+"F0.wireOp",EDGE,"E98"),sQuery(id+"F0.wireOp",EDGE,"E99"),sQuery(id+"F0.wireOp",EDGE,"E100"),sQuery(id+"F0.wireOp",EDGE,"E101"),sQuery(id+"F0.wireOp",EDGE,"E102"),sQuery(id+"F0.wireOp",EDGE,"E103"),sQuery(id+"F0.wireOp",EDGE,"E104"),sQuery(id+"F0.wireOp",EDGE,"E105"),sQuery(id+"F0.wireOp",EDGE,"E106"),sQuery(id+"F0.wireOp",EDGE,"E107"),sQuery(id+"F0.wireOp",EDGE,"E108"),sQuery(id+"F0.wireOp",EDGE,"E109"),sQuery(id+"F0.wireOp",EDGE,"E110"),sQuery(id+"F0.wireOp",EDGE,"E111"),sQuery(id+"F0.wireOp",EDGE,"E112"),sQuery(id+"F0.wireOp",EDGE,"E113"),sQuery(id+"F0.wireOp",EDGE,"E114"),sQuery(id+"F0.wireOp",EDGE,"E115"),sQuery(id+"F0.wireOp",EDGE,"E116"),sQuery(id+"F0.wireOp",EDGE,"E117"),sQuery(id+"F0.wireOp",EDGE,"E118"),sQuery(id+"F0.wireOp",EDGE,"E119"),sQuery(id+"F0.wireOp",EDGE,"E120"),sQuery(id+"F0.wireOp",EDGE,"E121"),sQuery(id+"F0.wireOp",EDGE,"E122"),sQuery(id+"F0.wireOp",EDGE,"E123"),sQuery(id+"F0.wireOp",EDGE,"E124"),sQuery(id+"F0.wireOp",EDGE,"E125"),sQuery(id+"F0.wireOp",EDGE,"E126"),sQuery(id+"F0.wireOp",EDGE,"E127"),sQuery(id+"F0.wireOp",EDGE,"E128"),sQuery(id+"F0.wireOp",EDGE,"E129"),sQuery(id+"F0.wireOp",EDGE,"E130"),sQuery(id+"F0.wireOp",EDGE,"E131"),sQuery(id+"F0.wireOp",EDGE,"E132"),sQuery(id+"F0.wireOp",EDGE,"E133"),sQuery(id+"F0.wireOp",EDGE,"E134"),sQuery(id+"F0.wireOp",EDGE,"E135"),sQuery(id+"F0.wireOp",EDGE,"E136"),sQuery(id+"F0.wireOp",EDGE,"E137"),sQuery(id+"F0.wireOp",EDGE,"E138"),sQuery(id+"F0.wireOp",EDGE,"E139"),sQuery(id+"F0.wireOp",EDGE,"E140"),sQuery(id+"F0.wireOp",EDGE,"E141"),sQuery(id+"F0.wireOp",EDGE,"E142"),sQuery(id+"F0.wireOp",EDGE,"E143"),sQuery(id+"F0.wireOp",EDGE,"E144"),sQuery(id+"F0.wireOp",EDGE,"E145"),sQuery(id+"F0.wireOp",EDGE,"E146"),sQuery(id+"F0.wireOp",EDGE,"E147"),sQuery(id+"F0.wireOp",EDGE,"E148"),sQuery(id+"F0.wireOp",EDGE,"E149"),sQuery(id+"F0.wireOp",EDGE,"E150"),sQuery(id+"F0.wireOp",EDGE,"E151"),sQuery(id+"F0.wireOp",EDGE,"E152"),sQuery(id+"F0.wireOp",EDGE,"E153"),sQuery(id+"F0.wireOp",EDGE,"E154"),sQuery(id+"F0.wireOp",EDGE,"E155"),sQuery(id+"F0.wireOp",EDGE,"E156"),sQuery(id+"F0.wireOp",EDGE,"E157"),sQuery(id+"F0.wireOp",EDGE,"E158"),sQuery(id+"F0.wireOp",EDGE,"E159"),sQuery(id+"F0.wireOp",EDGE,"E160"),sQuery(id+"F0.wireOp",EDGE,"E161"),sQuery(id+"F0.wireOp",EDGE,"E162"),sQuery(id+"F0.wireOp",EDGE,"E163"),sQuery(id+"F0.wireOp",EDGE,"E164"),sQuery(id+"F0.wireOp",EDGE,"E165"),sQuery(id+"F0.wireOp",EDGE,"E166"),sQuery(id+"F0.wireOp",EDGE,"E167"),sQuery(id+"F0.wireOp",EDGE,"E168"),sQuery(id+"F0.wireOp",EDGE,"E169"),sQuery(id+"F0.wireOp",EDGE,"E170"),sQuery(id+"F0.wireOp",EDGE,"E171"),sQuery(id+"F0.wireOp",EDGE,"E172"),sQuery(id+"F0.wireOp",EDGE,"E173"),sQuery(id+"F0.wireOp",EDGE,"E174"),sQuery(id+"F0.wireOp",EDGE,"E175"),sQuery(id+"F0.wireOp",EDGE,"E176"),sQuery(id+"F0.wireOp",EDGE,"E177"),sQuery(id+"F0.wireOp",EDGE,"E178"),sQuery(id+"F0.wireOp",EDGE,"E179"),sQuery(id+"F0.wireOp",EDGE,"E180"),sQuery(id+"F0.wireOp",EDGE,"E181"),sQuery(id+"F0.wireOp",EDGE,"E182"),sQuery(id+"F0.wireOp",EDGE,"E183"),sQuery(id+"F0.wireOp",EDGE,"E184"),sQuery(id+"F0.wireOp",EDGE,"E185"),sQuery(id+"F0.wireOp",EDGE,"E186"),sQuery(id+"F0.wireOp",EDGE,"E187"),sQuery(id+"F0.wireOp",EDGE,"E188"),sQuery(id+"F0.wireOp",EDGE,"E189"),sQuery(id+"F0.wireOp",EDGE,"E190"),sQuery(id+"F0.wireOp",EDGE,"E191"),sQuery(id+"F0.wireOp",EDGE,"E192"),sQuery(id+"F0.wireOp",EDGE,"E193"),sQuery(id+"F0.wireOp",EDGE,"E194"),sQuery(id+"F0.wireOp",EDGE,"E195"),sQuery(id+"F0.wireOp",EDGE,"E196"),sQuery(id+"F0.wireOp",EDGE,"E197"),sQuery(id+"F0.wireOp",EDGE,"E198"),sQuery(id+"F0.wireOp",EDGE,"E199"),sQuery(id+"F0.wireOp",EDGE,"E200"),sQuery(id+"F0.wireOp",EDGE,"E201"),sQuery(id+"F0.wireOp",EDGE,"E202"),sQuery(id+"F0.wireOp",EDGE,"E203"),sQuery(id+"F0.wireOp",EDGE,"E204"),sQuery(id+"F0.wireOp",EDGE,"E205"),sQuery(id+"F0.wireOp",EDGE,"E206"),sQuery(id+"F0.wireOp",EDGE,"E207"),sQuery(id+"F0.wireOp",EDGE,"E208"),sQuery(id+"F0.wireOp",EDGE,"E209"),sQuery(id+"F0.wireOp",EDGE,"E210"),sQuery(id+"F0.wireOp",EDGE,"E211"),sQuery(id+"F0.wireOp",EDGE,"E212"),sQuery(id+"F0.wireOp",EDGE,"E213"),sQuery(id+"F0.wireOp",EDGE,"E214"),sQuery(id+"F0.wireOp",EDGE,"E215"),sQuery(id+"F0.wireOp",EDGE,"E216"),sQuery(id+"F0.wireOp",EDGE,"E217"),sQuery(id+"F0.wireOp",EDGE,"E218"),sQuery(id+"F0.wireOp",EDGE,"E219"),sQuery(id+"F0.wireOp",EDGE,"E220"),sQuery(id+"F0.wireOp",EDGE,"E221"),sQuery(id+"F0.wireOp",EDGE,"E222"),sQuery(id+"F0.wireOp",EDGE,"E223"),sQuery(id+"F0.wireOp",EDGE,"E224"),sQuery(id+"F0.wireOp",EDGE,"E225"),sQuery(id+"F0.wireOp",EDGE,"E226"),sQuery(id+"F0.wireOp",EDGE,"E227"),sQuery(id+"F0.wireOp",EDGE,"E228"),sQuery(id+"F0.wireOp",EDGE,"E229"),sQuery(id+"F0.wireOp",EDGE,"E230"),sQuery(id+"F0.wireOp",EDGE,"E231"),sQuery(id+"F0.wireOp",EDGE,"E232"),sQuery(id+"F0.wireOp",EDGE,"E233"),sQuery(id+"F0.wireOp",EDGE,"E234"),sQuery(id+"F0.wireOp",EDGE,"E235"),sQuery(id+"F0.wireOp",EDGE,"E236"),sQuery(id+"F0.wireOp",EDGE,"E237"),sQuery(id+"F0.wireOp",EDGE,"E238"),sQuery(id+"F0.wireOp",EDGE,"E239"),sQuery(id+"F0.wireOp",EDGE,"E240"),sQuery(id+"F0.wireOp",EDGE,"E241"),sQuery(id+"F0.wireOp",EDGE,"E242"),sQuery(id+"F0.wireOp",EDGE,"E243"),sQuery(id+"F0.wireOp",EDGE,"E244"),sQuery(id+"F0.wireOp",EDGE,"E245"),sQuery(id+"F0.wireOp",EDGE,"E246"),sQuery(id+"F0.wireOp",EDGE,"E247"),sQuery(id+"F0.wireOp",EDGE,"E248"),sQuery(id+"F0.wireOp",EDGE,"E249"),sQuery(id+"F0.wireOp",EDGE,"E250"),sQuery(id+"F0.wireOp",EDGE,"E251"),sQuery(id+"F0.wireOp",EDGE,"E252"),sQuery(id+"F0.wireOp",EDGE,"E253"),sQuery(id+"F0.wireOp",EDGE,"E254"),sQuery(id+"F0.wireOp",EDGE,"E255"),sQuery(id+"F0.wireOp",EDGE,"E256"),sQuery(id+"F0.wireOp",EDGE,"E257"),sQuery(id+"F0.wireOp",EDGE,"E258"),sQuery(id+"F0.wireOp",EDGE,"E259"),sQuery(id+"F0.wireOp",EDGE,"E260"),sQuery(id+"F0.wireOp",EDGE,"E261"),sQuery(id+"F0.wireOp",EDGE,"E262"),sQuery(id+"F0.wireOp",EDGE,"E263"),sQuery(id+"F0.wireOp",EDGE,"E264"),sQuery(id+"F0.wireOp",EDGE,"E265"),sQuery(id+"F0.wireOp",EDGE,"E266"),sQuery(id+"F0.wireOp",EDGE,"E267"),sQuery(id+"F0.wireOp",EDGE,"E268"),sQuery(id+"F0.wireOp",EDGE,"E269"),sQuery(id+"F0.wireOp",EDGE,"E270"),sQuery(id+"F0.wireOp",EDGE,"E271"),sQuery(id+"F0.wireOp",EDGE,"E272"),sQuery(id+"F0.wireOp",EDGE,"E273"),sQuery(id+"F0.wireOp",EDGE,"E274"),sQuery(id+"F0.wireOp",EDGE,"E275"),sQuery(id+"F0.wireOp",EDGE,"E276"),sQuery(id+"F0.wireOp",EDGE,"E277"),sQuery(id+"F0.wireOp",EDGE,"E278"),sQuery(id+"F0.wireOp",EDGE,"E279"),sQuery(id+"F0.wireOp",EDGE,"E280"),sQuery(id+"F0.wireOp",EDGE,"E281"),sQuery(id+"F0.wireOp",EDGE,"E282"),sQuery(id+"F0.wireOp",EDGE,"E283"),sQuery(id+"F0.wireOp",EDGE,"E284"),sQuery(id+"F0.wireOp",EDGE,"E285"),sQuery(id+"F0.wireOp",EDGE,"E286"),sQuery(id+"F0.wireOp",EDGE,"E287"),sQuery(id+"F0.wireOp",EDGE,"E288"),sQuery(id+"F0.wireOp",EDGE,"E289"),sQuery(id+"F0.wireOp",EDGE,"E290"),sQuery(id+"F0.wireOp",EDGE,"E291"),sQuery(id+"F0.wireOp",EDGE,"E292"),sQuery(id+"F0.wireOp",EDGE,"E293"),sQuery(id+"F0.wireOp",EDGE,"E294"),sQuery(id+"F0.wireOp",EDGE,"E295"),sQuery(id+"F0.wireOp",EDGE,"E296"),sQuery(id+"F0.wireOp",EDGE,"E297"),sQuery(id+"F0.wireOp",EDGE,"E298"),sQuery(id+"F0.wireOp",EDGE,"E299"),sQuery(id+"F0.wireOp",EDGE,"E300"),sQuery(id+"F0.wireOp",EDGE,"E301"),sQuery(id+"F0.wireOp",EDGE,"E302"),sQuery(id+"F0.wireOp",EDGE,"E303"),sQuery(id+"F0.wireOp",EDGE,"E304"),sQuery(id+"F0.wireOp",EDGE,"E305"),sQuery(id+"F0.wireOp",EDGE,"E306"),sQuery(id+"F0.wireOp",EDGE,"E307"),sQuery(id+"F0.wireOp",EDGE,"E308"),sQuery(id+"F0.wireOp",EDGE,"E309"),sQuery(id+"F0.wireOp",EDGE,"E310"),sQuery(id+"F0.wireOp",EDGE,"E311"),sQuery(id+"F0.wireOp",EDGE,"E312"),sQuery(id+"F0.wireOp",EDGE,"E313"),sQuery(id+"F0.wireOp",EDGE,"E314"),sQuery(id+"F0.wireOp",EDGE,"E315"),sQuery(id+"F0.wireOp",EDGE,"E316"),sQuery(id+"F0.wireOp",EDGE,"E317"),sQuery(id+"F0.wireOp",EDGE,"E318"),sQuery(id+"F0.wireOp",EDGE,"E319"),sQuery(id+"F0.wireOp",EDGE,"E320"),sQuery(id+"F0.wireOp",EDGE,"E321"),sQuery(id+"F0.wireOp",EDGE,"E322"),sQuery(id+"F0.wireOp",EDGE,"E323"),sQuery(id+"F0.wireOp",EDGE,"E324"),sQuery(id+"F0.wireOp",EDGE,"E325"),sQuery(id+"F0.wireOp",EDGE,"E326"),sQuery(id+"F0.wireOp",EDGE,"E327"),sQuery(id+"F0.wireOp",EDGE,"E328"),sQuery(id+"F0.wireOp",EDGE,"E329"),sQuery(id+"F0.wireOp",EDGE,"E330"),sQuery(id+"F0.wireOp",EDGE,"E331"),sQuery(id+"F0.wireOp",EDGE,"E332"),sQuery(id+"F0.wireOp",EDGE,"E333"),sQuery(id+"F0.wireOp",EDGE,"E334"),sQuery(id+"F0.wireOp",EDGE,"E335"),sQuery(id+"F0.wireOp",EDGE,"E336"),sQuery(id+"F0.wireOp",EDGE,"E337"),sQuery(id+"F0.wireOp",EDGE,"E338"),sQuery(id+"F0.wireOp",EDGE,"E339"),sQuery(id+"F0.wireOp",EDGE,"E340"),sQuery(id+"F0.wireOp",EDGE,"E341"),sQuery(id+"F0.wireOp",EDGE,"E342"),sQuery(id+"F0.wireOp",EDGE,"E343"),sQuery(id+"F0.wireOp",EDGE,"E344"),sQuery(id+"F0.wireOp",EDGE,"E345"),sQuery(id+"F0.wireOp",EDGE,"E346"),sQuery(id+"F0.wireOp",EDGE,"E347"),sQuery(id+"F0.wireOp",EDGE,"E348"),sQuery(id+"F0.wireOp",EDGE,"E349"),sQuery(id+"F0.wireOp",EDGE,"E350"),sQuery(id+"F0.wireOp",EDGE,"E351"),sQuery(id+"F0.wireOp",EDGE,"E352"),sQuery(id+"F0.wireOp",EDGE,"E353"),sQuery(id+"F0.wireOp",EDGE,"E354"),sQuery(id+"F0.wireOp",EDGE,"E355"),sQuery(id+"F0.wireOp",EDGE,"E356"),sQuery(id+"F0.wireOp",EDGE,"E357"),sQuery(id+"F0.wireOp",EDGE,"E358"),sQuery(id+"F0.wireOp",EDGE,"E359"),sQuery(id+"F0.wireOp",EDGE,"E360"),sQuery(id+"F0.wireOp",EDGE,"E361"),sQuery(id+"F0.wireOp",EDGE,"E362"),sQuery(id+"F0.wireOp",EDGE,"E363"),sQuery(id+"F0.wireOp",EDGE,"E364"),sQuery(id+"F0.wireOp",EDGE,"E365"),sQuery(id+"F0.wireOp",EDGE,"E366"),sQuery(id+"F0.wireOp",EDGE,"E367"),sQuery(id+"F0.wireOp",EDGE,"E368"),sQuery(id+"F0.wireOp",EDGE,"E369"),sQuery(id+"F0.wireOp",EDGE,"E370"),sQuery(id+"F0.wireOp",EDGE,"E371"),sQuery(id+"F0.wireOp",EDGE,"E372"),sQuery(id+"F0.wireOp",EDGE,"E373"),sQuery(id+"F0.wireOp",EDGE,"E374"),sQuery(id+"F0.wireOp",EDGE,"E375"),sQuery(id+"F0.wireOp",EDGE,"E376"),sQuery(id+"F0.wireOp",EDGE,"E377"),sQuery(id+"F0.wireOp",EDGE,"E378"),sQuery(id+"F0.wireOp",EDGE,"E379"),sQuery(id+"F0.wireOp",EDGE,"E380"),sQuery(id+"F0.wireOp",EDGE,"E381"),sQuery(id+"F0.wireOp",EDGE,"E382"),sQuery(id+"F0.wireOp",EDGE,"E383"),sQuery(id+"F0.wireOp",EDGE,"E384"),sQuery(id+"F0.wireOp",EDGE,"E385"),sQuery(id+"F0.wireOp",EDGE,"E386"),sQuery(id+"F0.wireOp",EDGE,"E387"),sQuery(id+"F0.wireOp",EDGE,"E388"),sQuery(id+"F0.wireOp",EDGE,"E389"),sQuery(id+"F0.wireOp",EDGE,"E390"),sQuery(id+"F0.wireOp",EDGE,"E391"),sQuery(id+"F0.wireOp",EDGE,"E392"),sQuery(id+"F0.wireOp",EDGE,"E393"),sQuery(id+"F0.wireOp",EDGE,"E394"),sQuery(id+"F0.wireOp",EDGE,"E395"),sQuery(id+"F0.wireOp",EDGE,"E396"),sQuery(id+"F0.wireOp",EDGE,"E397"),sQuery(id+"F0.wireOp",EDGE,"E398"),sQuery(id+"F0.wireOp",EDGE,"E399"),sQuery(id+"F0.wireOp",EDGE,"E400"),sQuery(id+"F0.wireOp",EDGE,"E401"),sQuery(id+"F0.wireOp",EDGE,"E402"),sQuery(id+"F0.wireOp",EDGE,"E403"),sQuery(id+"F0.wireOp",EDGE,"E404"),sQuery(id+"F0.wireOp",EDGE,"E405"),sQuery(id+"F0.wireOp",EDGE,"E406"),sQuery(id+"F0.wireOp",EDGE,"E407"),sQuery(id+"F0.wireOp",EDGE,"E408"),sQuery(id+"F0.wireOp",EDGE,"E409"),sQuery(id+"F0.wireOp",EDGE,"E410"),sQuery(id+"F0.wireOp",EDGE,"E411"),sQuery(id+"F0.wireOp",EDGE,"E412"),sQuery(id+"F0.wireOp",EDGE,"E413"),sQuery(id+"F0.wireOp",EDGE,"E414"),sQuery(id+"F0.wireOp",EDGE,"E415"),sQuery(id+"F0.wireOp",EDGE,"E416"),sQuery(id+"F0.wireOp",EDGE,"E417"),sQuery(id+"F0.wireOp",EDGE,"E418"),sQuery(id+"F0.wireOp",EDGE,"E419"),sQuery(id+"F0.wireOp",EDGE,"E420"),sQuery(id+"F0.wireOp",EDGE,"E421"),sQuery(id+"F0.wireOp",EDGE,"E422"),sQuery(id+"F0.wireOp",EDGE,"E423"),sQuery(id+"F0.wireOp",EDGE,"E424"),sQuery(id+"F0.wireOp",EDGE,"E425"),sQuery(id+"F0.wireOp",EDGE,"E426"),sQuery(id+"F0.wireOp",EDGE,"E427"),sQuery(id+"F0.wireOp",EDGE,"E428"),sQuery(id+"F0.wireOp",EDGE,"E429"),sQuery(id+"F0.wireOp",EDGE,"E430"),sQuery(id+"F0.wireOp",EDGE,"E431"),sQuery(id+"F0.wireOp",EDGE,"E432"),sQuery(id+"F0.wireOp",EDGE,"E433"),sQuery(id+"F0.wireOp",EDGE,"E434"),sQuery(id+"F0.wireOp",EDGE,"E435"),sQuery(id+"F0.wireOp",EDGE,"E436"),sQuery(id+"F0.wireOp",EDGE,"E437"),sQuery(id+"F0.wireOp",EDGE,"E438"),sQuery(id+"F0.wireOp",EDGE,"E439"),sQuery(id+"F0.wireOp",EDGE,"E440"),sQuery(id+"F0.wireOp",EDGE,"E441"),sQuery(id+"F0.wireOp",EDGE,"E442"),sQuery(id+"F0.wireOp",EDGE,"E443"),sQuery(id+"F0.wireOp",EDGE,"E444"),sQuery(id+"F0.wireOp",EDGE,"E445"),sQuery(id+"F0.wireOp",EDGE,"E446"),sQuery(id+"F0.wireOp",EDGE,"E447"),sQuery(id+"F0.wireOp",EDGE,"E448"),sQuery(id+"F0.wireOp",EDGE,"E449"),sQuery(id+"F0.wireOp",EDGE,"E450"),sQuery(id+"F0.wireOp",EDGE,"E451"),sQuery(id+"F0.wireOp",EDGE,"E452"),sQuery(id+"F0.wireOp",EDGE,"E453"),sQuery(id+"F0.wireOp",EDGE,"E454"),sQuery(id+"F0.wireOp",EDGE,"E455"),sQuery(id+"F0.wireOp",EDGE,"E456"),sQuery(id+"F0.wireOp",EDGE,"E457"),sQuery(id+"F0.wireOp",EDGE,"E458"),sQuery(id+"F0.wireOp",EDGE,"E459"),sQuery(id+"F0.wireOp",EDGE,"E460"),sQuery(id+"F0.wireOp",EDGE,"E461"),sQuery(id+"F0.wireOp",EDGE,"E462"),sQuery(id+"F0.wireOp",EDGE,"E463"),sQuery(id+"F0.wireOp",EDGE,"E464"),sQuery(id+"F0.wireOp",EDGE,"E465"),sQuery(id+"F0.wireOp",EDGE,"E466"),sQuery(id+"F0.wireOp",EDGE,"E467"),sQuery(id+"F0.wireOp",EDGE,"E468"),sQuery(id+"F0.wireOp",EDGE,"E469"),sQuery(id+"F0.wireOp",EDGE,"E470"),sQuery(id+"F0.wireOp",EDGE,"E471"),sQuery(id+"F0.wireOp",EDGE,"E472"),sQuery(id+"F0.wireOp",EDGE,"E473"),sQuery(id+"F0.wireOp",EDGE,"E474"),sQuery(id+"F0.wireOp",EDGE,"E475"),sQuery(id+"F0.wireOp",EDGE,"E476"),sQuery(id+"F0.wireOp",EDGE,"E477"),sQuery(id+"F0.wireOp",EDGE,"E478"),sQuery(id+"F0.wireOp",EDGE,"E479"),sQuery(id+"F0.wireOp",EDGE,"E480"),sQuery(id+"F0.wireOp",EDGE,"E481"),sQuery(id+"F0.wireOp",EDGE,"E482"),sQuery(id+"F0.wireOp",EDGE,"E483"),sQuery(id+"F0.wireOp",EDGE,"E484"),sQuery(id+"F0.wireOp",EDGE,"E485"),sQuery(id+"F0.wireOp",EDGE,"E486"),sQuery(id+"F0.wireOp",EDGE,"E487"),sQuery(id+"F0.wireOp",EDGE,"E488"),sQuery(id+"F0.wireOp",EDGE,"E489"),sQuery(id+"F0.wireOp",EDGE,"E490"),sQuery(id+"F0.wireOp",EDGE,"E491"),sQuery(id+"F0.wireOp",EDGE,"E492"),sQuery(id+"F0.wireOp",EDGE,"E493"),sQuery(id+"F0.wireOp",EDGE,"E494"),sQuery(id+"F0.wireOp",EDGE,"E495"),sQuery(id+"F0.wireOp",EDGE,"E496"),sQuery(id+"F0.wireOp",EDGE,"E497"),sQuery(id+"F0.wireOp",EDGE,"E498"),sQuery(id+"F0.wireOp",EDGE,"E499"),sQuery(id+"F0.wireOp",EDGE,"E500"),sQuery(id+"F0.wireOp",EDGE,"E501"),sQuery(id+"F0.wireOp",EDGE,"E502"),sQuery(id+"F0.wireOp",EDGE,"E503"),sQuery(id+"F0.wireOp",EDGE,"E504"),sQuery(id+"F0.wireOp",EDGE,"E505"),sQuery(id+"F0.wireOp",EDGE,"E506"),sQuery(id+"F0.wireOp",EDGE,"E507"),sQuery(id+"F0.wireOp",EDGE,"E508"),sQuery(id+"F0.wireOp",EDGE,"E509"),sQuery(id+"F0.wireOp",EDGE,"E510"),sQuery(id+"F0.wireOp",EDGE,"E511"),sQuery(id+"F0.wireOp",EDGE,"E512"),sQuery(id+"F0.wireOp",EDGE,"E513"),sQuery(id+"F0.wireOp",EDGE,"E514"),sQuery(id+"F0.wireOp",EDGE,"E515"),sQuery(id+"F0.wireOp",EDGE,"E516"),sQuery(id+"F0.wireOp",EDGE,"E517"),sQuery(id+"F0.wireOp",EDGE,"E518"),sQuery(id+"F0.wireOp",EDGE,"E519"),sQuery(id+"F0.wireOp",EDGE,"E520"),sQuery(id+"F0.wireOp",EDGE,"E521"),sQuery(id+"F0.wireOp",EDGE,"E522"),sQuery(id+"F0.wireOp",EDGE,"E523"),sQuery(id+"F0.wireOp",EDGE,"E524"),sQuery(id+"F0.wireOp",EDGE,"E525"),sQuery(id+"F0.wireOp",EDGE,"E526"),sQuery(id+"F0.wireOp",EDGE,"E527"),sQuery(id+"F0.wireOp",EDGE,"E528"),sQuery(id+"F0.wireOp",EDGE,"E529"),sQuery(id+"F0.wireOp",EDGE,"E530"),sQuery(id+"F0.wireOp",EDGE,"E531"),sQuery(id+"F0.wireOp",EDGE,"E532"),sQuery(id+"F0.wireOp",EDGE,"E533"),sQuery(id+"F0.wireOp",EDGE,"E534"),sQuery(id+"F0.wireOp",EDGE,"E535"),sQuery(id+"F0.wireOp",EDGE,"E536"),sQuery(id+"F0.wireOp",EDGE,"E537"),sQuery(id+"F0.wireOp",EDGE,"E538"),sQuery(id+"F0.wireOp",EDGE,"E539"),sQuery(id+"F0.wireOp",EDGE,"E540"),sQuery(id+"F0.wireOp",EDGE,"E541"),sQuery(id+"F0.wireOp",EDGE,"E542"),sQuery(id+"F0.wireOp",EDGE,"E543"),sQuery(id+"F0.wireOp",EDGE,"E544"),sQuery(id+"F0.wireOp",EDGE,"E545"),sQuery(id+"F0.wireOp",EDGE,"E546"),sQuery(id+"F0.wireOp",EDGE,"E547"),sQuery(id+"F0.wireOp",EDGE,"E548"),sQuery(id+"F0.wireOp",EDGE,"E549"),sQuery(id+"F0.wireOp",EDGE,"E550"),sQuery(id+"F0.wireOp",EDGE,"E551"),sQuery(id+"F0.wireOp",EDGE,"E552"),sQuery(id+"F0.wireOp",EDGE,"E553"),sQuery(id+"F0.wireOp",EDGE,"E554"),sQuery(id+"F0.wireOp",EDGE,"E555")])],"isStart":true}),makeQuery(id+"F4.opExtrude","CAP_FACE",FACE,{"disambiguationData":[OSD([sQuery(id+"F2.wireOp",EDGE,"E863"),sQuery(id+"F2.wireOp",EDGE,"E864"),sQuery(id+"F2.wireOp",EDGE,"E865"),sQuery(id+"F2.wireOp",EDGE,"E866"),sQuery(id+"F2.wireOp",EDGE,"E867"),sQuery(id+"F2.wireOp",EDGE,"E868"),sQuery(id+"F2.wireOp",EDGE,"E869"),sQuery(id+"F2.wireOp",EDGE,"E870"),sQuery(id+"F2.wireOp",EDGE,"E871"),sQuery(id+"F2.wireOp",EDGE,"E872"),sQuery(id+"F2.wireOp",EDGE,"E873"),sQuery(id+"F2.wireOp",EDGE,"E874"),sQuery(id+"F2.wireOp",EDGE,"E875"),sQuery(id+"F2.wireOp",EDGE,"E876"),sQuery(id+"F2.wireOp",EDGE,"E877"),sQuery(id+"F2.wireOp",EDGE,"E878"),sQuery(id+"F2.wireOp",EDGE,"E879"),sQuery(id+"F2.wireOp",EDGE,"E880"),sQuery(id+"F2.wireOp",EDGE,"E881"),sQuery(id+"F2.wireOp",EDGE,"E882"),sQuery(id+"F2.wireOp",EDGE,"E883"),sQuery(id+"F2.wireOp",EDGE,"E884"),sQuery(id+"F2.wireOp",EDGE,"E885"),sQuery(id+"F2.wireOp",EDGE,"E886"),sQuery(id+"F2.wireOp",EDGE,"E887"),sQuery(id+"F2.wireOp",EDGE,"E888"),sQuery(id+"F2.wireOp",EDGE,"E889"),sQuery(id+"F2.wireOp",EDGE,"E890"),sQuery(id+"F2.wireOp",EDGE,"E891"),sQuery(id+"F2.wireOp",EDGE,"E892"),sQuery(id+"F2.wireOp",EDGE,"E893"),sQuery(id+"F2.wireOp",EDGE,"E894"),sQuery(id+"F2.wireOp",EDGE,"E895"),sQuery(id+"F2.wireOp",EDGE,"E896"),sQuery(id+"F2.wireOp",EDGE,"E897"),sQuery(id+"F2.wireOp",EDGE,"E898"),sQuery(id+"F2.wireOp",EDGE,"E899"),sQuery(id+"F2.wireOp",EDGE,"E900"),sQuery(id+"F2.wireOp",EDGE,"E901"),sQuery(id+"F2.wireOp",EDGE,"E902"),sQuery(id+"F2.wireOp",EDGE,"E903"),sQuery(id+"F2.wireOp",EDGE,"E904"),sQuery(id+"F2.wireOp",EDGE,"E905"),sQuery(id+"F2.wireOp",EDGE,"E906"),sQuery(id+"F2.wireOp",EDGE,"E907"),sQuery(id+"F2.wireOp",EDGE,"E908"),sQuery(id+"F2.wireOp",EDGE,"E909"),sQuery(id+"F2.wireOp",EDGE,"E910"),sQuery(id+"F2.wireOp",EDGE,"E911"),sQuery(id+"F2.wireOp",EDGE,"E912"),sQuery(id+"F2.wireOp",EDGE,"E913"),sQuery(id+"F2.wireOp",EDGE,"E914"),sQuery(id+"F2.wireOp",EDGE,"E915"),sQuery(id+"F2.wireOp",EDGE,"E916"),sQuery(id+"F2.wireOp",EDGE,"E917"),sQuery(id+"F2.wireOp",EDGE,"E918"),sQuery(id+"F2.wireOp",EDGE,"E919"),sQuery(id+"F2.wireOp",EDGE,"E920"),sQuery(id+"F2.wireOp",EDGE,"E921"),sQuery(id+"F2.wireOp",EDGE,"E922"),sQuery(id+"F2.wireOp",EDGE,"E923"),sQuery(id+"F2.wireOp",EDGE,"E924"),sQuery(id+"F2.wireOp",EDGE,"E925"),sQuery(id+"F2.wireOp",EDGE,"E926"),sQuery(id+"F2.wireOp",EDGE,"E927"),sQuery(id+"F2.wireOp",EDGE,"E928"),sQuery(id+"F2.wireOp",EDGE,"E929"),sQuery(id+"F2.wireOp",EDGE,"E930"),sQuery(id+"F2.wireOp",EDGE,"E931"),sQuery(id+"F2.wireOp",EDGE,"E932"),sQuery(id+"F2.wireOp",EDGE,"E933"),sQuery(id+"F2.wireOp",EDGE,"E934"),sQuery(id+"F2.wireOp",EDGE,"E935"),sQuery(id+"F2.wireOp",EDGE,"E936"),sQuery(id+"F2.wireOp",EDGE,"E937"),sQuery(id+"F2.wireOp",EDGE,"E938"),sQuery(id+"F2.wireOp",EDGE,"E939"),sQuery(id+"F2.wireOp",EDGE,"E940"),sQuery(id+"F2.wireOp",EDGE,"E941"),sQuery(id+"F2.wireOp",EDGE,"E942"),sQuery(id+"F2.wireOp",EDGE,"E943"),sQuery(id+"F2.wireOp",EDGE,"E944"),sQuery(id+"F2.wireOp",EDGE,"E945"),sQuery(id+"F2.wireOp",EDGE,"E946"),sQuery(id+"F2.wireOp",EDGE,"E947"),sQuery(id+"F2.wireOp",EDGE,"E948"),sQuery(id+"F2.wireOp",EDGE,"E949"),sQuery(id+"F2.wireOp",EDGE,"E950"),sQuery(id+"F2.wireOp",EDGE,"E951"),sQuery(id+"F2.wireOp",EDGE,"E952"),sQuery(id+"F2.wireOp",EDGE,"E953"),sQuery(id+"F2.wireOp",EDGE,"E954"),sQuery(id+"F2.wireOp",EDGE,"E955"),sQuery(id+"F2.wireOp",EDGE,"E956"),sQuery(id+"F2.wireOp",EDGE,"E957"),sQuery(id+"F2.wireOp",EDGE,"E958"),sQuery(id+"F2.wireOp",EDGE,"E959"),sQuery(id+"F2.wireOp",EDGE,"E960"),sQuery(id+"F2.wireOp",EDGE,"E961"),sQuery(id+"F2.wireOp",EDGE,"E962"),sQuery(id+"F2.wireOp",EDGE,"E963"),sQuery(id+"F2.wireOp",EDGE,"E964"),sQuery(id+"F2.wireOp",EDGE,"E965"),sQuery(id+"F2.wireOp",EDGE,"E966"),sQuery(id+"F2.wireOp",EDGE,"E967"),sQuery(id+"F2.wireOp",EDGE,"E968"),sQuery(id+"F2.wireOp",EDGE,"E969"),sQuery(id+"F2.wireOp",EDGE,"E970"),sQuery(id+"F2.wireOp",EDGE,"E971"),sQuery(id+"F2.wireOp",EDGE,"E972"),sQuery(id+"F2.wireOp",EDGE,"E973"),sQuery(id+"F2.wireOp",EDGE,"E974"),sQuery(id+"F2.wireOp",EDGE,"E975"),sQuery(id+"F2.wireOp",EDGE,"E976"),sQuery(id+"F2.wireOp",EDGE,"E977"),sQuery(id+"F2.wireOp",EDGE,"E978"),sQuery(id+"F2.wireOp",EDGE,"E979"),sQuery(id+"F2.wireOp",EDGE,"E980"),sQuery(id+"F2.wireOp",EDGE,"E981"),sQuery(id+"F2.wireOp",EDGE,"E982"),sQuery(id+"F2.wireOp",EDGE,"E983"),sQuery(id+"F2.wireOp",EDGE,"E984"),sQuery(id+"F2.wireOp",EDGE,"E985"),sQuery(id+"F2.wireOp",EDGE,"E986"),sQuery(id+"F2.wireOp",EDGE,"E987"),sQuery(id+"F2.wireOp",EDGE,"E988"),sQuery(id+"F2.wireOp",EDGE,"E989"),sQuery(id+"F2.wireOp",EDGE,"E990"),sQuery(id+"F2.wireOp",EDGE,"E991"),sQuery(id+"F2.wireOp",EDGE,"E992"),sQuery(id+"F2.wireOp",EDGE,"E993"),sQuery(id+"F2.wireOp",EDGE,"E994"),sQuery(id+"F2.wireOp",EDGE,"E995"),sQuery(id+"F2.wireOp",EDGE,"E996"),sQuery(id+"F2.wireOp",EDGE,"E997"),sQuery(id+"F2.wireOp",EDGE,"E998"),sQuery(id+"F2.wireOp",EDGE,"E999"),sQuery(id+"F2.wireOp",EDGE,"E1000"),sQuery(id+"F2.wireOp",EDGE,"E1001"),sQuery(id+"F2.wireOp",EDGE,"E1002"),sQuery(id+"F2.wireOp",EDGE,"E1003"),sQuery(id+"F2.wireOp",EDGE,"E1004"),sQuery(id+"F2.wireOp",EDGE,"E1005"),sQuery(id+"F2.wireOp",EDGE,"E1006"),sQuery(id+"F2.wireOp",EDGE,"E1007"),sQuery(id+"F2.wireOp",EDGE,"E1008"),sQuery(id+"F2.wireOp",EDGE,"E1009"),sQuery(id+"F2.wireOp",EDGE,"E1010"),sQuery(id+"F2.wireOp",EDGE,"E1011"),sQuery(id+"F2.wireOp",EDGE,"E1012"),sQuery(id+"F2.wireOp",EDGE,"E1013"),sQuery(id+"F2.wireOp",EDGE,"E1014"),sQuery(id+"F2.wireOp",EDGE,"E1015"),sQuery(id+"F2.wireOp",EDGE,"E1016"),sQuery(id+"F2.wireOp",EDGE,"E1017"),sQuery(id+"F2.wireOp",EDGE,"E1018"),sQuery(id+"F2.wireOp",EDGE,"E1019"),sQuery(id+"F2.wireOp",EDGE,"E1020"),sQuery(id+"F2.wireOp",EDGE,"E1021"),sQuery(id+"F2.wireOp",EDGE,"E1022"),sQuery(id+"F2.wireOp",EDGE,"E1023"),sQuery(id+"F2.wireOp",EDGE,"E1024"),sQuery(id+"F2.wireOp",EDGE,"E1025"),sQuery(id+"F2.wireOp",EDGE,"E1026"),sQuery(id+"F2.wireOp",EDGE,"E1027"),sQuery(id+"F2.wireOp",EDGE,"E1028"),sQuery(id+"F2.wireOp",EDGE,"E1029"),sQuery(id+"F2.wireOp",EDGE,"E1030"),sQuery(id+"F2.wireOp",EDGE,"E1031"),sQuery(id+"F2.wireOp",EDGE,"E1032"),sQuery(id+"F2.wireOp",EDGE,"E1033"),sQuery(id+"F2.wireOp",EDGE,"E1034"),sQuery(id+"F2.wireOp",EDGE,"E1035"),sQuery(id+"F2.wireOp",EDGE,"E1036"),sQuery(id+"F2.wireOp",EDGE,"E1037"),sQuery(id+"F2.wireOp",EDGE,"E1038"),sQuery(id+"F2.wireOp",EDGE,"E1039"),sQuery(id+"F2.wireOp",EDGE,"E1040"),sQuery(id+"F2.wireOp",EDGE,"E1041"),sQuery(id+"F2.wireOp",EDGE,"E1042"),sQuery(id+"F2.wireOp",EDGE,"E1043"),sQuery(id+"F2.wireOp",EDGE,"E1044"),sQuery(id+"F2.wireOp",EDGE,"E1045"),sQuery(id+"F2.wireOp",EDGE,"E1046"),sQuery(id+"F2.wireOp",EDGE,"E1047"),sQuery(id+"F2.wireOp",EDGE,"E1048"),sQuery(id+"F2.wireOp",EDGE,"E1049"),sQuery(id+"F2.wireOp",EDGE,"E1050"),sQuery(id+"F2.wireOp",EDGE,"E1051"),sQuery(id+"F2.wireOp",EDGE,"E1052"),sQuery(id+"F2.wireOp",EDGE,"E1053"),sQuery(id+"F2.wireOp",EDGE,"E1054"),sQuery(id+"F2.wireOp",EDGE,"E1055"),sQuery(id+"F2.wireOp",EDGE,"E1056"),sQuery(id+"F2.wireOp",EDGE,"E1057"),sQuery(id+"F2.wireOp",EDGE,"E1058"),sQuery(id+"F2.wireOp",EDGE,"E1059"),sQuery(id+"F2.wireOp",EDGE,"E1060"),sQuery(id+"F2.wireOp",EDGE,"E1061"),sQuery(id+"F2.wireOp",EDGE,"E1062"),sQuery(id+"F2.wireOp",EDGE,"E1063"),sQuery(id+"F2.wireOp",EDGE,"E1064"),sQuery(id+"F2.wireOp",EDGE,"E1065"),sQuery(id+"F2.wireOp",EDGE,"E1066"),sQuery(id+"F2.wireOp",EDGE,"E1067"),sQuery(id+"F2.wireOp",EDGE,"E1068"),sQuery(id+"F2.wireOp",EDGE,"E1069"),sQuery(id+"F2.wireOp",EDGE,"E1070"),sQuery(id+"F2.wireOp",EDGE,"E1071"),sQuery(id+"F2.wireOp",EDGE,"E1072"),sQuery(id+"F2.wireOp",EDGE,"E1073"),sQuery(id+"F2.wireOp",EDGE,"E1074"),sQuery(id+"F2.wireOp",EDGE,"E1075"),sQuery(id+"F2.wireOp",EDGE,"E1076"),sQuery(id+"F2.wireOp",EDGE,"E1077"),sQuery(id+"F2.wireOp",EDGE,"E1078"),sQuery(id+"F2.wireOp",EDGE,"E1079"),sQuery(id+"F2.wireOp",EDGE,"E1080"),sQuery(id+"F2.wireOp",EDGE,"E1081"),sQuery(id+"F2.wireOp",EDGE,"E1082"),sQuery(id+"F2.wireOp",EDGE,"E1083"),sQuery(id+"F2.wireOp",EDGE,"E1084"),sQuery(id+"F2.wireOp",EDGE,"E1085"),sQuery(id+"F2.wireOp",EDGE,"E1086"),sQuery(id+"F2.wireOp",EDGE,"E1087"),sQuery(id+"F2.wireOp",EDGE,"E1088"),sQuery(id+"F2.wireOp",EDGE,"E1089"),sQuery(id+"F2.wireOp",EDGE,"E1090"),sQuery(id+"F2.wireOp",EDGE,"E1091"),sQuery(id+"F2.wireOp",EDGE,"E1092"),sQuery(id+"F2.wireOp",EDGE,"E1093"),sQuery(id+"F2.wireOp",EDGE,"E1094"),sQuery(id+"F2.wireOp",EDGE,"E1095"),sQuery(id+"F2.wireOp",EDGE,"E1096"),sQuery(id+"F2.wireOp",EDGE,"E1097"),sQuery(id+"F2.wireOp",EDGE,"E1098"),sQuery(id+"F2.wireOp",EDGE,"E1099"),sQuery(id+"F2.wireOp",EDGE,"E1100"),sQuery(id+"F2.wireOp",EDGE,"E1101"),sQuery(id+"F2.wireOp",EDGE,"E1102"),sQuery(id+"F2.wireOp",EDGE,"E1103"),sQuery(id+"F2.wireOp",EDGE,"E1104"),sQuery(id+"F2.wireOp",EDGE,"E1105"),sQuery(id+"F2.wireOp",EDGE,"E1106"),sQuery(id+"F2.wireOp",EDGE,"E1107"),sQuery(id+"F2.wireOp",EDGE,"E1108"),sQuery(id+"F2.wireOp",EDGE,"E1109"),sQuery(id+"F2.wireOp",EDGE,"E1110"),sQuery(id+"F2.wireOp",EDGE,"E1111"),sQuery(id+"F2.wireOp",EDGE,"E1112"),sQuery(id+"F2.wireOp",EDGE,"E1113")])],"isStart":true})]});
            extrude(context, id + "F8", {"entities" : qUnion([Q0]), "operationType" : NewBodyOperationType.REMOVE, "oppositeDirection" : true, "depth" : 5 * mm});
        }
        {
            var Q0;
            Q0=makeQuery(id+"F1.opExtrude","CAP_FACE",FACE,{"disambiguationData":[OSD([sQuery(id+"F0.wireOp",EDGE,"E0"),sQuery(id+"F0.wireOp",EDGE,"E1"),sQuery(id+"F0.wireOp",EDGE,"E2"),sQuery(id+"F0.wireOp",EDGE,"E3"),sQuery(id+"F0.wireOp",EDGE,"E4"),sQuery(id+"F0.wireOp",EDGE,"E5"),sQuery(id+"F0.wireOp",EDGE,"E6"),sQuery(id+"F0.wireOp",EDGE,"E7"),sQuery(id+"F0.wireOp",EDGE,"E8"),sQuery(id+"F0.wireOp",EDGE,"E9"),sQuery(id+"F0.wireOp",EDGE,"E10"),sQuery(id+"F0.wireOp",EDGE,"E11"),sQuery(id+"F0.wireOp",EDGE,"E12"),sQuery(id+"F0.wireOp",EDGE,"E13"),sQuery(id+"F0.wireOp",EDGE,"E14"),sQuery(id+"F0.wireOp",EDGE,"E15"),sQuery(id+"F0.wireOp",EDGE,"E16"),sQuery(id+"F0.wireOp",EDGE,"E17"),sQuery(id+"F0.wireOp",EDGE,"E18"),sQuery(id+"F0.wireOp",EDGE,"E19"),sQuery(id+"F0.wireOp",EDGE,"E20"),sQuery(id+"F0.wireOp",EDGE,"E21"),sQuery(id+"F0.wireOp",EDGE,"E22"),sQuery(id+"F0.wireOp",EDGE,"E23"),sQuery(id+"F0.wireOp",EDGE,"E24"),sQuery(id+"F0.wireOp",EDGE,"E25"),sQuery(id+"F0.wireOp",EDGE,"E26"),sQuery(id+"F0.wireOp",EDGE,"E27"),sQuery(id+"F0.wireOp",EDGE,"E28"),sQuery(id+"F0.wireOp",EDGE,"E29"),sQuery(id+"F0.wireOp",EDGE,"E30"),sQuery(id+"F0.wireOp",EDGE,"E31"),sQuery(id+"F0.wireOp",EDGE,"E32"),sQuery(id+"F0.wireOp",EDGE,"E33"),sQuery(id+"F0.wireOp",EDGE,"E34"),sQuery(id+"F0.wireOp",EDGE,"E35"),sQuery(id+"F0.wireOp",EDGE,"E36"),sQuery(id+"F0.wireOp",EDGE,"E37"),sQuery(id+"F0.wireOp",EDGE,"E38"),sQuery(id+"F0.wireOp",EDGE,"E39"),sQuery(id+"F0.wireOp",EDGE,"E40"),sQuery(id+"F0.wireOp",EDGE,"E41"),sQuery(id+"F0.wireOp",EDGE,"E42"),sQuery(id+"F0.wireOp",EDGE,"E43"),sQuery(id+"F0.wireOp",EDGE,"E44"),sQuery(id+"F0.wireOp",EDGE,"E45"),sQuery(id+"F0.wireOp",EDGE,"E46"),sQuery(id+"F0.wireOp",EDGE,"E47"),sQuery(id+"F0.wireOp",EDGE,"E48"),sQuery(id+"F0.wireOp",EDGE,"E49"),sQuery(id+"F0.wireOp",EDGE,"E50"),sQuery(id+"F0.wireOp",EDGE,"E51"),sQuery(id+"F0.wireOp",EDGE,"E52"),sQuery(id+"F0.wireOp",EDGE,"E53"),sQuery(id+"F0.wireOp",EDGE,"E54"),sQuery(id+"F0.wireOp",EDGE,"E55"),sQuery(id+"F0.wireOp",EDGE,"E56"),sQuery(id+"F0.wireOp",EDGE,"E57"),sQuery(id+"F0.wireOp",EDGE,"E58"),sQuery(id+"F0.wireOp",EDGE,"E59"),sQuery(id+"F0.wireOp",EDGE,"E60"),sQuery(id+"F0.wireOp",EDGE,"E61"),sQuery(id+"F0.wireOp",EDGE,"E62"),sQuery(id+"F0.wireOp",EDGE,"E63"),sQuery(id+"F0.wireOp",EDGE,"E64"),sQuery(id+"F0.wireOp",EDGE,"E65"),sQuery(id+"F0.wireOp",EDGE,"E66"),sQuery(id+"F0.wireOp",EDGE,"E67"),sQuery(id+"F0.wireOp",EDGE,"E68"),sQuery(id+"F0.wireOp",EDGE,"E69"),sQuery(id+"F0.wireOp",EDGE,"E70"),sQuery(id+"F0.wireOp",EDGE,"E71"),sQuery(id+"F0.wireOp",EDGE,"E72"),sQuery(id+"F0.wireOp",EDGE,"E73"),sQuery(id+"F0.wireOp",EDGE,"E74"),sQuery(id+"F0.wireOp",EDGE,"E75"),sQuery(id+"F0.wireOp",EDGE,"E76"),sQuery(id+"F0.wireOp",EDGE,"E77"),sQuery(id+"F0.wireOp",EDGE,"E78"),sQuery(id+"F0.wireOp",EDGE,"E79"),sQuery(id+"F0.wireOp",EDGE,"E80"),sQuery(id+"F0.wireOp",EDGE,"E81"),sQuery(id+"F0.wireOp",EDGE,"E82"),sQuery(id+"F0.wireOp",EDGE,"E83"),sQuery(id+"F0.wireOp",EDGE,"E84"),sQuery(id+"F0.wireOp",EDGE,"E85"),sQuery(id+"F0.wireOp",EDGE,"E86"),sQuery(id+"F0.wireOp",EDGE,"E87"),sQuery(id+"F0.wireOp",EDGE,"E88"),sQuery(id+"F0.wireOp",EDGE,"E89"),sQuery(id+"F0.wireOp",EDGE,"E90"),sQuery(id+"F0.wireOp",EDGE,"E91"),sQuery(id+"F0.wireOp",EDGE,"E92"),sQuery(id+"F0.wireOp",EDGE,"E93"),sQuery(id+"F0.wireOp",EDGE,"E94"),sQuery(id+"F0.wireOp",EDGE,"E95"),sQuery(id+"F0.wireOp",EDGE,"E96"),sQuery(id+"F0.wireOp",EDGE,"E97"),sQuery(id+"F0.wireOp",EDGE,"E98"),sQuery(id+"F0.wireOp",EDGE,"E99"),sQuery(id+"F0.wireOp",EDGE,"E100"),sQuery(id+"F0.wireOp",EDGE,"E101"),sQuery(id+"F0.wireOp",EDGE,"E102"),sQuery(id+"F0.wireOp",EDGE,"E103"),sQuery(id+"F0.wireOp",EDGE,"E104"),sQuery(id+"F0.wireOp",EDGE,"E105"),sQuery(id+"F0.wireOp",EDGE,"E106"),sQuery(id+"F0.wireOp",EDGE,"E107"),sQuery(id+"F0.wireOp",EDGE,"E108"),sQuery(id+"F0.wireOp",EDGE,"E109"),sQuery(id+"F0.wireOp",EDGE,"E110"),sQuery(id+"F0.wireOp",EDGE,"E111"),sQuery(id+"F0.wireOp",EDGE,"E112"),sQuery(id+"F0.wireOp",EDGE,"E113"),sQuery(id+"F0.wireOp",EDGE,"E114"),sQuery(id+"F0.wireOp",EDGE,"E115"),sQuery(id+"F0.wireOp",EDGE,"E116"),sQuery(id+"F0.wireOp",EDGE,"E117"),sQuery(id+"F0.wireOp",EDGE,"E118"),sQuery(id+"F0.wireOp",EDGE,"E119"),sQuery(id+"F0.wireOp",EDGE,"E120"),sQuery(id+"F0.wireOp",EDGE,"E121"),sQuery(id+"F0.wireOp",EDGE,"E122"),sQuery(id+"F0.wireOp",EDGE,"E123"),sQuery(id+"F0.wireOp",EDGE,"E124"),sQuery(id+"F0.wireOp",EDGE,"E125"),sQuery(id+"F0.wireOp",EDGE,"E126"),sQuery(id+"F0.wireOp",EDGE,"E127"),sQuery(id+"F0.wireOp",EDGE,"E128"),sQuery(id+"F0.wireOp",EDGE,"E129"),sQuery(id+"F0.wireOp",EDGE,"E130"),sQuery(id+"F0.wireOp",EDGE,"E131"),sQuery(id+"F0.wireOp",EDGE,"E132"),sQuery(id+"F0.wireOp",EDGE,"E133"),sQuery(id+"F0.wireOp",EDGE,"E134"),sQuery(id+"F0.wireOp",EDGE,"E135"),sQuery(id+"F0.wireOp",EDGE,"E136"),sQuery(id+"F0.wireOp",EDGE,"E137"),sQuery(id+"F0.wireOp",EDGE,"E138"),sQuery(id+"F0.wireOp",EDGE,"E139"),sQuery(id+"F0.wireOp",EDGE,"E140"),sQuery(id+"F0.wireOp",EDGE,"E141"),sQuery(id+"F0.wireOp",EDGE,"E142"),sQuery(id+"F0.wireOp",EDGE,"E143"),sQuery(id+"F0.wireOp",EDGE,"E144"),sQuery(id+"F0.wireOp",EDGE,"E145"),sQuery(id+"F0.wireOp",EDGE,"E146"),sQuery(id+"F0.wireOp",EDGE,"E147"),sQuery(id+"F0.wireOp",EDGE,"E148"),sQuery(id+"F0.wireOp",EDGE,"E149"),sQuery(id+"F0.wireOp",EDGE,"E150"),sQuery(id+"F0.wireOp",EDGE,"E151"),sQuery(id+"F0.wireOp",EDGE,"E152"),sQuery(id+"F0.wireOp",EDGE,"E153"),sQuery(id+"F0.wireOp",EDGE,"E154"),sQuery(id+"F0.wireOp",EDGE,"E155"),sQuery(id+"F0.wireOp",EDGE,"E156"),sQuery(id+"F0.wireOp",EDGE,"E157"),sQuery(id+"F0.wireOp",EDGE,"E158"),sQuery(id+"F0.wireOp",EDGE,"E159"),sQuery(id+"F0.wireOp",EDGE,"E160"),sQuery(id+"F0.wireOp",EDGE,"E161"),sQuery(id+"F0.wireOp",EDGE,"E162"),sQuery(id+"F0.wireOp",EDGE,"E163"),sQuery(id+"F0.wireOp",EDGE,"E164"),sQuery(id+"F0.wireOp",EDGE,"E165"),sQuery(id+"F0.wireOp",EDGE,"E166"),sQuery(id+"F0.wireOp",EDGE,"E167"),sQuery(id+"F0.wireOp",EDGE,"E168"),sQuery(id+"F0.wireOp",EDGE,"E169"),sQuery(id+"F0.wireOp",EDGE,"E170"),sQuery(id+"F0.wireOp",EDGE,"E171"),sQuery(id+"F0.wireOp",EDGE,"E172"),sQuery(id+"F0.wireOp",EDGE,"E173"),sQuery(id+"F0.wireOp",EDGE,"E174"),sQuery(id+"F0.wireOp",EDGE,"E175"),sQuery(id+"F0.wireOp",EDGE,"E176"),sQuery(id+"F0.wireOp",EDGE,"E177"),sQuery(id+"F0.wireOp",EDGE,"E178"),sQuery(id+"F0.wireOp",EDGE,"E179"),sQuery(id+"F0.wireOp",EDGE,"E180"),sQuery(id+"F0.wireOp",EDGE,"E181"),sQuery(id+"F0.wireOp",EDGE,"E182"),sQuery(id+"F0.wireOp",EDGE,"E183"),sQuery(id+"F0.wireOp",EDGE,"E184"),sQuery(id+"F0.wireOp",EDGE,"E185"),sQuery(id+"F0.wireOp",EDGE,"E186"),sQuery(id+"F0.wireOp",EDGE,"E187"),sQuery(id+"F0.wireOp",EDGE,"E188"),sQuery(id+"F0.wireOp",EDGE,"E189"),sQuery(id+"F0.wireOp",EDGE,"E190"),sQuery(id+"F0.wireOp",EDGE,"E191"),sQuery(id+"F0.wireOp",EDGE,"E192"),sQuery(id+"F0.wireOp",EDGE,"E193"),sQuery(id+"F0.wireOp",EDGE,"E194"),sQuery(id+"F0.wireOp",EDGE,"E195"),sQuery(id+"F0.wireOp",EDGE,"E196"),sQuery(id+"F0.wireOp",EDGE,"E197"),sQuery(id+"F0.wireOp",EDGE,"E198"),sQuery(id+"F0.wireOp",EDGE,"E199"),sQuery(id+"F0.wireOp",EDGE,"E200"),sQuery(id+"F0.wireOp",EDGE,"E201"),sQuery(id+"F0.wireOp",EDGE,"E202"),sQuery(id+"F0.wireOp",EDGE,"E203"),sQuery(id+"F0.wireOp",EDGE,"E204"),sQuery(id+"F0.wireOp",EDGE,"E205"),sQuery(id+"F0.wireOp",EDGE,"E206"),sQuery(id+"F0.wireOp",EDGE,"E207"),sQuery(id+"F0.wireOp",EDGE,"E208"),sQuery(id+"F0.wireOp",EDGE,"E209"),sQuery(id+"F0.wireOp",EDGE,"E210"),sQuery(id+"F0.wireOp",EDGE,"E211"),sQuery(id+"F0.wireOp",EDGE,"E212"),sQuery(id+"F0.wireOp",EDGE,"E213"),sQuery(id+"F0.wireOp",EDGE,"E214"),sQuery(id+"F0.wireOp",EDGE,"E215"),sQuery(id+"F0.wireOp",EDGE,"E216"),sQuery(id+"F0.wireOp",EDGE,"E217"),sQuery(id+"F0.wireOp",EDGE,"E218"),sQuery(id+"F0.wireOp",EDGE,"E219"),sQuery(id+"F0.wireOp",EDGE,"E220"),sQuery(id+"F0.wireOp",EDGE,"E221"),sQuery(id+"F0.wireOp",EDGE,"E222"),sQuery(id+"F0.wireOp",EDGE,"E223"),sQuery(id+"F0.wireOp",EDGE,"E224"),sQuery(id+"F0.wireOp",EDGE,"E225"),sQuery(id+"F0.wireOp",EDGE,"E226"),sQuery(id+"F0.wireOp",EDGE,"E227"),sQuery(id+"F0.wireOp",EDGE,"E228"),sQuery(id+"F0.wireOp",EDGE,"E229"),sQuery(id+"F0.wireOp",EDGE,"E230"),sQuery(id+"F0.wireOp",EDGE,"E231"),sQuery(id+"F0.wireOp",EDGE,"E232"),sQuery(id+"F0.wireOp",EDGE,"E233"),sQuery(id+"F0.wireOp",EDGE,"E234"),sQuery(id+"F0.wireOp",EDGE,"E235"),sQuery(id+"F0.wireOp",EDGE,"E236"),sQuery(id+"F0.wireOp",EDGE,"E237"),sQuery(id+"F0.wireOp",EDGE,"E238"),sQuery(id+"F0.wireOp",EDGE,"E239"),sQuery(id+"F0.wireOp",EDGE,"E240"),sQuery(id+"F0.wireOp",EDGE,"E241"),sQuery(id+"F0.wireOp",EDGE,"E242"),sQuery(id+"F0.wireOp",EDGE,"E243"),sQuery(id+"F0.wireOp",EDGE,"E244"),sQuery(id+"F0.wireOp",EDGE,"E245"),sQuery(id+"F0.wireOp",EDGE,"E246"),sQuery(id+"F0.wireOp",EDGE,"E247"),sQuery(id+"F0.wireOp",EDGE,"E248"),sQuery(id+"F0.wireOp",EDGE,"E249"),sQuery(id+"F0.wireOp",EDGE,"E250"),sQuery(id+"F0.wireOp",EDGE,"E251"),sQuery(id+"F0.wireOp",EDGE,"E252"),sQuery(id+"F0.wireOp",EDGE,"E253"),sQuery(id+"F0.wireOp",EDGE,"E254"),sQuery(id+"F0.wireOp",EDGE,"E255"),sQuery(id+"F0.wireOp",EDGE,"E256"),sQuery(id+"F0.wireOp",EDGE,"E257"),sQuery(id+"F0.wireOp",EDGE,"E258"),sQuery(id+"F0.wireOp",EDGE,"E259"),sQuery(id+"F0.wireOp",EDGE,"E260"),sQuery(id+"F0.wireOp",EDGE,"E261"),sQuery(id+"F0.wireOp",EDGE,"E262"),sQuery(id+"F0.wireOp",EDGE,"E263"),sQuery(id+"F0.wireOp",EDGE,"E264"),sQuery(id+"F0.wireOp",EDGE,"E265"),sQuery(id+"F0.wireOp",EDGE,"E266"),sQuery(id+"F0.wireOp",EDGE,"E267"),sQuery(id+"F0.wireOp",EDGE,"E268"),sQuery(id+"F0.wireOp",EDGE,"E269"),sQuery(id+"F0.wireOp",EDGE,"E270"),sQuery(id+"F0.wireOp",EDGE,"E271"),sQuery(id+"F0.wireOp",EDGE,"E272"),sQuery(id+"F0.wireOp",EDGE,"E273"),sQuery(id+"F0.wireOp",EDGE,"E274"),sQuery(id+"F0.wireOp",EDGE,"E275"),sQuery(id+"F0.wireOp",EDGE,"E276"),sQuery(id+"F0.wireOp",EDGE,"E277"),sQuery(id+"F0.wireOp",EDGE,"E278"),sQuery(id+"F0.wireOp",EDGE,"E279"),sQuery(id+"F0.wireOp",EDGE,"E280"),sQuery(id+"F0.wireOp",EDGE,"E281"),sQuery(id+"F0.wireOp",EDGE,"E282"),sQuery(id+"F0.wireOp",EDGE,"E283"),sQuery(id+"F0.wireOp",EDGE,"E284"),sQuery(id+"F0.wireOp",EDGE,"E285"),sQuery(id+"F0.wireOp",EDGE,"E286"),sQuery(id+"F0.wireOp",EDGE,"E287"),sQuery(id+"F0.wireOp",EDGE,"E288"),sQuery(id+"F0.wireOp",EDGE,"E289"),sQuery(id+"F0.wireOp",EDGE,"E290"),sQuery(id+"F0.wireOp",EDGE,"E291"),sQuery(id+"F0.wireOp",EDGE,"E292"),sQuery(id+"F0.wireOp",EDGE,"E293"),sQuery(id+"F0.wireOp",EDGE,"E294"),sQuery(id+"F0.wireOp",EDGE,"E295"),sQuery(id+"F0.wireOp",EDGE,"E296"),sQuery(id+"F0.wireOp",EDGE,"E297"),sQuery(id+"F0.wireOp",EDGE,"E298"),sQuery(id+"F0.wireOp",EDGE,"E299"),sQuery(id+"F0.wireOp",EDGE,"E300"),sQuery(id+"F0.wireOp",EDGE,"E301"),sQuery(id+"F0.wireOp",EDGE,"E302"),sQuery(id+"F0.wireOp",EDGE,"E303"),sQuery(id+"F0.wireOp",EDGE,"E304"),sQuery(id+"F0.wireOp",EDGE,"E305"),sQuery(id+"F0.wireOp",EDGE,"E306"),sQuery(id+"F0.wireOp",EDGE,"E307"),sQuery(id+"F0.wireOp",EDGE,"E308"),sQuery(id+"F0.wireOp",EDGE,"E309"),sQuery(id+"F0.wireOp",EDGE,"E310"),sQuery(id+"F0.wireOp",EDGE,"E311"),sQuery(id+"F0.wireOp",EDGE,"E312"),sQuery(id+"F0.wireOp",EDGE,"E313"),sQuery(id+"F0.wireOp",EDGE,"E314"),sQuery(id+"F0.wireOp",EDGE,"E315"),sQuery(id+"F0.wireOp",EDGE,"E316"),sQuery(id+"F0.wireOp",EDGE,"E317"),sQuery(id+"F0.wireOp",EDGE,"E318"),sQuery(id+"F0.wireOp",EDGE,"E319"),sQuery(id+"F0.wireOp",EDGE,"E320"),sQuery(id+"F0.wireOp",EDGE,"E321"),sQuery(id+"F0.wireOp",EDGE,"E322"),sQuery(id+"F0.wireOp",EDGE,"E323"),sQuery(id+"F0.wireOp",EDGE,"E324"),sQuery(id+"F0.wireOp",EDGE,"E325"),sQuery(id+"F0.wireOp",EDGE,"E326"),sQuery(id+"F0.wireOp",EDGE,"E327"),sQuery(id+"F0.wireOp",EDGE,"E328"),sQuery(id+"F0.wireOp",EDGE,"E329"),sQuery(id+"F0.wireOp",EDGE,"E330"),sQuery(id+"F0.wireOp",EDGE,"E331"),sQuery(id+"F0.wireOp",EDGE,"E332"),sQuery(id+"F0.wireOp",EDGE,"E333"),sQuery(id+"F0.wireOp",EDGE,"E334"),sQuery(id+"F0.wireOp",EDGE,"E335"),sQuery(id+"F0.wireOp",EDGE,"E336"),sQuery(id+"F0.wireOp",EDGE,"E337"),sQuery(id+"F0.wireOp",EDGE,"E338"),sQuery(id+"F0.wireOp",EDGE,"E339"),sQuery(id+"F0.wireOp",EDGE,"E340"),sQuery(id+"F0.wireOp",EDGE,"E341"),sQuery(id+"F0.wireOp",EDGE,"E342"),sQuery(id+"F0.wireOp",EDGE,"E343"),sQuery(id+"F0.wireOp",EDGE,"E344"),sQuery(id+"F0.wireOp",EDGE,"E345"),sQuery(id+"F0.wireOp",EDGE,"E346"),sQuery(id+"F0.wireOp",EDGE,"E347"),sQuery(id+"F0.wireOp",EDGE,"E348"),sQuery(id+"F0.wireOp",EDGE,"E349"),sQuery(id+"F0.wireOp",EDGE,"E350"),sQuery(id+"F0.wireOp",EDGE,"E351"),sQuery(id+"F0.wireOp",EDGE,"E352"),sQuery(id+"F0.wireOp",EDGE,"E353"),sQuery(id+"F0.wireOp",EDGE,"E354"),sQuery(id+"F0.wireOp",EDGE,"E355"),sQuery(id+"F0.wireOp",EDGE,"E356"),sQuery(id+"F0.wireOp",EDGE,"E357"),sQuery(id+"F0.wireOp",EDGE,"E358"),sQuery(id+"F0.wireOp",EDGE,"E359"),sQuery(id+"F0.wireOp",EDGE,"E360"),sQuery(id+"F0.wireOp",EDGE,"E361"),sQuery(id+"F0.wireOp",EDGE,"E362"),sQuery(id+"F0.wireOp",EDGE,"E363"),sQuery(id+"F0.wireOp",EDGE,"E364"),sQuery(id+"F0.wireOp",EDGE,"E365"),sQuery(id+"F0.wireOp",EDGE,"E366"),sQuery(id+"F0.wireOp",EDGE,"E367"),sQuery(id+"F0.wireOp",EDGE,"E368"),sQuery(id+"F0.wireOp",EDGE,"E369"),sQuery(id+"F0.wireOp",EDGE,"E370"),sQuery(id+"F0.wireOp",EDGE,"E371"),sQuery(id+"F0.wireOp",EDGE,"E372"),sQuery(id+"F0.wireOp",EDGE,"E373"),sQuery(id+"F0.wireOp",EDGE,"E374"),sQuery(id+"F0.wireOp",EDGE,"E375"),sQuery(id+"F0.wireOp",EDGE,"E376"),sQuery(id+"F0.wireOp",EDGE,"E377"),sQuery(id+"F0.wireOp",EDGE,"E378"),sQuery(id+"F0.wireOp",EDGE,"E379"),sQuery(id+"F0.wireOp",EDGE,"E380"),sQuery(id+"F0.wireOp",EDGE,"E381"),sQuery(id+"F0.wireOp",EDGE,"E382"),sQuery(id+"F0.wireOp",EDGE,"E383"),sQuery(id+"F0.wireOp",EDGE,"E384"),sQuery(id+"F0.wireOp",EDGE,"E385"),sQuery(id+"F0.wireOp",EDGE,"E386"),sQuery(id+"F0.wireOp",EDGE,"E387"),sQuery(id+"F0.wireOp",EDGE,"E388"),sQuery(id+"F0.wireOp",EDGE,"E389"),sQuery(id+"F0.wireOp",EDGE,"E390"),sQuery(id+"F0.wireOp",EDGE,"E391"),sQuery(id+"F0.wireOp",EDGE,"E392"),sQuery(id+"F0.wireOp",EDGE,"E393"),sQuery(id+"F0.wireOp",EDGE,"E394"),sQuery(id+"F0.wireOp",EDGE,"E395"),sQuery(id+"F0.wireOp",EDGE,"E396"),sQuery(id+"F0.wireOp",EDGE,"E397"),sQuery(id+"F0.wireOp",EDGE,"E398"),sQuery(id+"F0.wireOp",EDGE,"E399"),sQuery(id+"F0.wireOp",EDGE,"E400"),sQuery(id+"F0.wireOp",EDGE,"E401"),sQuery(id+"F0.wireOp",EDGE,"E402"),sQuery(id+"F0.wireOp",EDGE,"E403"),sQuery(id+"F0.wireOp",EDGE,"E404"),sQuery(id+"F0.wireOp",EDGE,"E405"),sQuery(id+"F0.wireOp",EDGE,"E406"),sQuery(id+"F0.wireOp",EDGE,"E407"),sQuery(id+"F0.wireOp",EDGE,"E408"),sQuery(id+"F0.wireOp",EDGE,"E409"),sQuery(id+"F0.wireOp",EDGE,"E410"),sQuery(id+"F0.wireOp",EDGE,"E411"),sQuery(id+"F0.wireOp",EDGE,"E412"),sQuery(id+"F0.wireOp",EDGE,"E413"),sQuery(id+"F0.wireOp",EDGE,"E414"),sQuery(id+"F0.wireOp",EDGE,"E415"),sQuery(id+"F0.wireOp",EDGE,"E416"),sQuery(id+"F0.wireOp",EDGE,"E417"),sQuery(id+"F0.wireOp",EDGE,"E418"),sQuery(id+"F0.wireOp",EDGE,"E419"),sQuery(id+"F0.wireOp",EDGE,"E420"),sQuery(id+"F0.wireOp",EDGE,"E421"),sQuery(id+"F0.wireOp",EDGE,"E422"),sQuery(id+"F0.wireOp",EDGE,"E423"),sQuery(id+"F0.wireOp",EDGE,"E424"),sQuery(id+"F0.wireOp",EDGE,"E425"),sQuery(id+"F0.wireOp",EDGE,"E426"),sQuery(id+"F0.wireOp",EDGE,"E427"),sQuery(id+"F0.wireOp",EDGE,"E428"),sQuery(id+"F0.wireOp",EDGE,"E429"),sQuery(id+"F0.wireOp",EDGE,"E430"),sQuery(id+"F0.wireOp",EDGE,"E431"),sQuery(id+"F0.wireOp",EDGE,"E432"),sQuery(id+"F0.wireOp",EDGE,"E433"),sQuery(id+"F0.wireOp",EDGE,"E434"),sQuery(id+"F0.wireOp",EDGE,"E435"),sQuery(id+"F0.wireOp",EDGE,"E436"),sQuery(id+"F0.wireOp",EDGE,"E437"),sQuery(id+"F0.wireOp",EDGE,"E438"),sQuery(id+"F0.wireOp",EDGE,"E439"),sQuery(id+"F0.wireOp",EDGE,"E440"),sQuery(id+"F0.wireOp",EDGE,"E441"),sQuery(id+"F0.wireOp",EDGE,"E442"),sQuery(id+"F0.wireOp",EDGE,"E443"),sQuery(id+"F0.wireOp",EDGE,"E444"),sQuery(id+"F0.wireOp",EDGE,"E445"),sQuery(id+"F0.wireOp",EDGE,"E446"),sQuery(id+"F0.wireOp",EDGE,"E447"),sQuery(id+"F0.wireOp",EDGE,"E448"),sQuery(id+"F0.wireOp",EDGE,"E449"),sQuery(id+"F0.wireOp",EDGE,"E450"),sQuery(id+"F0.wireOp",EDGE,"E451"),sQuery(id+"F0.wireOp",EDGE,"E452"),sQuery(id+"F0.wireOp",EDGE,"E453"),sQuery(id+"F0.wireOp",EDGE,"E454"),sQuery(id+"F0.wireOp",EDGE,"E455"),sQuery(id+"F0.wireOp",EDGE,"E456"),sQuery(id+"F0.wireOp",EDGE,"E457"),sQuery(id+"F0.wireOp",EDGE,"E458"),sQuery(id+"F0.wireOp",EDGE,"E459"),sQuery(id+"F0.wireOp",EDGE,"E460"),sQuery(id+"F0.wireOp",EDGE,"E461"),sQuery(id+"F0.wireOp",EDGE,"E462"),sQuery(id+"F0.wireOp",EDGE,"E463"),sQuery(id+"F0.wireOp",EDGE,"E464"),sQuery(id+"F0.wireOp",EDGE,"E465"),sQuery(id+"F0.wireOp",EDGE,"E466"),sQuery(id+"F0.wireOp",EDGE,"E467"),sQuery(id+"F0.wireOp",EDGE,"E468"),sQuery(id+"F0.wireOp",EDGE,"E469"),sQuery(id+"F0.wireOp",EDGE,"E470"),sQuery(id+"F0.wireOp",EDGE,"E471"),sQuery(id+"F0.wireOp",EDGE,"E472"),sQuery(id+"F0.wireOp",EDGE,"E473"),sQuery(id+"F0.wireOp",EDGE,"E474"),sQuery(id+"F0.wireOp",EDGE,"E475"),sQuery(id+"F0.wireOp",EDGE,"E476"),sQuery(id+"F0.wireOp",EDGE,"E477"),sQuery(id+"F0.wireOp",EDGE,"E478"),sQuery(id+"F0.wireOp",EDGE,"E479"),sQuery(id+"F0.wireOp",EDGE,"E480"),sQuery(id+"F0.wireOp",EDGE,"E481"),sQuery(id+"F0.wireOp",EDGE,"E482"),sQuery(id+"F0.wireOp",EDGE,"E483"),sQuery(id+"F0.wireOp",EDGE,"E484"),sQuery(id+"F0.wireOp",EDGE,"E485"),sQuery(id+"F0.wireOp",EDGE,"E486"),sQuery(id+"F0.wireOp",EDGE,"E487"),sQuery(id+"F0.wireOp",EDGE,"E488"),sQuery(id+"F0.wireOp",EDGE,"E489"),sQuery(id+"F0.wireOp",EDGE,"E490"),sQuery(id+"F0.wireOp",EDGE,"E491"),sQuery(id+"F0.wireOp",EDGE,"E492"),sQuery(id+"F0.wireOp",EDGE,"E493"),sQuery(id+"F0.wireOp",EDGE,"E494"),sQuery(id+"F0.wireOp",EDGE,"E495"),sQuery(id+"F0.wireOp",EDGE,"E496"),sQuery(id+"F0.wireOp",EDGE,"E497"),sQuery(id+"F0.wireOp",EDGE,"E498"),sQuery(id+"F0.wireOp",EDGE,"E499"),sQuery(id+"F0.wireOp",EDGE,"E500"),sQuery(id+"F0.wireOp",EDGE,"E501"),sQuery(id+"F0.wireOp",EDGE,"E502"),sQuery(id+"F0.wireOp",EDGE,"E503"),sQuery(id+"F0.wireOp",EDGE,"E504"),sQuery(id+"F0.wireOp",EDGE,"E505"),sQuery(id+"F0.wireOp",EDGE,"E506"),sQuery(id+"F0.wireOp",EDGE,"E507"),sQuery(id+"F0.wireOp",EDGE,"E508"),sQuery(id+"F0.wireOp",EDGE,"E509"),sQuery(id+"F0.wireOp",EDGE,"E510"),sQuery(id+"F0.wireOp",EDGE,"E511"),sQuery(id+"F0.wireOp",EDGE,"E512"),sQuery(id+"F0.wireOp",EDGE,"E513"),sQuery(id+"F0.wireOp",EDGE,"E514"),sQuery(id+"F0.wireOp",EDGE,"E515"),sQuery(id+"F0.wireOp",EDGE,"E516"),sQuery(id+"F0.wireOp",EDGE,"E517"),sQuery(id+"F0.wireOp",EDGE,"E518"),sQuery(id+"F0.wireOp",EDGE,"E519"),sQuery(id+"F0.wireOp",EDGE,"E520"),sQuery(id+"F0.wireOp",EDGE,"E521"),sQuery(id+"F0.wireOp",EDGE,"E522"),sQuery(id+"F0.wireOp",EDGE,"E523"),sQuery(id+"F0.wireOp",EDGE,"E524"),sQuery(id+"F0.wireOp",EDGE,"E525"),sQuery(id+"F0.wireOp",EDGE,"E526"),sQuery(id+"F0.wireOp",EDGE,"E527"),sQuery(id+"F0.wireOp",EDGE,"E528"),sQuery(id+"F0.wireOp",EDGE,"E529"),sQuery(id+"F0.wireOp",EDGE,"E530"),sQuery(id+"F0.wireOp",EDGE,"E531"),sQuery(id+"F0.wireOp",EDGE,"E532"),sQuery(id+"F0.wireOp",EDGE,"E533"),sQuery(id+"F0.wireOp",EDGE,"E534"),sQuery(id+"F0.wireOp",EDGE,"E535"),sQuery(id+"F0.wireOp",EDGE,"E536"),sQuery(id+"F0.wireOp",EDGE,"E537"),sQuery(id+"F0.wireOp",EDGE,"E538"),sQuery(id+"F0.wireOp",EDGE,"E539"),sQuery(id+"F0.wireOp",EDGE,"E540"),sQuery(id+"F0.wireOp",EDGE,"E541"),sQuery(id+"F0.wireOp",EDGE,"E542"),sQuery(id+"F0.wireOp",EDGE,"E543"),sQuery(id+"F0.wireOp",EDGE,"E544"),sQuery(id+"F0.wireOp",EDGE,"E545"),sQuery(id+"F0.wireOp",EDGE,"E546"),sQuery(id+"F0.wireOp",EDGE,"E547"),sQuery(id+"F0.wireOp",EDGE,"E548"),sQuery(id+"F0.wireOp",EDGE,"E549"),sQuery(id+"F0.wireOp",EDGE,"E550"),sQuery(id+"F0.wireOp",EDGE,"E551"),sQuery(id+"F0.wireOp",EDGE,"E552"),sQuery(id+"F0.wireOp",EDGE,"E553"),sQuery(id+"F0.wireOp",EDGE,"E554"),sQuery(id+"F0.wireOp",EDGE,"E555")])],"isStart":false});
            var sketch = newSketch(context, id + "F9", { "sketchPlane" : qUnion([Q0])});
            skCircle(sketch, "E1115", {"center": v(0, 14.5) * mm, "radius": 1.5 * mm});
            skCircle(sketch, "E1116", {"center": v(0, -14.5) * mm, "radius": 1.5 * mm});
            skCircle(sketch, "E1117", {"center": v(-14.5, 0) * mm, "radius": 1.5 * mm});
            skCircle(sketch, "E1118", {"center": v(0, 0) * mm, "radius": 7.5 * mm});
            skPoint(sketch, "E1119.center.orphan", {"position": v(19.52, 0) * mm});
            skSolve(sketch);
        }
        {
            var Q0;
            Q0 = qSketchRegion(id + "F9", true);
            extrude(context, id + "F10", {"entities" : qUnion([Q0]), "operationType" : NewBodyOperationType.REMOVE, "oppositeDirection" : true, "depth" : 2 * mm});
        }
        {
            var Q0;
            Q0=makeQuery(id+"F10.boolean.opBoolean","COPY",FACE,{"derivedFrom":makeQuery(id+"F10.opExtrude","CAP_FACE",FACE,{"disambiguationData":[OSD([sQuery(id+"F9.wireOp",EDGE,"E1115")])],"isStart":false})});
            var Q1;
            Q1=makeQuery(id+"F10.boolean.opBoolean","COPY",FACE,{"derivedFrom":makeQuery(id+"F10.opExtrude","CAP_FACE",FACE,{"disambiguationData":[OSD([sQuery(id+"F9.wireOp",EDGE,"E1117")])],"isStart":false})});
            extrude(context, id + "F11", {"entities" : qUnion([Q0, Q1]), "operationType" : NewBodyOperationType.REMOVE, "oppositeDirection" : true, "depth" : 25 * mm});
        }
        {
            var Q0;
            Q0=makeQuery(id+"F10.boolean.opBoolean","COPY",FACE,{"derivedFrom":makeQuery(id+"F10.opExtrude","CAP_FACE",FACE,{"disambiguationData":[OSD([sQuery(id+"F9.wireOp",EDGE,"E1116")])],"isStart":false})});
            extrude(context, id + "F12", {"entities" : qUnion([Q0]), "operationType" : NewBodyOperationType.REMOVE, "oppositeDirection" : true, "depth" : 25 * mm});
        }
        {
            var Q0;
            Q0=makeQuery(id+"F8.boolean.opBoolean","COPY",FACE,{"derivedFrom":makeQuery(id+"F8.opExtrude","CAP_FACE",FACE,{"disambiguationData":[OSD([sQuery(id+"F0.wireOp",EDGE,"E0"),sQuery(id+"F0.wireOp",EDGE,"E1"),sQuery(id+"F0.wireOp",EDGE,"E2"),sQuery(id+"F0.wireOp",EDGE,"E3"),sQuery(id+"F0.wireOp",EDGE,"E4"),sQuery(id+"F0.wireOp",EDGE,"E5"),sQuery(id+"F0.wireOp",EDGE,"E6"),sQuery(id+"F0.wireOp",EDGE,"E7"),sQuery(id+"F0.wireOp",EDGE,"E8"),sQuery(id+"F0.wireOp",EDGE,"E9"),sQuery(id+"F0.wireOp",EDGE,"E10"),sQuery(id+"F0.wireOp",EDGE,"E11"),sQuery(id+"F0.wireOp",EDGE,"E12"),sQuery(id+"F0.wireOp",EDGE,"E13"),sQuery(id+"F0.wireOp",EDGE,"E14"),sQuery(id+"F0.wireOp",EDGE,"E15"),sQuery(id+"F0.wireOp",EDGE,"E16"),sQuery(id+"F0.wireOp",EDGE,"E17"),sQuery(id+"F0.wireOp",EDGE,"E18"),sQuery(id+"F0.wireOp",EDGE,"E19"),sQuery(id+"F0.wireOp",EDGE,"E20"),sQuery(id+"F0.wireOp",EDGE,"E21"),sQuery(id+"F0.wireOp",EDGE,"E22"),sQuery(id+"F0.wireOp",EDGE,"E23"),sQuery(id+"F0.wireOp",EDGE,"E24"),sQuery(id+"F0.wireOp",EDGE,"E25"),sQuery(id+"F0.wireOp",EDGE,"E26"),sQuery(id+"F0.wireOp",EDGE,"E27"),sQuery(id+"F0.wireOp",EDGE,"E28"),sQuery(id+"F0.wireOp",EDGE,"E29"),sQuery(id+"F0.wireOp",EDGE,"E30"),sQuery(id+"F0.wireOp",EDGE,"E31"),sQuery(id+"F0.wireOp",EDGE,"E32"),sQuery(id+"F0.wireOp",EDGE,"E33"),sQuery(id+"F0.wireOp",EDGE,"E34"),sQuery(id+"F0.wireOp",EDGE,"E35"),sQuery(id+"F0.wireOp",EDGE,"E36"),sQuery(id+"F0.wireOp",EDGE,"E37"),sQuery(id+"F0.wireOp",EDGE,"E38"),sQuery(id+"F0.wireOp",EDGE,"E39"),sQuery(id+"F0.wireOp",EDGE,"E40"),sQuery(id+"F0.wireOp",EDGE,"E41"),sQuery(id+"F0.wireOp",EDGE,"E42"),sQuery(id+"F0.wireOp",EDGE,"E43"),sQuery(id+"F0.wireOp",EDGE,"E44"),sQuery(id+"F0.wireOp",EDGE,"E45"),sQuery(id+"F0.wireOp",EDGE,"E46"),sQuery(id+"F0.wireOp",EDGE,"E47"),sQuery(id+"F0.wireOp",EDGE,"E48"),sQuery(id+"F0.wireOp",EDGE,"E49"),sQuery(id+"F0.wireOp",EDGE,"E50"),sQuery(id+"F0.wireOp",EDGE,"E51"),sQuery(id+"F0.wireOp",EDGE,"E52"),sQuery(id+"F0.wireOp",EDGE,"E53"),sQuery(id+"F0.wireOp",EDGE,"E54"),sQuery(id+"F0.wireOp",EDGE,"E55"),sQuery(id+"F0.wireOp",EDGE,"E56"),sQuery(id+"F0.wireOp",EDGE,"E57"),sQuery(id+"F0.wireOp",EDGE,"E58"),sQuery(id+"F0.wireOp",EDGE,"E59"),sQuery(id+"F0.wireOp",EDGE,"E60"),sQuery(id+"F0.wireOp",EDGE,"E61"),sQuery(id+"F0.wireOp",EDGE,"E62"),sQuery(id+"F0.wireOp",EDGE,"E63"),sQuery(id+"F0.wireOp",EDGE,"E64"),sQuery(id+"F0.wireOp",EDGE,"E65"),sQuery(id+"F0.wireOp",EDGE,"E66"),sQuery(id+"F0.wireOp",EDGE,"E67"),sQuery(id+"F0.wireOp",EDGE,"E68"),sQuery(id+"F0.wireOp",EDGE,"E69"),sQuery(id+"F0.wireOp",EDGE,"E70"),sQuery(id+"F0.wireOp",EDGE,"E71"),sQuery(id+"F0.wireOp",EDGE,"E72"),sQuery(id+"F0.wireOp",EDGE,"E73"),sQuery(id+"F0.wireOp",EDGE,"E74"),sQuery(id+"F0.wireOp",EDGE,"E75"),sQuery(id+"F0.wireOp",EDGE,"E76"),sQuery(id+"F0.wireOp",EDGE,"E77"),sQuery(id+"F0.wireOp",EDGE,"E78"),sQuery(id+"F0.wireOp",EDGE,"E79"),sQuery(id+"F0.wireOp",EDGE,"E80"),sQuery(id+"F0.wireOp",EDGE,"E81"),sQuery(id+"F0.wireOp",EDGE,"E82"),sQuery(id+"F0.wireOp",EDGE,"E83"),sQuery(id+"F0.wireOp",EDGE,"E84"),sQuery(id+"F0.wireOp",EDGE,"E85"),sQuery(id+"F0.wireOp",EDGE,"E86"),sQuery(id+"F0.wireOp",EDGE,"E87"),sQuery(id+"F0.wireOp",EDGE,"E88"),sQuery(id+"F0.wireOp",EDGE,"E89"),sQuery(id+"F0.wireOp",EDGE,"E90"),sQuery(id+"F0.wireOp",EDGE,"E91"),sQuery(id+"F0.wireOp",EDGE,"E92"),sQuery(id+"F0.wireOp",EDGE,"E93"),sQuery(id+"F0.wireOp",EDGE,"E94"),sQuery(id+"F0.wireOp",EDGE,"E95"),sQuery(id+"F0.wireOp",EDGE,"E96"),sQuery(id+"F0.wireOp",EDGE,"E97"),sQuery(id+"F0.wireOp",EDGE,"E98"),sQuery(id+"F0.wireOp",EDGE,"E99"),sQuery(id+"F0.wireOp",EDGE,"E100"),sQuery(id+"F0.wireOp",EDGE,"E101"),sQuery(id+"F0.wireOp",EDGE,"E102"),sQuery(id+"F0.wireOp",EDGE,"E103"),sQuery(id+"F0.wireOp",EDGE,"E104"),sQuery(id+"F0.wireOp",EDGE,"E105"),sQuery(id+"F0.wireOp",EDGE,"E106"),sQuery(id+"F0.wireOp",EDGE,"E107"),sQuery(id+"F0.wireOp",EDGE,"E108"),sQuery(id+"F0.wireOp",EDGE,"E109"),sQuery(id+"F0.wireOp",EDGE,"E110"),sQuery(id+"F0.wireOp",EDGE,"E111"),sQuery(id+"F0.wireOp",EDGE,"E112"),sQuery(id+"F0.wireOp",EDGE,"E113"),sQuery(id+"F0.wireOp",EDGE,"E114"),sQuery(id+"F0.wireOp",EDGE,"E115"),sQuery(id+"F0.wireOp",EDGE,"E116"),sQuery(id+"F0.wireOp",EDGE,"E117"),sQuery(id+"F0.wireOp",EDGE,"E118"),sQuery(id+"F0.wireOp",EDGE,"E119"),sQuery(id+"F0.wireOp",EDGE,"E120"),sQuery(id+"F0.wireOp",EDGE,"E121"),sQuery(id+"F0.wireOp",EDGE,"E122"),sQuery(id+"F0.wireOp",EDGE,"E123"),sQuery(id+"F0.wireOp",EDGE,"E124"),sQuery(id+"F0.wireOp",EDGE,"E125"),sQuery(id+"F0.wireOp",EDGE,"E126"),sQuery(id+"F0.wireOp",EDGE,"E127"),sQuery(id+"F0.wireOp",EDGE,"E128"),sQuery(id+"F0.wireOp",EDGE,"E129"),sQuery(id+"F0.wireOp",EDGE,"E130"),sQuery(id+"F0.wireOp",EDGE,"E131"),sQuery(id+"F0.wireOp",EDGE,"E132"),sQuery(id+"F0.wireOp",EDGE,"E133"),sQuery(id+"F0.wireOp",EDGE,"E134"),sQuery(id+"F0.wireOp",EDGE,"E135"),sQuery(id+"F0.wireOp",EDGE,"E136"),sQuery(id+"F0.wireOp",EDGE,"E137"),sQuery(id+"F0.wireOp",EDGE,"E138"),sQuery(id+"F0.wireOp",EDGE,"E139"),sQuery(id+"F0.wireOp",EDGE,"E140"),sQuery(id+"F0.wireOp",EDGE,"E141"),sQuery(id+"F0.wireOp",EDGE,"E142"),sQuery(id+"F0.wireOp",EDGE,"E143"),sQuery(id+"F0.wireOp",EDGE,"E144"),sQuery(id+"F0.wireOp",EDGE,"E145"),sQuery(id+"F0.wireOp",EDGE,"E146"),sQuery(id+"F0.wireOp",EDGE,"E147"),sQuery(id+"F0.wireOp",EDGE,"E148"),sQuery(id+"F0.wireOp",EDGE,"E149"),sQuery(id+"F0.wireOp",EDGE,"E150"),sQuery(id+"F0.wireOp",EDGE,"E151"),sQuery(id+"F0.wireOp",EDGE,"E152"),sQuery(id+"F0.wireOp",EDGE,"E153"),sQuery(id+"F0.wireOp",EDGE,"E154"),sQuery(id+"F0.wireOp",EDGE,"E155"),sQuery(id+"F0.wireOp",EDGE,"E156"),sQuery(id+"F0.wireOp",EDGE,"E157"),sQuery(id+"F0.wireOp",EDGE,"E158"),sQuery(id+"F0.wireOp",EDGE,"E159"),sQuery(id+"F0.wireOp",EDGE,"E160"),sQuery(id+"F0.wireOp",EDGE,"E161"),sQuery(id+"F0.wireOp",EDGE,"E162"),sQuery(id+"F0.wireOp",EDGE,"E163"),sQuery(id+"F0.wireOp",EDGE,"E164"),sQuery(id+"F0.wireOp",EDGE,"E165"),sQuery(id+"F0.wireOp",EDGE,"E166"),sQuery(id+"F0.wireOp",EDGE,"E167"),sQuery(id+"F0.wireOp",EDGE,"E168"),sQuery(id+"F0.wireOp",EDGE,"E169"),sQuery(id+"F0.wireOp",EDGE,"E170"),sQuery(id+"F0.wireOp",EDGE,"E171"),sQuery(id+"F0.wireOp",EDGE,"E172"),sQuery(id+"F0.wireOp",EDGE,"E173"),sQuery(id+"F0.wireOp",EDGE,"E174"),sQuery(id+"F0.wireOp",EDGE,"E175"),sQuery(id+"F0.wireOp",EDGE,"E176"),sQuery(id+"F0.wireOp",EDGE,"E177"),sQuery(id+"F0.wireOp",EDGE,"E178"),sQuery(id+"F0.wireOp",EDGE,"E179"),sQuery(id+"F0.wireOp",EDGE,"E180"),sQuery(id+"F0.wireOp",EDGE,"E181"),sQuery(id+"F0.wireOp",EDGE,"E182"),sQuery(id+"F0.wireOp",EDGE,"E183"),sQuery(id+"F0.wireOp",EDGE,"E184"),sQuery(id+"F0.wireOp",EDGE,"E185"),sQuery(id+"F0.wireOp",EDGE,"E186"),sQuery(id+"F0.wireOp",EDGE,"E187"),sQuery(id+"F0.wireOp",EDGE,"E188"),sQuery(id+"F0.wireOp",EDGE,"E189"),sQuery(id+"F0.wireOp",EDGE,"E190"),sQuery(id+"F0.wireOp",EDGE,"E191"),sQuery(id+"F0.wireOp",EDGE,"E192"),sQuery(id+"F0.wireOp",EDGE,"E193"),sQuery(id+"F0.wireOp",EDGE,"E194"),sQuery(id+"F0.wireOp",EDGE,"E195"),sQuery(id+"F0.wireOp",EDGE,"E196"),sQuery(id+"F0.wireOp",EDGE,"E197"),sQuery(id+"F0.wireOp",EDGE,"E198"),sQuery(id+"F0.wireOp",EDGE,"E199"),sQuery(id+"F0.wireOp",EDGE,"E200"),sQuery(id+"F0.wireOp",EDGE,"E201"),sQuery(id+"F0.wireOp",EDGE,"E202"),sQuery(id+"F0.wireOp",EDGE,"E203"),sQuery(id+"F0.wireOp",EDGE,"E204"),sQuery(id+"F0.wireOp",EDGE,"E205"),sQuery(id+"F0.wireOp",EDGE,"E206"),sQuery(id+"F0.wireOp",EDGE,"E207"),sQuery(id+"F0.wireOp",EDGE,"E208"),sQuery(id+"F0.wireOp",EDGE,"E209"),sQuery(id+"F0.wireOp",EDGE,"E210"),sQuery(id+"F0.wireOp",EDGE,"E211"),sQuery(id+"F0.wireOp",EDGE,"E212"),sQuery(id+"F0.wireOp",EDGE,"E213"),sQuery(id+"F0.wireOp",EDGE,"E214"),sQuery(id+"F0.wireOp",EDGE,"E215"),sQuery(id+"F0.wireOp",EDGE,"E216"),sQuery(id+"F0.wireOp",EDGE,"E217"),sQuery(id+"F0.wireOp",EDGE,"E218"),sQuery(id+"F0.wireOp",EDGE,"E219"),sQuery(id+"F0.wireOp",EDGE,"E220"),sQuery(id+"F0.wireOp",EDGE,"E221"),sQuery(id+"F0.wireOp",EDGE,"E222"),sQuery(id+"F0.wireOp",EDGE,"E223"),sQuery(id+"F0.wireOp",EDGE,"E224"),sQuery(id+"F0.wireOp",EDGE,"E225"),sQuery(id+"F0.wireOp",EDGE,"E226"),sQuery(id+"F0.wireOp",EDGE,"E227"),sQuery(id+"F0.wireOp",EDGE,"E228"),sQuery(id+"F0.wireOp",EDGE,"E229"),sQuery(id+"F0.wireOp",EDGE,"E230"),sQuery(id+"F0.wireOp",EDGE,"E231"),sQuery(id+"F0.wireOp",EDGE,"E232"),sQuery(id+"F0.wireOp",EDGE,"E233"),sQuery(id+"F0.wireOp",EDGE,"E234"),sQuery(id+"F0.wireOp",EDGE,"E235"),sQuery(id+"F0.wireOp",EDGE,"E236"),sQuery(id+"F0.wireOp",EDGE,"E237"),sQuery(id+"F0.wireOp",EDGE,"E238"),sQuery(id+"F0.wireOp",EDGE,"E239"),sQuery(id+"F0.wireOp",EDGE,"E240"),sQuery(id+"F0.wireOp",EDGE,"E241"),sQuery(id+"F0.wireOp",EDGE,"E242"),sQuery(id+"F0.wireOp",EDGE,"E243"),sQuery(id+"F0.wireOp",EDGE,"E244"),sQuery(id+"F0.wireOp",EDGE,"E245"),sQuery(id+"F0.wireOp",EDGE,"E246"),sQuery(id+"F0.wireOp",EDGE,"E247"),sQuery(id+"F0.wireOp",EDGE,"E248"),sQuery(id+"F0.wireOp",EDGE,"E249"),sQuery(id+"F0.wireOp",EDGE,"E250"),sQuery(id+"F0.wireOp",EDGE,"E251"),sQuery(id+"F0.wireOp",EDGE,"E252"),sQuery(id+"F0.wireOp",EDGE,"E253"),sQuery(id+"F0.wireOp",EDGE,"E254"),sQuery(id+"F0.wireOp",EDGE,"E255"),sQuery(id+"F0.wireOp",EDGE,"E256"),sQuery(id+"F0.wireOp",EDGE,"E257"),sQuery(id+"F0.wireOp",EDGE,"E258"),sQuery(id+"F0.wireOp",EDGE,"E259"),sQuery(id+"F0.wireOp",EDGE,"E260"),sQuery(id+"F0.wireOp",EDGE,"E261"),sQuery(id+"F0.wireOp",EDGE,"E262"),sQuery(id+"F0.wireOp",EDGE,"E263"),sQuery(id+"F0.wireOp",EDGE,"E264"),sQuery(id+"F0.wireOp",EDGE,"E265"),sQuery(id+"F0.wireOp",EDGE,"E266"),sQuery(id+"F0.wireOp",EDGE,"E267"),sQuery(id+"F0.wireOp",EDGE,"E268"),sQuery(id+"F0.wireOp",EDGE,"E269"),sQuery(id+"F0.wireOp",EDGE,"E270"),sQuery(id+"F0.wireOp",EDGE,"E271"),sQuery(id+"F0.wireOp",EDGE,"E272"),sQuery(id+"F0.wireOp",EDGE,"E273"),sQuery(id+"F0.wireOp",EDGE,"E274"),sQuery(id+"F0.wireOp",EDGE,"E275"),sQuery(id+"F0.wireOp",EDGE,"E276"),sQuery(id+"F0.wireOp",EDGE,"E277"),sQuery(id+"F0.wireOp",EDGE,"E278"),sQuery(id+"F0.wireOp",EDGE,"E279"),sQuery(id+"F0.wireOp",EDGE,"E280"),sQuery(id+"F0.wireOp",EDGE,"E281"),sQuery(id+"F0.wireOp",EDGE,"E282"),sQuery(id+"F0.wireOp",EDGE,"E283"),sQuery(id+"F0.wireOp",EDGE,"E284"),sQuery(id+"F0.wireOp",EDGE,"E285"),sQuery(id+"F0.wireOp",EDGE,"E286"),sQuery(id+"F0.wireOp",EDGE,"E287"),sQuery(id+"F0.wireOp",EDGE,"E288"),sQuery(id+"F0.wireOp",EDGE,"E289"),sQuery(id+"F0.wireOp",EDGE,"E290"),sQuery(id+"F0.wireOp",EDGE,"E291"),sQuery(id+"F0.wireOp",EDGE,"E292"),sQuery(id+"F0.wireOp",EDGE,"E293"),sQuery(id+"F0.wireOp",EDGE,"E294"),sQuery(id+"F0.wireOp",EDGE,"E295"),sQuery(id+"F0.wireOp",EDGE,"E296"),sQuery(id+"F0.wireOp",EDGE,"E297"),sQuery(id+"F0.wireOp",EDGE,"E298"),sQuery(id+"F0.wireOp",EDGE,"E299"),sQuery(id+"F0.wireOp",EDGE,"E300"),sQuery(id+"F0.wireOp",EDGE,"E301"),sQuery(id+"F0.wireOp",EDGE,"E302"),sQuery(id+"F0.wireOp",EDGE,"E303"),sQuery(id+"F0.wireOp",EDGE,"E304"),sQuery(id+"F0.wireOp",EDGE,"E305"),sQuery(id+"F0.wireOp",EDGE,"E306"),sQuery(id+"F0.wireOp",EDGE,"E307"),sQuery(id+"F0.wireOp",EDGE,"E308"),sQuery(id+"F0.wireOp",EDGE,"E309"),sQuery(id+"F0.wireOp",EDGE,"E310"),sQuery(id+"F0.wireOp",EDGE,"E311"),sQuery(id+"F0.wireOp",EDGE,"E312"),sQuery(id+"F0.wireOp",EDGE,"E313"),sQuery(id+"F0.wireOp",EDGE,"E314"),sQuery(id+"F0.wireOp",EDGE,"E315"),sQuery(id+"F0.wireOp",EDGE,"E316"),sQuery(id+"F0.wireOp",EDGE,"E317"),sQuery(id+"F0.wireOp",EDGE,"E318"),sQuery(id+"F0.wireOp",EDGE,"E319"),sQuery(id+"F0.wireOp",EDGE,"E320"),sQuery(id+"F0.wireOp",EDGE,"E321"),sQuery(id+"F0.wireOp",EDGE,"E322"),sQuery(id+"F0.wireOp",EDGE,"E323"),sQuery(id+"F0.wireOp",EDGE,"E324"),sQuery(id+"F0.wireOp",EDGE,"E325"),sQuery(id+"F0.wireOp",EDGE,"E326"),sQuery(id+"F0.wireOp",EDGE,"E327"),sQuery(id+"F0.wireOp",EDGE,"E328"),sQuery(id+"F0.wireOp",EDGE,"E329"),sQuery(id+"F0.wireOp",EDGE,"E330"),sQuery(id+"F0.wireOp",EDGE,"E331"),sQuery(id+"F0.wireOp",EDGE,"E332"),sQuery(id+"F0.wireOp",EDGE,"E333"),sQuery(id+"F0.wireOp",EDGE,"E334"),sQuery(id+"F0.wireOp",EDGE,"E335"),sQuery(id+"F0.wireOp",EDGE,"E336"),sQuery(id+"F0.wireOp",EDGE,"E337"),sQuery(id+"F0.wireOp",EDGE,"E338"),sQuery(id+"F0.wireOp",EDGE,"E339"),sQuery(id+"F0.wireOp",EDGE,"E340"),sQuery(id+"F0.wireOp",EDGE,"E341"),sQuery(id+"F0.wireOp",EDGE,"E342"),sQuery(id+"F0.wireOp",EDGE,"E343"),sQuery(id+"F0.wireOp",EDGE,"E344"),sQuery(id+"F0.wireOp",EDGE,"E345"),sQuery(id+"F0.wireOp",EDGE,"E346"),sQuery(id+"F0.wireOp",EDGE,"E347"),sQuery(id+"F0.wireOp",EDGE,"E348"),sQuery(id+"F0.wireOp",EDGE,"E349"),sQuery(id+"F0.wireOp",EDGE,"E350"),sQuery(id+"F0.wireOp",EDGE,"E351"),sQuery(id+"F0.wireOp",EDGE,"E352"),sQuery(id+"F0.wireOp",EDGE,"E353"),sQuery(id+"F0.wireOp",EDGE,"E354"),sQuery(id+"F0.wireOp",EDGE,"E355"),sQuery(id+"F0.wireOp",EDGE,"E356"),sQuery(id+"F0.wireOp",EDGE,"E357"),sQuery(id+"F0.wireOp",EDGE,"E358"),sQuery(id+"F0.wireOp",EDGE,"E359"),sQuery(id+"F0.wireOp",EDGE,"E360"),sQuery(id+"F0.wireOp",EDGE,"E361"),sQuery(id+"F0.wireOp",EDGE,"E362"),sQuery(id+"F0.wireOp",EDGE,"E363"),sQuery(id+"F0.wireOp",EDGE,"E364"),sQuery(id+"F0.wireOp",EDGE,"E365"),sQuery(id+"F0.wireOp",EDGE,"E366"),sQuery(id+"F0.wireOp",EDGE,"E367"),sQuery(id+"F0.wireOp",EDGE,"E368"),sQuery(id+"F0.wireOp",EDGE,"E369"),sQuery(id+"F0.wireOp",EDGE,"E370"),sQuery(id+"F0.wireOp",EDGE,"E371"),sQuery(id+"F0.wireOp",EDGE,"E372"),sQuery(id+"F0.wireOp",EDGE,"E373"),sQuery(id+"F0.wireOp",EDGE,"E374"),sQuery(id+"F0.wireOp",EDGE,"E375"),sQuery(id+"F0.wireOp",EDGE,"E376"),sQuery(id+"F0.wireOp",EDGE,"E377"),sQuery(id+"F0.wireOp",EDGE,"E378"),sQuery(id+"F0.wireOp",EDGE,"E379"),sQuery(id+"F0.wireOp",EDGE,"E380"),sQuery(id+"F0.wireOp",EDGE,"E381"),sQuery(id+"F0.wireOp",EDGE,"E382"),sQuery(id+"F0.wireOp",EDGE,"E383"),sQuery(id+"F0.wireOp",EDGE,"E384"),sQuery(id+"F0.wireOp",EDGE,"E385"),sQuery(id+"F0.wireOp",EDGE,"E386"),sQuery(id+"F0.wireOp",EDGE,"E387"),sQuery(id+"F0.wireOp",EDGE,"E388"),sQuery(id+"F0.wireOp",EDGE,"E389"),sQuery(id+"F0.wireOp",EDGE,"E390"),sQuery(id+"F0.wireOp",EDGE,"E391"),sQuery(id+"F0.wireOp",EDGE,"E392"),sQuery(id+"F0.wireOp",EDGE,"E393"),sQuery(id+"F0.wireOp",EDGE,"E394"),sQuery(id+"F0.wireOp",EDGE,"E395"),sQuery(id+"F0.wireOp",EDGE,"E396"),sQuery(id+"F0.wireOp",EDGE,"E397"),sQuery(id+"F0.wireOp",EDGE,"E398"),sQuery(id+"F0.wireOp",EDGE,"E399"),sQuery(id+"F0.wireOp",EDGE,"E400"),sQuery(id+"F0.wireOp",EDGE,"E401"),sQuery(id+"F0.wireOp",EDGE,"E402"),sQuery(id+"F0.wireOp",EDGE,"E403"),sQuery(id+"F0.wireOp",EDGE,"E404"),sQuery(id+"F0.wireOp",EDGE,"E405"),sQuery(id+"F0.wireOp",EDGE,"E406"),sQuery(id+"F0.wireOp",EDGE,"E407"),sQuery(id+"F0.wireOp",EDGE,"E408"),sQuery(id+"F0.wireOp",EDGE,"E409"),sQuery(id+"F0.wireOp",EDGE,"E410"),sQuery(id+"F0.wireOp",EDGE,"E411"),sQuery(id+"F0.wireOp",EDGE,"E412"),sQuery(id+"F0.wireOp",EDGE,"E413"),sQuery(id+"F0.wireOp",EDGE,"E414"),sQuery(id+"F0.wireOp",EDGE,"E415"),sQuery(id+"F0.wireOp",EDGE,"E416"),sQuery(id+"F0.wireOp",EDGE,"E417"),sQuery(id+"F0.wireOp",EDGE,"E418"),sQuery(id+"F0.wireOp",EDGE,"E419"),sQuery(id+"F0.wireOp",EDGE,"E420"),sQuery(id+"F0.wireOp",EDGE,"E421"),sQuery(id+"F0.wireOp",EDGE,"E422"),sQuery(id+"F0.wireOp",EDGE,"E423"),sQuery(id+"F0.wireOp",EDGE,"E424"),sQuery(id+"F0.wireOp",EDGE,"E425"),sQuery(id+"F0.wireOp",EDGE,"E426"),sQuery(id+"F0.wireOp",EDGE,"E427"),sQuery(id+"F0.wireOp",EDGE,"E428"),sQuery(id+"F0.wireOp",EDGE,"E429"),sQuery(id+"F0.wireOp",EDGE,"E430"),sQuery(id+"F0.wireOp",EDGE,"E431"),sQuery(id+"F0.wireOp",EDGE,"E432"),sQuery(id+"F0.wireOp",EDGE,"E433"),sQuery(id+"F0.wireOp",EDGE,"E434"),sQuery(id+"F0.wireOp",EDGE,"E435"),sQuery(id+"F0.wireOp",EDGE,"E436"),sQuery(id+"F0.wireOp",EDGE,"E437"),sQuery(id+"F0.wireOp",EDGE,"E438"),sQuery(id+"F0.wireOp",EDGE,"E439"),sQuery(id+"F0.wireOp",EDGE,"E440"),sQuery(id+"F0.wireOp",EDGE,"E441"),sQuery(id+"F0.wireOp",EDGE,"E442"),sQuery(id+"F0.wireOp",EDGE,"E443"),sQuery(id+"F0.wireOp",EDGE,"E444"),sQuery(id+"F0.wireOp",EDGE,"E445"),sQuery(id+"F0.wireOp",EDGE,"E446"),sQuery(id+"F0.wireOp",EDGE,"E447"),sQuery(id+"F0.wireOp",EDGE,"E448"),sQuery(id+"F0.wireOp",EDGE,"E449"),sQuery(id+"F0.wireOp",EDGE,"E450"),sQuery(id+"F0.wireOp",EDGE,"E451"),sQuery(id+"F0.wireOp",EDGE,"E452"),sQuery(id+"F0.wireOp",EDGE,"E453"),sQuery(id+"F0.wireOp",EDGE,"E454"),sQuery(id+"F0.wireOp",EDGE,"E455"),sQuery(id+"F0.wireOp",EDGE,"E456"),sQuery(id+"F0.wireOp",EDGE,"E457"),sQuery(id+"F0.wireOp",EDGE,"E458"),sQuery(id+"F0.wireOp",EDGE,"E459"),sQuery(id+"F0.wireOp",EDGE,"E460"),sQuery(id+"F0.wireOp",EDGE,"E461"),sQuery(id+"F0.wireOp",EDGE,"E462"),sQuery(id+"F0.wireOp",EDGE,"E463"),sQuery(id+"F0.wireOp",EDGE,"E464"),sQuery(id+"F0.wireOp",EDGE,"E465"),sQuery(id+"F0.wireOp",EDGE,"E466"),sQuery(id+"F0.wireOp",EDGE,"E467"),sQuery(id+"F0.wireOp",EDGE,"E468"),sQuery(id+"F0.wireOp",EDGE,"E469"),sQuery(id+"F0.wireOp",EDGE,"E470"),sQuery(id+"F0.wireOp",EDGE,"E471"),sQuery(id+"F0.wireOp",EDGE,"E472"),sQuery(id+"F0.wireOp",EDGE,"E473"),sQuery(id+"F0.wireOp",EDGE,"E474"),sQuery(id+"F0.wireOp",EDGE,"E475"),sQuery(id+"F0.wireOp",EDGE,"E476"),sQuery(id+"F0.wireOp",EDGE,"E477"),sQuery(id+"F0.wireOp",EDGE,"E478"),sQuery(id+"F0.wireOp",EDGE,"E479"),sQuery(id+"F0.wireOp",EDGE,"E480"),sQuery(id+"F0.wireOp",EDGE,"E481"),sQuery(id+"F0.wireOp",EDGE,"E482"),sQuery(id+"F0.wireOp",EDGE,"E483"),sQuery(id+"F0.wireOp",EDGE,"E484"),sQuery(id+"F0.wireOp",EDGE,"E485"),sQuery(id+"F0.wireOp",EDGE,"E486"),sQuery(id+"F0.wireOp",EDGE,"E487"),sQuery(id+"F0.wireOp",EDGE,"E488"),sQuery(id+"F0.wireOp",EDGE,"E489"),sQuery(id+"F0.wireOp",EDGE,"E490"),sQuery(id+"F0.wireOp",EDGE,"E491"),sQuery(id+"F0.wireOp",EDGE,"E492"),sQuery(id+"F0.wireOp",EDGE,"E493"),sQuery(id+"F0.wireOp",EDGE,"E494"),sQuery(id+"F0.wireOp",EDGE,"E495"),sQuery(id+"F0.wireOp",EDGE,"E496"),sQuery(id+"F0.wireOp",EDGE,"E497"),sQuery(id+"F0.wireOp",EDGE,"E498"),sQuery(id+"F0.wireOp",EDGE,"E499"),sQuery(id+"F0.wireOp",EDGE,"E500"),sQuery(id+"F0.wireOp",EDGE,"E501"),sQuery(id+"F0.wireOp",EDGE,"E502"),sQuery(id+"F0.wireOp",EDGE,"E503"),sQuery(id+"F0.wireOp",EDGE,"E504"),sQuery(id+"F0.wireOp",EDGE,"E505"),sQuery(id+"F0.wireOp",EDGE,"E506"),sQuery(id+"F0.wireOp",EDGE,"E507"),sQuery(id+"F0.wireOp",EDGE,"E508"),sQuery(id+"F0.wireOp",EDGE,"E509"),sQuery(id+"F0.wireOp",EDGE,"E510"),sQuery(id+"F0.wireOp",EDGE,"E511"),sQuery(id+"F0.wireOp",EDGE,"E512"),sQuery(id+"F0.wireOp",EDGE,"E513"),sQuery(id+"F0.wireOp",EDGE,"E514"),sQuery(id+"F0.wireOp",EDGE,"E515"),sQuery(id+"F0.wireOp",EDGE,"E516"),sQuery(id+"F0.wireOp",EDGE,"E517"),sQuery(id+"F0.wireOp",EDGE,"E518"),sQuery(id+"F0.wireOp",EDGE,"E519"),sQuery(id+"F0.wireOp",EDGE,"E520"),sQuery(id+"F0.wireOp",EDGE,"E521"),sQuery(id+"F0.wireOp",EDGE,"E522"),sQuery(id+"F0.wireOp",EDGE,"E523"),sQuery(id+"F0.wireOp",EDGE,"E524"),sQuery(id+"F0.wireOp",EDGE,"E525"),sQuery(id+"F0.wireOp",EDGE,"E526"),sQuery(id+"F0.wireOp",EDGE,"E527"),sQuery(id+"F0.wireOp",EDGE,"E528"),sQuery(id+"F0.wireOp",EDGE,"E529"),sQuery(id+"F0.wireOp",EDGE,"E530"),sQuery(id+"F0.wireOp",EDGE,"E531"),sQuery(id+"F0.wireOp",EDGE,"E532"),sQuery(id+"F0.wireOp",EDGE,"E533"),sQuery(id+"F0.wireOp",EDGE,"E534"),sQuery(id+"F0.wireOp",EDGE,"E535"),sQuery(id+"F0.wireOp",EDGE,"E536"),sQuery(id+"F0.wireOp",EDGE,"E537"),sQuery(id+"F0.wireOp",EDGE,"E538"),sQuery(id+"F0.wireOp",EDGE,"E539"),sQuery(id+"F0.wireOp",EDGE,"E540"),sQuery(id+"F0.wireOp",EDGE,"E541"),sQuery(id+"F0.wireOp",EDGE,"E542"),sQuery(id+"F0.wireOp",EDGE,"E543"),sQuery(id+"F0.wireOp",EDGE,"E544"),sQuery(id+"F0.wireOp",EDGE,"E545"),sQuery(id+"F0.wireOp",EDGE,"E546"),sQuery(id+"F0.wireOp",EDGE,"E547"),sQuery(id+"F0.wireOp",EDGE,"E548"),sQuery(id+"F0.wireOp",EDGE,"E549"),sQuery(id+"F0.wireOp",EDGE,"E550"),sQuery(id+"F0.wireOp",EDGE,"E551"),sQuery(id+"F0.wireOp",EDGE,"E552"),sQuery(id+"F0.wireOp",EDGE,"E553"),sQuery(id+"F0.wireOp",EDGE,"E554"),sQuery(id+"F0.wireOp",EDGE,"E555"),sQuery(id+"F2.wireOp",EDGE,"E863"),sQuery(id+"F2.wireOp",EDGE,"E864"),sQuery(id+"F2.wireOp",EDGE,"E865"),sQuery(id+"F2.wireOp",EDGE,"E866"),sQuery(id+"F2.wireOp",EDGE,"E867"),sQuery(id+"F2.wireOp",EDGE,"E868"),sQuery(id+"F2.wireOp",EDGE,"E869"),sQuery(id+"F2.wireOp",EDGE,"E870"),sQuery(id+"F2.wireOp",EDGE,"E871"),sQuery(id+"F2.wireOp",EDGE,"E872"),sQuery(id+"F2.wireOp",EDGE,"E873"),sQuery(id+"F2.wireOp",EDGE,"E874"),sQuery(id+"F2.wireOp",EDGE,"E875"),sQuery(id+"F2.wireOp",EDGE,"E876"),sQuery(id+"F2.wireOp",EDGE,"E877"),sQuery(id+"F2.wireOp",EDGE,"E878"),sQuery(id+"F2.wireOp",EDGE,"E879"),sQuery(id+"F2.wireOp",EDGE,"E880"),sQuery(id+"F2.wireOp",EDGE,"E881"),sQuery(id+"F2.wireOp",EDGE,"E882"),sQuery(id+"F2.wireOp",EDGE,"E883"),sQuery(id+"F2.wireOp",EDGE,"E884"),sQuery(id+"F2.wireOp",EDGE,"E885"),sQuery(id+"F2.wireOp",EDGE,"E886"),sQuery(id+"F2.wireOp",EDGE,"E887"),sQuery(id+"F2.wireOp",EDGE,"E888"),sQuery(id+"F2.wireOp",EDGE,"E889"),sQuery(id+"F2.wireOp",EDGE,"E890"),sQuery(id+"F2.wireOp",EDGE,"E891"),sQuery(id+"F2.wireOp",EDGE,"E892"),sQuery(id+"F2.wireOp",EDGE,"E893"),sQuery(id+"F2.wireOp",EDGE,"E894"),sQuery(id+"F2.wireOp",EDGE,"E895"),sQuery(id+"F2.wireOp",EDGE,"E896"),sQuery(id+"F2.wireOp",EDGE,"E897"),sQuery(id+"F2.wireOp",EDGE,"E898"),sQuery(id+"F2.wireOp",EDGE,"E899"),sQuery(id+"F2.wireOp",EDGE,"E900"),sQuery(id+"F2.wireOp",EDGE,"E901"),sQuery(id+"F2.wireOp",EDGE,"E902"),sQuery(id+"F2.wireOp",EDGE,"E903"),sQuery(id+"F2.wireOp",EDGE,"E904"),sQuery(id+"F2.wireOp",EDGE,"E905"),sQuery(id+"F2.wireOp",EDGE,"E906"),sQuery(id+"F2.wireOp",EDGE,"E907"),sQuery(id+"F2.wireOp",EDGE,"E908"),sQuery(id+"F2.wireOp",EDGE,"E909"),sQuery(id+"F2.wireOp",EDGE,"E910"),sQuery(id+"F2.wireOp",EDGE,"E911"),sQuery(id+"F2.wireOp",EDGE,"E912"),sQuery(id+"F2.wireOp",EDGE,"E913"),sQuery(id+"F2.wireOp",EDGE,"E914"),sQuery(id+"F2.wireOp",EDGE,"E915"),sQuery(id+"F2.wireOp",EDGE,"E916"),sQuery(id+"F2.wireOp",EDGE,"E917"),sQuery(id+"F2.wireOp",EDGE,"E918"),sQuery(id+"F2.wireOp",EDGE,"E919"),sQuery(id+"F2.wireOp",EDGE,"E920"),sQuery(id+"F2.wireOp",EDGE,"E921"),sQuery(id+"F2.wireOp",EDGE,"E922"),sQuery(id+"F2.wireOp",EDGE,"E923"),sQuery(id+"F2.wireOp",EDGE,"E924"),sQuery(id+"F2.wireOp",EDGE,"E925"),sQuery(id+"F2.wireOp",EDGE,"E926"),sQuery(id+"F2.wireOp",EDGE,"E927"),sQuery(id+"F2.wireOp",EDGE,"E928"),sQuery(id+"F2.wireOp",EDGE,"E929"),sQuery(id+"F2.wireOp",EDGE,"E930"),sQuery(id+"F2.wireOp",EDGE,"E931"),sQuery(id+"F2.wireOp",EDGE,"E932"),sQuery(id+"F2.wireOp",EDGE,"E933"),sQuery(id+"F2.wireOp",EDGE,"E934"),sQuery(id+"F2.wireOp",EDGE,"E935"),sQuery(id+"F2.wireOp",EDGE,"E936"),sQuery(id+"F2.wireOp",EDGE,"E937"),sQuery(id+"F2.wireOp",EDGE,"E938"),sQuery(id+"F2.wireOp",EDGE,"E939"),sQuery(id+"F2.wireOp",EDGE,"E940"),sQuery(id+"F2.wireOp",EDGE,"E941"),sQuery(id+"F2.wireOp",EDGE,"E942"),sQuery(id+"F2.wireOp",EDGE,"E943"),sQuery(id+"F2.wireOp",EDGE,"E944"),sQuery(id+"F2.wireOp",EDGE,"E945"),sQuery(id+"F2.wireOp",EDGE,"E946"),sQuery(id+"F2.wireOp",EDGE,"E947"),sQuery(id+"F2.wireOp",EDGE,"E948"),sQuery(id+"F2.wireOp",EDGE,"E949"),sQuery(id+"F2.wireOp",EDGE,"E950"),sQuery(id+"F2.wireOp",EDGE,"E951"),sQuery(id+"F2.wireOp",EDGE,"E952"),sQuery(id+"F2.wireOp",EDGE,"E953"),sQuery(id+"F2.wireOp",EDGE,"E954"),sQuery(id+"F2.wireOp",EDGE,"E955"),sQuery(id+"F2.wireOp",EDGE,"E956"),sQuery(id+"F2.wireOp",EDGE,"E957"),sQuery(id+"F2.wireOp",EDGE,"E958"),sQuery(id+"F2.wireOp",EDGE,"E959"),sQuery(id+"F2.wireOp",EDGE,"E960"),sQuery(id+"F2.wireOp",EDGE,"E961"),sQuery(id+"F2.wireOp",EDGE,"E962"),sQuery(id+"F2.wireOp",EDGE,"E963"),sQuery(id+"F2.wireOp",EDGE,"E964"),sQuery(id+"F2.wireOp",EDGE,"E965"),sQuery(id+"F2.wireOp",EDGE,"E966"),sQuery(id+"F2.wireOp",EDGE,"E967"),sQuery(id+"F2.wireOp",EDGE,"E968"),sQuery(id+"F2.wireOp",EDGE,"E969"),sQuery(id+"F2.wireOp",EDGE,"E970"),sQuery(id+"F2.wireOp",EDGE,"E971"),sQuery(id+"F2.wireOp",EDGE,"E972"),sQuery(id+"F2.wireOp",EDGE,"E973"),sQuery(id+"F2.wireOp",EDGE,"E974"),sQuery(id+"F2.wireOp",EDGE,"E975"),sQuery(id+"F2.wireOp",EDGE,"E976"),sQuery(id+"F2.wireOp",EDGE,"E977"),sQuery(id+"F2.wireOp",EDGE,"E978"),sQuery(id+"F2.wireOp",EDGE,"E979"),sQuery(id+"F2.wireOp",EDGE,"E980"),sQuery(id+"F2.wireOp",EDGE,"E981"),sQuery(id+"F2.wireOp",EDGE,"E982"),sQuery(id+"F2.wireOp",EDGE,"E983"),sQuery(id+"F2.wireOp",EDGE,"E984"),sQuery(id+"F2.wireOp",EDGE,"E985"),sQuery(id+"F2.wireOp",EDGE,"E986"),sQuery(id+"F2.wireOp",EDGE,"E987"),sQuery(id+"F2.wireOp",EDGE,"E988"),sQuery(id+"F2.wireOp",EDGE,"E989"),sQuery(id+"F2.wireOp",EDGE,"E990"),sQuery(id+"F2.wireOp",EDGE,"E991"),sQuery(id+"F2.wireOp",EDGE,"E992"),sQuery(id+"F2.wireOp",EDGE,"E993"),sQuery(id+"F2.wireOp",EDGE,"E994"),sQuery(id+"F2.wireOp",EDGE,"E995"),sQuery(id+"F2.wireOp",EDGE,"E996"),sQuery(id+"F2.wireOp",EDGE,"E997"),sQuery(id+"F2.wireOp",EDGE,"E998"),sQuery(id+"F2.wireOp",EDGE,"E999"),sQuery(id+"F2.wireOp",EDGE,"E1000"),sQuery(id+"F2.wireOp",EDGE,"E1001"),sQuery(id+"F2.wireOp",EDGE,"E1002"),sQuery(id+"F2.wireOp",EDGE,"E1003"),sQuery(id+"F2.wireOp",EDGE,"E1004"),sQuery(id+"F2.wireOp",EDGE,"E1005"),sQuery(id+"F2.wireOp",EDGE,"E1006"),sQuery(id+"F2.wireOp",EDGE,"E1007"),sQuery(id+"F2.wireOp",EDGE,"E1008"),sQuery(id+"F2.wireOp",EDGE,"E1009"),sQuery(id+"F2.wireOp",EDGE,"E1010"),sQuery(id+"F2.wireOp",EDGE,"E1011"),sQuery(id+"F2.wireOp",EDGE,"E1012"),sQuery(id+"F2.wireOp",EDGE,"E1013"),sQuery(id+"F2.wireOp",EDGE,"E1014"),sQuery(id+"F2.wireOp",EDGE,"E1015"),sQuery(id+"F2.wireOp",EDGE,"E1016"),sQuery(id+"F2.wireOp",EDGE,"E1017"),sQuery(id+"F2.wireOp",EDGE,"E1018"),sQuery(id+"F2.wireOp",EDGE,"E1019"),sQuery(id+"F2.wireOp",EDGE,"E1020"),sQuery(id+"F2.wireOp",EDGE,"E1021"),sQuery(id+"F2.wireOp",EDGE,"E1022"),sQuery(id+"F2.wireOp",EDGE,"E1023"),sQuery(id+"F2.wireOp",EDGE,"E1024"),sQuery(id+"F2.wireOp",EDGE,"E1025"),sQuery(id+"F2.wireOp",EDGE,"E1026"),sQuery(id+"F2.wireOp",EDGE,"E1027"),sQuery(id+"F2.wireOp",EDGE,"E1028"),sQuery(id+"F2.wireOp",EDGE,"E1029"),sQuery(id+"F2.wireOp",EDGE,"E1030"),sQuery(id+"F2.wireOp",EDGE,"E1031"),sQuery(id+"F2.wireOp",EDGE,"E1032"),sQuery(id+"F2.wireOp",EDGE,"E1033"),sQuery(id+"F2.wireOp",EDGE,"E1034"),sQuery(id+"F2.wireOp",EDGE,"E1035"),sQuery(id+"F2.wireOp",EDGE,"E1036"),sQuery(id+"F2.wireOp",EDGE,"E1037"),sQuery(id+"F2.wireOp",EDGE,"E1038"),sQuery(id+"F2.wireOp",EDGE,"E1039"),sQuery(id+"F2.wireOp",EDGE,"E1040"),sQuery(id+"F2.wireOp",EDGE,"E1041"),sQuery(id+"F2.wireOp",EDGE,"E1042"),sQuery(id+"F2.wireOp",EDGE,"E1043"),sQuery(id+"F2.wireOp",EDGE,"E1044"),sQuery(id+"F2.wireOp",EDGE,"E1045"),sQuery(id+"F2.wireOp",EDGE,"E1046"),sQuery(id+"F2.wireOp",EDGE,"E1047"),sQuery(id+"F2.wireOp",EDGE,"E1048"),sQuery(id+"F2.wireOp",EDGE,"E1049"),sQuery(id+"F2.wireOp",EDGE,"E1050"),sQuery(id+"F2.wireOp",EDGE,"E1051"),sQuery(id+"F2.wireOp",EDGE,"E1052"),sQuery(id+"F2.wireOp",EDGE,"E1053"),sQuery(id+"F2.wireOp",EDGE,"E1054"),sQuery(id+"F2.wireOp",EDGE,"E1055"),sQuery(id+"F2.wireOp",EDGE,"E1056"),sQuery(id+"F2.wireOp",EDGE,"E1057"),sQuery(id+"F2.wireOp",EDGE,"E1058"),sQuery(id+"F2.wireOp",EDGE,"E1059"),sQuery(id+"F2.wireOp",EDGE,"E1060"),sQuery(id+"F2.wireOp",EDGE,"E1061"),sQuery(id+"F2.wireOp",EDGE,"E1062"),sQuery(id+"F2.wireOp",EDGE,"E1063"),sQuery(id+"F2.wireOp",EDGE,"E1064"),sQuery(id+"F2.wireOp",EDGE,"E1065"),sQuery(id+"F2.wireOp",EDGE,"E1066"),sQuery(id+"F2.wireOp",EDGE,"E1067"),sQuery(id+"F2.wireOp",EDGE,"E1068"),sQuery(id+"F2.wireOp",EDGE,"E1069"),sQuery(id+"F2.wireOp",EDGE,"E1070"),sQuery(id+"F2.wireOp",EDGE,"E1071"),sQuery(id+"F2.wireOp",EDGE,"E1072"),sQuery(id+"F2.wireOp",EDGE,"E1073"),sQuery(id+"F2.wireOp",EDGE,"E1074"),sQuery(id+"F2.wireOp",EDGE,"E1075"),sQuery(id+"F2.wireOp",EDGE,"E1076"),sQuery(id+"F2.wireOp",EDGE,"E1077"),sQuery(id+"F2.wireOp",EDGE,"E1078"),sQuery(id+"F2.wireOp",EDGE,"E1079"),sQuery(id+"F2.wireOp",EDGE,"E1080"),sQuery(id+"F2.wireOp",EDGE,"E1081"),sQuery(id+"F2.wireOp",EDGE,"E1082"),sQuery(id+"F2.wireOp",EDGE,"E1083"),sQuery(id+"F2.wireOp",EDGE,"E1084"),sQuery(id+"F2.wireOp",EDGE,"E1085"),sQuery(id+"F2.wireOp",EDGE,"E1086"),sQuery(id+"F2.wireOp",EDGE,"E1087"),sQuery(id+"F2.wireOp",EDGE,"E1088"),sQuery(id+"F2.wireOp",EDGE,"E1089"),sQuery(id+"F2.wireOp",EDGE,"E1090"),sQuery(id+"F2.wireOp",EDGE,"E1091"),sQuery(id+"F2.wireOp",EDGE,"E1092"),sQuery(id+"F2.wireOp",EDGE,"E1093"),sQuery(id+"F2.wireOp",EDGE,"E1094"),sQuery(id+"F2.wireOp",EDGE,"E1095"),sQuery(id+"F2.wireOp",EDGE,"E1096"),sQuery(id+"F2.wireOp",EDGE,"E1097"),sQuery(id+"F2.wireOp",EDGE,"E1098"),sQuery(id+"F2.wireOp",EDGE,"E1099"),sQuery(id+"F2.wireOp",EDGE,"E1100"),sQuery(id+"F2.wireOp",EDGE,"E1101"),sQuery(id+"F2.wireOp",EDGE,"E1102"),sQuery(id+"F2.wireOp",EDGE,"E1103"),sQuery(id+"F2.wireOp",EDGE,"E1104"),sQuery(id+"F2.wireOp",EDGE,"E1105"),sQuery(id+"F2.wireOp",EDGE,"E1106"),sQuery(id+"F2.wireOp",EDGE,"E1107"),sQuery(id+"F2.wireOp",EDGE,"E1108"),sQuery(id+"F2.wireOp",EDGE,"E1109"),sQuery(id+"F2.wireOp",EDGE,"E1110"),sQuery(id+"F2.wireOp",EDGE,"E1111"),sQuery(id+"F2.wireOp",EDGE,"E1112"),sQuery(id+"F2.wireOp",EDGE,"E1113")])],"isStart":false})});
            var sketch = newSketch(context, id + "F13", { "sketchPlane" : qUnion([Q0])});
            skCircle(sketch, "E1120", {"center": v(14.78, 0) * mm, "radius": 1.5 * mm});
            skPoint(sketch, "E1121.center.orphan", {"position": v(0, 0) * mm});
            skSolve(sketch);
        }
        {
            var Q0;
            Q0=makeQuery(id+"F13.imprint","IMPRINT",FACE,{"disambiguationData":[TD([[makeQuery(id+"F13.imprint","IMPRINT",EDGE,{"derivedFrom":sQuery(id+"F13.wireOp",EDGE,"E1120")}),1.0]])]});
            extrude(context, id + "F14", {"entities" : qUnion([Q0]), "operationType" : NewBodyOperationType.REMOVE, "oppositeDirection" : true, "depth" : 25 * mm});
        }
    });
